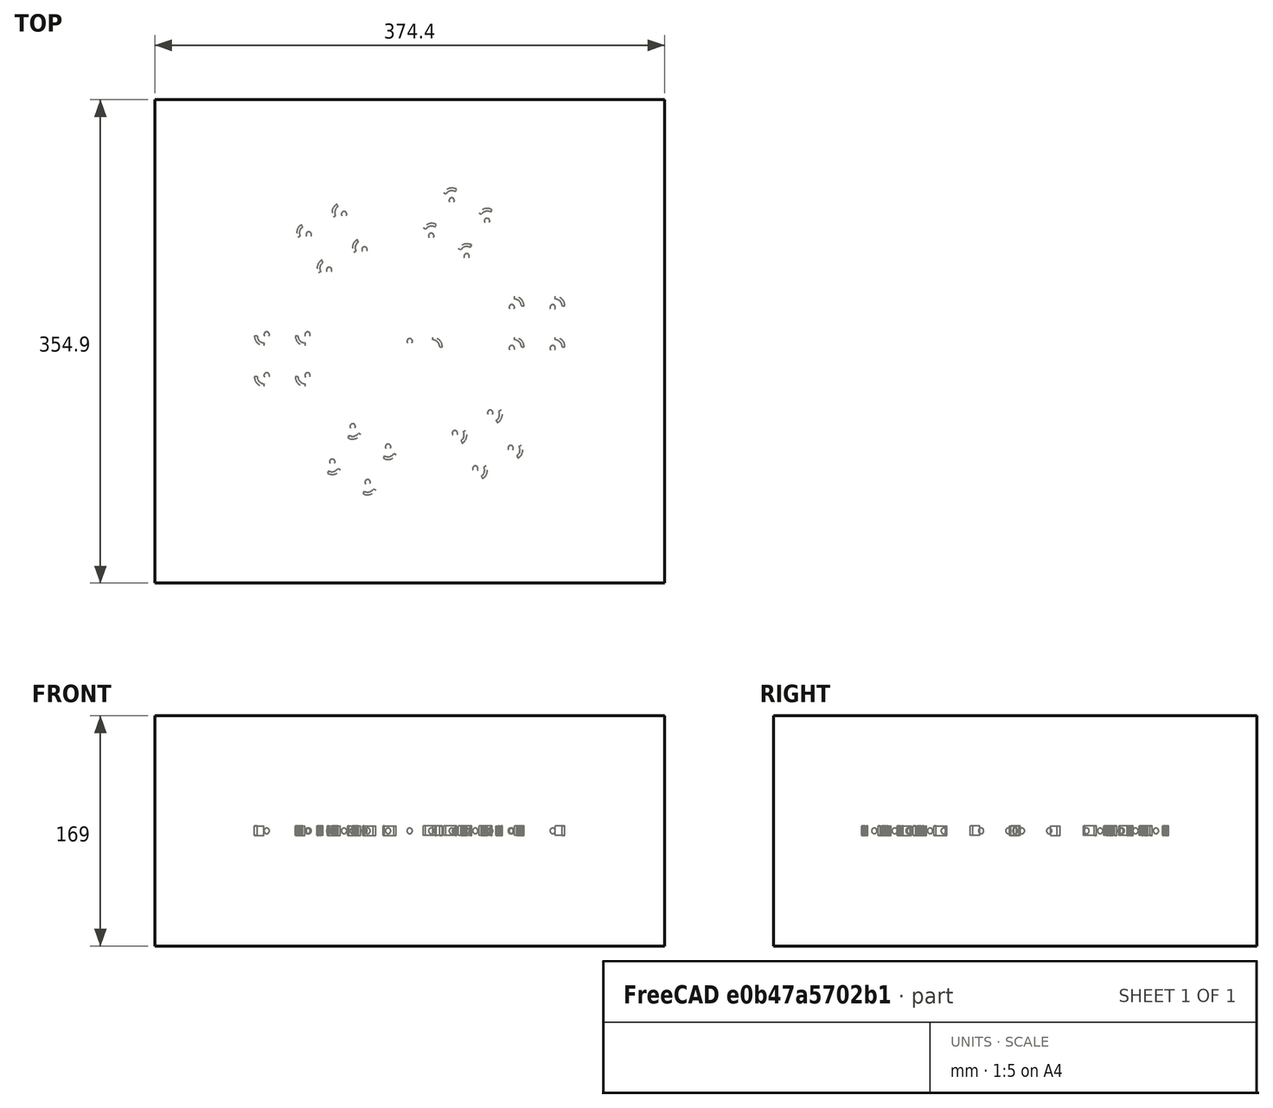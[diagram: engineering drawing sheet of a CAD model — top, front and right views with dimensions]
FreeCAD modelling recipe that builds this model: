
FCSTD DOCUMENT  (FreeCAD 0.21R33694 (Git))
Label: polarArrray-of-orthoArray-of-Assembly
License: All rights reserved
LicenseURL: http://en.wikipedia.org/wiki/All_rights_reserved
objects: App::DocumentObjectGroupPython×1251, App::Part×6, Part::FeaturePython×5
note: 5 computed .brp shape members not serialized (recipe doc carries the construction recipe); baked Part::Feature solids carry a one-line shape summary decoded from their .brp

FEATURE [App::DocumentObjectGroupPython] HALFPI  # scripted group (container) (typed FeaturePython)
  name = HALFPI
  value = pi/2.
FEATURE [App::DocumentObjectGroupPython] PI  # scripted group (container) (typed FeaturePython)
  name = PI
  value = 1.*pi
FEATURE [App::DocumentObjectGroupPython] TWOPI  # scripted group (container) (typed FeaturePython)
  name = TWOPI
  value = 2.*pi
FEATURE [App::DocumentObjectGroupPython] Constants  # scripted group (container) (typed FeaturePython)
  Group = -> [HALFPI,PI,TWOPI]
FEATURE [App::DocumentObjectGroupPython] Variables  # scripted group (container) (typed FeaturePython)
FEATURE [App::DocumentObjectGroupPython] Quantities  # scripted group (container) (typed FeaturePython)
FEATURE [App::DocumentObjectGroupPython] Isotopes  # scripted group (container) (typed FeaturePython)
FEATURE [App::DocumentObjectGroupPython] Elements  # scripted group (container) (typed FeaturePython)
FEATURE [App::DocumentObjectGroupPython] Matrix  # scripted group (container) (typed FeaturePython)
FEATURE [App::DocumentObjectGroupPython] Surfaces  # scripted group (container) (typed FeaturePython)
FEATURE [App::DocumentObjectGroupPython] Opticals  # scripted group (container) (typed FeaturePython)
  Group = -> [Matrix,Surfaces]
FEATURE [App::DocumentObjectGroupPython] G4Isotopes  # scripted group (container) (typed FeaturePython)
FEATURE [App::DocumentObjectGroupPython] H_element  # scripted group (container) (typed FeaturePython)
  Z = 1
  atom_value = 1.008
  formula = H
  name = H_element
FEATURE [App::DocumentObjectGroupPython] He_element  # scripted group (container) (typed FeaturePython)
  Z = 2
  atom_value = 4.0026
  formula = He
  name = He_element
FEATURE [App::DocumentObjectGroupPython] Li_element  # scripted group (container) (typed FeaturePython)
  Z = 3
  atom_value = 6.94
  formula = Li
  name = Li_element
FEATURE [App::DocumentObjectGroupPython] Be_element  # scripted group (container) (typed FeaturePython)
  Z = 4
  atom_value = 9.01218
  formula = Be
  name = Be_element
FEATURE [App::DocumentObjectGroupPython] B_element  # scripted group (container) (typed FeaturePython)
  Z = 5
  atom_value = 10.81
  formula = B
  name = B_element
FEATURE [App::DocumentObjectGroupPython] C_element  # scripted group (container) (typed FeaturePython)
  Z = 6
  atom_value = 12.011
  formula = C
  name = C_element
FEATURE [App::DocumentObjectGroupPython] N_element  # scripted group (container) (typed FeaturePython)
  Z = 7
  atom_value = 14.007
  formula = N
  name = N_element
FEATURE [App::DocumentObjectGroupPython] O_element  # scripted group (container) (typed FeaturePython)
  Z = 8
  atom_value = 15.999
  formula = O
  name = O_element
FEATURE [App::DocumentObjectGroupPython] F_element  # scripted group (container) (typed FeaturePython)
  Z = 9
  atom_value = 18.9984
  formula = F
  name = F_element
FEATURE [App::DocumentObjectGroupPython] Ne_element  # scripted group (container) (typed FeaturePython)
  Z = 10
  atom_value = 20.1797
  formula = Ne
  name = Ne_element
FEATURE [App::DocumentObjectGroupPython] Na_element  # scripted group (container) (typed FeaturePython)
  Z = 11
  atom_value = 22.9898
  formula = Na
  name = Na_element
FEATURE [App::DocumentObjectGroupPython] Mg_element  # scripted group (container) (typed FeaturePython)
  Z = 12
  atom_value = 24.305
  formula = Mg
  name = Mg_element
FEATURE [App::DocumentObjectGroupPython] Al_element  # scripted group (container) (typed FeaturePython)
  Z = 13
  atom_value = 26.9815
  formula = Al
  name = Al_element
FEATURE [App::DocumentObjectGroupPython] Si_element  # scripted group (container) (typed FeaturePython)
  Z = 14
  atom_value = 28.085
  formula = Si
  name = Si_element
FEATURE [App::DocumentObjectGroupPython] P_element  # scripted group (container) (typed FeaturePython)
  Z = 15
  atom_value = 30.9738
  formula = P
  name = P_element
FEATURE [App::DocumentObjectGroupPython] S_element  # scripted group (container) (typed FeaturePython)
  Z = 16
  atom_value = 32.06
  formula = S
  name = S_element
FEATURE [App::DocumentObjectGroupPython] Cl_element  # scripted group (container) (typed FeaturePython)
  Z = 17
  atom_value = 35.45
  formula = Cl
  name = Cl_element
FEATURE [App::DocumentObjectGroupPython] Ar_element  # scripted group (container) (typed FeaturePython)
  Z = 18
  atom_value = 39.95
  formula = Ar
  name = Ar_element
FEATURE [App::DocumentObjectGroupPython] K_element  # scripted group (container) (typed FeaturePython)
  Z = 19
  atom_value = 39.0983
  formula = K
  name = K_element
FEATURE [App::DocumentObjectGroupPython] Ca_element  # scripted group (container) (typed FeaturePython)
  Z = 20
  atom_value = 40.078
  formula = Ca
  name = Ca_element
FEATURE [App::DocumentObjectGroupPython] Sc_element  # scripted group (container) (typed FeaturePython)
  Z = 21
  atom_value = 44.9559
  formula = Sc
  name = Sc_element
FEATURE [App::DocumentObjectGroupPython] Ti_element  # scripted group (container) (typed FeaturePython)
  Z = 22
  atom_value = 47.867
  formula = Ti
  name = Ti_element
FEATURE [App::DocumentObjectGroupPython] V_element  # scripted group (container) (typed FeaturePython)
  Z = 23
  atom_value = 50.9415
  formula = V
  name = V_element
FEATURE [App::DocumentObjectGroupPython] Cr_element  # scripted group (container) (typed FeaturePython)
  Z = 24
  atom_value = 51.9961
  formula = Cr
  name = Cr_element
FEATURE [App::DocumentObjectGroupPython] Mn_element  # scripted group (container) (typed FeaturePython)
  Z = 25
  atom_value = 54.938
  formula = Mn
  name = Mn_element
FEATURE [App::DocumentObjectGroupPython] Fe_element  # scripted group (container) (typed FeaturePython)
  Z = 26
  atom_value = 55.845
  formula = Fe
  name = Fe_element
FEATURE [App::DocumentObjectGroupPython] Co_element  # scripted group (container) (typed FeaturePython)
  Z = 27
  atom_value = 58.9332
  formula = Co
  name = Co_element
FEATURE [App::DocumentObjectGroupPython] Ni_element  # scripted group (container) (typed FeaturePython)
  Z = 28
  atom_value = 58.6934
  formula = Ni
  name = Ni_element
FEATURE [App::DocumentObjectGroupPython] Cu_element  # scripted group (container) (typed FeaturePython)
  Z = 29
  atom_value = 63.546
  formula = Cu
  name = Cu_element
FEATURE [App::DocumentObjectGroupPython] Zn_element  # scripted group (container) (typed FeaturePython)
  Z = 30
  atom_value = 65.38
  formula = Zn
  name = Zn_element
FEATURE [App::DocumentObjectGroupPython] Ga_element  # scripted group (container) (typed FeaturePython)
  Z = 31
  atom_value = 69.723
  formula = Ga
  name = Ga_element
FEATURE [App::DocumentObjectGroupPython] Ge_element  # scripted group (container) (typed FeaturePython)
  Z = 32
  atom_value = 72.63
  formula = Ge
  name = Ge_element
FEATURE [App::DocumentObjectGroupPython] As_element  # scripted group (container) (typed FeaturePython)
  Z = 33
  atom_value = 74.9216
  formula = As
  name = As_element
FEATURE [App::DocumentObjectGroupPython] Se_element  # scripted group (container) (typed FeaturePython)
  Z = 34
  atom_value = 78.971
  formula = Se
  name = Se_element
FEATURE [App::DocumentObjectGroupPython] Br_element  # scripted group (container) (typed FeaturePython)
  Z = 35
  atom_value = 79.904
  formula = Br
  name = Br_element
FEATURE [App::DocumentObjectGroupPython] Kr_element  # scripted group (container) (typed FeaturePython)
  Z = 36
  atom_value = 83.798
  formula = Kr
  name = Kr_element
FEATURE [App::DocumentObjectGroupPython] Rb_element  # scripted group (container) (typed FeaturePython)
  Z = 37
  atom_value = 85.4678
  formula = Rb
  name = Rb_element
FEATURE [App::DocumentObjectGroupPython] Sr_element  # scripted group (container) (typed FeaturePython)
  Z = 38
  atom_value = 87.62
  formula = Sr
  name = Sr_element
FEATURE [App::DocumentObjectGroupPython] Y_element  # scripted group (container) (typed FeaturePython)
  Z = 39
  atom_value = 88.9058
  formula = Y
  name = Y_element
FEATURE [App::DocumentObjectGroupPython] Zr_element  # scripted group (container) (typed FeaturePython)
  Z = 40
  atom_value = 91.224
  formula = Zr
  name = Zr_element
FEATURE [App::DocumentObjectGroupPython] Nb_element  # scripted group (container) (typed FeaturePython)
  Z = 41
  atom_value = 92.9064
  formula = Nb
  name = Nb_element
FEATURE [App::DocumentObjectGroupPython] Mo_element  # scripted group (container) (typed FeaturePython)
  Z = 42
  atom_value = 95.95
  formula = Mo
  name = Mo_element
FEATURE [App::DocumentObjectGroupPython] Tc_element  # scripted group (container) (typed FeaturePython)
  Z = 43
  atom_value = 97
  formula = Tc
  name = Tc_element
FEATURE [App::DocumentObjectGroupPython] Ru_element  # scripted group (container) (typed FeaturePython)
  Z = 44
  atom_value = 101.07
  formula = Ru
  name = Ru_element
FEATURE [App::DocumentObjectGroupPython] Rh_element  # scripted group (container) (typed FeaturePython)
  Z = 45
  atom_value = 102.905
  formula = Rh
  name = Rh_element
FEATURE [App::DocumentObjectGroupPython] Pd_element  # scripted group (container) (typed FeaturePython)
  Z = 46
  atom_value = 106.42
  formula = Pd
  name = Pd_element
FEATURE [App::DocumentObjectGroupPython] Ag_element  # scripted group (container) (typed FeaturePython)
  Z = 47
  atom_value = 107.868
  formula = Ag
  name = Ag_element
FEATURE [App::DocumentObjectGroupPython] Cd_element  # scripted group (container) (typed FeaturePython)
  Z = 48
  atom_value = 112.414
  formula = Cd
  name = Cd_element
FEATURE [App::DocumentObjectGroupPython] In_element  # scripted group (container) (typed FeaturePython)
  Z = 49
  atom_value = 114.818
  formula = In
  name = In_element
FEATURE [App::DocumentObjectGroupPython] Sn_element  # scripted group (container) (typed FeaturePython)
  Z = 50
  atom_value = 118.71
  formula = Sn
  name = Sn_element
FEATURE [App::DocumentObjectGroupPython] Sb_element  # scripted group (container) (typed FeaturePython)
  Z = 51
  atom_value = 121.76
  formula = Sb
  name = Sb_element
FEATURE [App::DocumentObjectGroupPython] Te_element  # scripted group (container) (typed FeaturePython)
  Z = 52
  atom_value = 127.6
  formula = Te
  name = Te_element
FEATURE [App::DocumentObjectGroupPython] I_element  # scripted group (container) (typed FeaturePython)
  Z = 53
  atom_value = 126.904
  formula = I
  name = I_element
FEATURE [App::DocumentObjectGroupPython] Xe_element  # scripted group (container) (typed FeaturePython)
  Z = 54
  atom_value = 131.293
  formula = Xe
  name = Xe_element
FEATURE [App::DocumentObjectGroupPython] Cs_element  # scripted group (container) (typed FeaturePython)
  Z = 55
  atom_value = 132.905
  formula = Cs
  name = Cs_element
FEATURE [App::DocumentObjectGroupPython] Ba_element  # scripted group (container) (typed FeaturePython)
  Z = 56
  atom_value = 137.327
  formula = Ba
  name = Ba_element
FEATURE [App::DocumentObjectGroupPython] La_element  # scripted group (container) (typed FeaturePython)
  Z = 57
  atom_value = 138.905
  formula = La
  name = La_element
FEATURE [App::DocumentObjectGroupPython] Ce_element  # scripted group (container) (typed FeaturePython)
  Z = 58
  atom_value = 140.116
  formula = Ce
  name = Ce_element
FEATURE [App::DocumentObjectGroupPython] Pr_element  # scripted group (container) (typed FeaturePython)
  Z = 59
  atom_value = 140.908
  formula = Pr
  name = Pr_element
FEATURE [App::DocumentObjectGroupPython] Nd_element  # scripted group (container) (typed FeaturePython)
  Z = 60
  atom_value = 144.242
  formula = Nd
  name = Nd_element
FEATURE [App::DocumentObjectGroupPython] Pm_element  # scripted group (container) (typed FeaturePython)
  Z = 61
  atom_value = 145
  formula = Pm
  name = Pm_element
FEATURE [App::DocumentObjectGroupPython] Sm_element  # scripted group (container) (typed FeaturePython)
  Z = 62
  atom_value = 150.36
  formula = Sm
  name = Sm_element
FEATURE [App::DocumentObjectGroupPython] Eu_element  # scripted group (container) (typed FeaturePython)
  Z = 63
  atom_value = 151.964
  formula = Eu
  name = Eu_element
FEATURE [App::DocumentObjectGroupPython] Gd_element  # scripted group (container) (typed FeaturePython)
  Z = 64
  atom_value = 157.25
  formula = Gd
  name = Gd_element
FEATURE [App::DocumentObjectGroupPython] Tb_element  # scripted group (container) (typed FeaturePython)
  Z = 65
  atom_value = 158.925
  formula = Tb
  name = Tb_element
FEATURE [App::DocumentObjectGroupPython] Dy_element  # scripted group (container) (typed FeaturePython)
  Z = 66
  atom_value = 162.5
  formula = Dy
  name = Dy_element
FEATURE [App::DocumentObjectGroupPython] Ho_element  # scripted group (container) (typed FeaturePython)
  Z = 67
  atom_value = 164.93
  formula = Ho
  name = Ho_element
FEATURE [App::DocumentObjectGroupPython] Er_element  # scripted group (container) (typed FeaturePython)
  Z = 68
  atom_value = 167.259
  formula = Er
  name = Er_element
FEATURE [App::DocumentObjectGroupPython] Tm_element  # scripted group (container) (typed FeaturePython)
  Z = 69
  atom_value = 168.934
  formula = Tm
  name = Tm_element
FEATURE [App::DocumentObjectGroupPython] Yb_element  # scripted group (container) (typed FeaturePython)
  Z = 70
  atom_value = 173.045
  formula = Yb
  name = Yb_element
FEATURE [App::DocumentObjectGroupPython] Lu_element  # scripted group (container) (typed FeaturePython)
  Z = 71
  atom_value = 174.967
  formula = Lu
  name = Lu_element
FEATURE [App::DocumentObjectGroupPython] Hf_element  # scripted group (container) (typed FeaturePython)
  Z = 72
  atom_value = 178.49
  formula = Hf
  name = Hf_element
FEATURE [App::DocumentObjectGroupPython] Ta_element  # scripted group (container) (typed FeaturePython)
  Z = 73
  atom_value = 180.948
  formula = Ta
  name = Ta_element
FEATURE [App::DocumentObjectGroupPython] W_element  # scripted group (container) (typed FeaturePython)
  Z = 74
  atom_value = 183.84
  formula = W
  name = W_element
FEATURE [App::DocumentObjectGroupPython] Re_element  # scripted group (container) (typed FeaturePython)
  Z = 75
  atom_value = 186.207
  formula = Re
  name = Re_element
FEATURE [App::DocumentObjectGroupPython] Os_element  # scripted group (container) (typed FeaturePython)
  Z = 76
  atom_value = 190.23
  formula = Os
  name = Os_element
FEATURE [App::DocumentObjectGroupPython] Ir_element  # scripted group (container) (typed FeaturePython)
  Z = 77
  atom_value = 192.217
  formula = Ir
  name = Ir_element
FEATURE [App::DocumentObjectGroupPython] Pt_element  # scripted group (container) (typed FeaturePython)
  Z = 78
  atom_value = 195.084
  formula = Pt
  name = Pt_element
FEATURE [App::DocumentObjectGroupPython] Au_element  # scripted group (container) (typed FeaturePython)
  Z = 79
  atom_value = 196.967
  formula = Au
  name = Au_element
FEATURE [App::DocumentObjectGroupPython] Hg_element  # scripted group (container) (typed FeaturePython)
  Z = 80
  atom_value = 200.592
  formula = Hg
  name = Hg_element
FEATURE [App::DocumentObjectGroupPython] Tl_element  # scripted group (container) (typed FeaturePython)
  Z = 81
  atom_value = 204.38
  formula = Tl
  name = Tl_element
FEATURE [App::DocumentObjectGroupPython] Pb_element  # scripted group (container) (typed FeaturePython)
  Z = 82
  atom_value = 207.2
  formula = Pb
  name = Pb_element
FEATURE [App::DocumentObjectGroupPython] Bi_element  # scripted group (container) (typed FeaturePython)
  Z = 83
  atom_value = 208.98
  formula = Bi
  name = Bi_element
FEATURE [App::DocumentObjectGroupPython] Po_element  # scripted group (container) (typed FeaturePython)
  Z = 84
  atom_value = 209
  formula = Po
  name = Po_element
FEATURE [App::DocumentObjectGroupPython] At_element  # scripted group (container) (typed FeaturePython)
  Z = 85
  atom_value = 210
  formula = At
  name = At_element
FEATURE [App::DocumentObjectGroupPython] Rn_element  # scripted group (container) (typed FeaturePython)
  Z = 86
  atom_value = 222
  formula = Rn
  name = Rn_element
FEATURE [App::DocumentObjectGroupPython] Fr_element  # scripted group (container) (typed FeaturePython)
  Z = 87
  atom_value = 223
  formula = Fr
  name = Fr_element
FEATURE [App::DocumentObjectGroupPython] Ra_element  # scripted group (container) (typed FeaturePython)
  Z = 88
  atom_value = 226
  formula = Ra
  name = Ra_element
FEATURE [App::DocumentObjectGroupPython] Ac_element  # scripted group (container) (typed FeaturePython)
  Z = 89
  atom_value = 227
  formula = Ac
  name = Ac_element
FEATURE [App::DocumentObjectGroupPython] Th_element  # scripted group (container) (typed FeaturePython)
  Z = 90
  atom_value = 232.038
  formula = Th
  name = Th_element
FEATURE [App::DocumentObjectGroupPython] Pa_element  # scripted group (container) (typed FeaturePython)
  Z = 91
  atom_value = 231.036
  formula = Pa
  name = Pa_element
FEATURE [App::DocumentObjectGroupPython] U_element  # scripted group (container) (typed FeaturePython)
  Z = 92
  atom_value = 238.029
  formula = U
  name = U_element
FEATURE [App::DocumentObjectGroupPython] Np_element  # scripted group (container) (typed FeaturePython)
  Z = 93
  atom_value = 237
  formula = Np
  name = Np_element
FEATURE [App::DocumentObjectGroupPython] Pu_element  # scripted group (container) (typed FeaturePython)
  Z = 94
  atom_value = 244
  formula = Pu
  name = Pu_element
FEATURE [App::DocumentObjectGroupPython] Am_element  # scripted group (container) (typed FeaturePython)
  Z = 95
  atom_value = 243
  formula = Am
  name = Am_element
FEATURE [App::DocumentObjectGroupPython] Cm_element  # scripted group (container) (typed FeaturePython)
  Z = 96
  atom_value = 247
  formula = Cm
  name = Cm_element
FEATURE [App::DocumentObjectGroupPython] Bk_element  # scripted group (container) (typed FeaturePython)
  Z = 97
  atom_value = 247
  formula = Bk
  name = Bk_element
FEATURE [App::DocumentObjectGroupPython] Cf_element  # scripted group (container) (typed FeaturePython)
  Z = 98
  atom_value = 251
  formula = Cf
  name = Cf_element
FEATURE [App::DocumentObjectGroupPython] G4Elements  # scripted group (container) (typed FeaturePython)
  Group = -> [H_element,He_element,Li_element,Be_element,B_element,C_element,N_element,O_element,F_element,Ne_element,Na_element,Mg_element,Al_element,Si_element,P_element,S_element,Cl_element,Ar_element,K_element,Ca_element,Sc_element,Ti_element,V_element,Cr_element,Mn_element,Fe_element,Co_element,Ni_element,Cu_element,Zn_element,Ga_element,Ge_element,As_element,Se_element,Br_element,Kr_element,Rb_element,+61 more]
FEATURE [App::DocumentObjectGroupPython] H_element001  label="H_element : 0.101"  # scripted group (container) (typed FeaturePython)
  n = 0.101327
FEATURE [App::DocumentObjectGroupPython] C_element001  label="C_element : 0.775"  # scripted group (container) (typed FeaturePython)
  n = 0.7755
FEATURE [App::DocumentObjectGroupPython] N_element001  label="N_element : 0.035"  # scripted group (container) (typed FeaturePython)
  n = 0.035057
FEATURE [App::DocumentObjectGroupPython] O_element001  label="O_element : 0.052"  # scripted group (container) (typed FeaturePython)
  n = 0.0523159
FEATURE [App::DocumentObjectGroupPython] F_element001  label="F_element : 0.017"  # scripted group (container) (typed FeaturePython)
  n = 0.017422
FEATURE [App::DocumentObjectGroupPython] Ca_element001  label="Ca_element : 0.018"  # scripted group (container) (typed FeaturePython)
  n = 0.018378
FEATURE [App::DocumentObjectGroupPython] G4_A_150_TISSUE  label="G4_A-150_TISSUE"  # scripted group (container) (typed FeaturePython)
  Dunit = g/cm3
  Dvalue = 1.127
  Group = -> [H_element001,C_element001,N_element001,O_element001,F_element001,Ca_element001]
  conduct = 2
  density = 1
  expand = 3
  formula = G4_A-150_TISSUE
  name = G4_A-150_TISSUE
  specific = 4
FEATURE [App::DocumentObjectGroupPython] C_element002  label="C_element : 3"  # scripted group (container) (typed FeaturePython)
  n = 3
  ref = C_element
FEATURE [App::DocumentObjectGroupPython] H_element002  label="H_element : 6"  # scripted group (container) (typed FeaturePython)
  n = 6
  ref = H_element
FEATURE [App::DocumentObjectGroupPython] O_element002  label="O_element : 1"  # scripted group (container) (typed FeaturePython)
  n = 1
  ref = O_element
FEATURE [App::DocumentObjectGroupPython] G4_ACETONE  # scripted group (container) (typed FeaturePython)
  Dunit = g/cm3
  Dvalue = 0.7899
  Group = -> [C_element002,H_element002,O_element002]
  conduct = 2
  density = 1
  expand = 3
  formula = G4_ACETONE
  name = G4_ACETONE
  specific = 4
FEATURE [App::DocumentObjectGroupPython] C_element003  label="C_element : 2"  # scripted group (container) (typed FeaturePython)
  n = 2
  ref = C_element
FEATURE [App::DocumentObjectGroupPython] H_element003  label="H_element : 2"  # scripted group (container) (typed FeaturePython)
  n = 2
  ref = H_element
FEATURE [App::DocumentObjectGroupPython] G4_ACETYLENE  # scripted group (container) (typed FeaturePython)
  Dunit = g/cm3
  Dvalue = 0.0010967
  Group = -> [C_element003,H_element003]
  conduct = 2
  density = 1
  expand = 3
  formula = G4_ACETYLENE
  name = G4_ACETYLENE
  specific = 4
FEATURE [App::DocumentObjectGroupPython] C_element004  label="C_element : 5"  # scripted group (container) (typed FeaturePython)
  n = 5
  ref = C_element
FEATURE [App::DocumentObjectGroupPython] H_element004  label="H_element : 5"  # scripted group (container) (typed FeaturePython)
  n = 5
  ref = H_element
FEATURE [App::DocumentObjectGroupPython] N_element002  label="N_element : 5"  # scripted group (container) (typed FeaturePython)
  n = 5
  ref = N_element
FEATURE [App::DocumentObjectGroupPython] G4_ADENINE  # scripted group (container) (typed FeaturePython)
  Dunit = g/cm3
  Dvalue = 1.6
  Group = -> [C_element004,H_element004,N_element002]
  conduct = 2
  density = 1
  expand = 3
  formula = G4_ADENINE
  name = G4_ADENINE
  specific = 4
FEATURE [App::DocumentObjectGroupPython] H_element005  label="H_element : 0.114"  # scripted group (container) (typed FeaturePython)
  n = 0.114
FEATURE [App::DocumentObjectGroupPython] C_element005  label="C_element : 0.598"  # scripted group (container) (typed FeaturePython)
  n = 0.598
FEATURE [App::DocumentObjectGroupPython] N_element003  label="N_element : 0.007"  # scripted group (container) (typed FeaturePython)
  n = 0.007
FEATURE [App::DocumentObjectGroupPython] O_element003  label="O_element : 0.278"  # scripted group (container) (typed FeaturePython)
  n = 0.278
FEATURE [App::DocumentObjectGroupPython] Na_element001  label="Na_element : 0.001"  # scripted group (container) (typed FeaturePython)
  n = 0.001
FEATURE [App::DocumentObjectGroupPython] S_element001  label="S_element : 0.001"  # scripted group (container) (typed FeaturePython)
  n = 0.001
FEATURE [App::DocumentObjectGroupPython] Cl_element001  label="Cl_element : 0.001"  # scripted group (container) (typed FeaturePython)
  n = 0.001
FEATURE [App::DocumentObjectGroupPython] G4_ADIPOSE_TISSUE_ICRP  # scripted group (container) (typed FeaturePython)
  Dunit = g/cm3
  Dvalue = 0.95
  Group = -> [H_element005,C_element005,N_element003,O_element003,Na_element001,S_element001,Cl_element001]
  conduct = 2
  density = 1
  expand = 3
  formula = G4_ADIPOSE_TISSUE_ICRP
  name = G4_ADIPOSE_TISSUE_ICRP
  specific = 4
FEATURE [App::DocumentObjectGroupPython] C_element006  label="C_element : 0.000"  # scripted group (container) (typed FeaturePython)
  n = 0.000124
FEATURE [App::DocumentObjectGroupPython] N_element004  label="N_element : 0.755"  # scripted group (container) (typed FeaturePython)
  n = 0.755268
FEATURE [App::DocumentObjectGroupPython] O_element004  label="O_element : 0.232"  # scripted group (container) (typed FeaturePython)
  n = 0.231781
FEATURE [App::DocumentObjectGroupPython] Ar_element001  label="Ar_element : 0.013"  # scripted group (container) (typed FeaturePython)
  n = 0.012827
FEATURE [App::DocumentObjectGroupPython] G4_AIR  # scripted group (container) (typed FeaturePython)
  Dunit = g/cm3
  Dvalue = 0.00120479
  Group = -> [C_element006,N_element004,O_element004,Ar_element001]
  conduct = 2
  density = 1
  expand = 3
  formula = G4_AIR
  name = G4_AIR
  specific = 4
FEATURE [App::DocumentObjectGroupPython] C_element007  label="C_element : 006"  # scripted group (container) (typed FeaturePython)
  n = 3
  ref = C_element
FEATURE [App::DocumentObjectGroupPython] H_element006  label="H_element : 7"  # scripted group (container) (typed FeaturePython)
  n = 7
  ref = H_element
FEATURE [App::DocumentObjectGroupPython] N_element005  label="N_element : 1"  # scripted group (container) (typed FeaturePython)
  n = 1
  ref = N_element
FEATURE [App::DocumentObjectGroupPython] O_element005  label="O_element : 2"  # scripted group (container) (typed FeaturePython)
  n = 2
  ref = O_element
FEATURE [App::DocumentObjectGroupPython] G4_ALANINE  # scripted group (container) (typed FeaturePython)
  Dunit = g/cm3
  Dvalue = 1.42
  Group = -> [C_element007,H_element006,N_element005,O_element005]
  conduct = 2
  density = 1
  expand = 3
  formula = G4_ALANINE
  name = G4_ALANINE
  specific = 4
FEATURE [App::DocumentObjectGroupPython] Al_element001  label="Al_element : 2"  # scripted group (container) (typed FeaturePython)
  n = 2
  ref = Al_element
FEATURE [App::DocumentObjectGroupPython] O_element006  label="O_element : 3"  # scripted group (container) (typed FeaturePython)
  n = 3
  ref = O_element
FEATURE [App::DocumentObjectGroupPython] G4_ALUMINUM_OXIDE  # scripted group (container) (typed FeaturePython)
  Dunit = g/cm3
  Dvalue = 3.97
  Group = -> [Al_element001,O_element006]
  conduct = 2
  density = 1
  expand = 3
  formula = G4_ALUMINUM_OXIDE
  name = G4_ALUMINUM_OXIDE
  specific = 4
FEATURE [App::DocumentObjectGroupPython] H_element007  label="H_element : 0.106"  # scripted group (container) (typed FeaturePython)
  n = 0.10593
FEATURE [App::DocumentObjectGroupPython] C_element008  label="C_element : 0.789"  # scripted group (container) (typed FeaturePython)
  n = 0.788974
FEATURE [App::DocumentObjectGroupPython] O_element007  label="O_element : 0.105"  # scripted group (container) (typed FeaturePython)
  n = 0.105096
FEATURE [App::DocumentObjectGroupPython] G4_AMBER  # scripted group (container) (typed FeaturePython)
  Dunit = g/cm3
  Dvalue = 1.1
  Group = -> [H_element007,C_element008,O_element007]
  conduct = 2
  density = 1
  expand = 3
  formula = G4_AMBER
  name = G4_AMBER
  specific = 4
FEATURE [App::DocumentObjectGroupPython] N_element006  label="N_element : 006"  # scripted group (container) (typed FeaturePython)
  n = 1
  ref = N_element
FEATURE [App::DocumentObjectGroupPython] H_element008  label="H_element : 3"  # scripted group (container) (typed FeaturePython)
  n = 3
  ref = H_element
FEATURE [App::DocumentObjectGroupPython] G4_AMMONIA  # scripted group (container) (typed FeaturePython)
  Dunit = g/cm3
  Dvalue = 0.000826019
  Group = -> [N_element006,H_element008]
  conduct = 2
  density = 1
  expand = 3
  formula = G4_AMMONIA
  name = G4_AMMONIA
  specific = 4
FEATURE [App::DocumentObjectGroupPython] C_element009  label="C_element : 6"  # scripted group (container) (typed FeaturePython)
  n = 6
  ref = C_element
FEATURE [App::DocumentObjectGroupPython] H_element009  label="H_element : 008"  # scripted group (container) (typed FeaturePython)
  n = 7
  ref = H_element
FEATURE [App::DocumentObjectGroupPython] N_element007  label="N_element : 007"  # scripted group (container) (typed FeaturePython)
  n = 1
  ref = N_element
FEATURE [App::DocumentObjectGroupPython] G4_ANILINE  # scripted group (container) (typed FeaturePython)
  Dunit = g/cm3
  Dvalue = 1.0235
  Group = -> [C_element009,H_element009,N_element007]
  conduct = 2
  density = 1
  expand = 3
  formula = G4_ANILINE
  name = G4_ANILINE
  specific = 4
FEATURE [App::DocumentObjectGroupPython] C_element010  label="C_element : 14"  # scripted group (container) (typed FeaturePython)
  n = 14
  ref = C_element
FEATURE [App::DocumentObjectGroupPython] H_element010  label="H_element : 10"  # scripted group (container) (typed FeaturePython)
  n = 10
  ref = H_element
FEATURE [App::DocumentObjectGroupPython] G4_ANTHRACENE  # scripted group (container) (typed FeaturePython)
  Dunit = g/cm3
  Dvalue = 1.283
  Group = -> [C_element010,H_element010]
  conduct = 2
  density = 1
  expand = 3
  formula = G4_ANTHRACENE
  name = G4_ANTHRACENE
  specific = 4
FEATURE [App::DocumentObjectGroupPython] H_element011  label="H_element : 0.065"  # scripted group (container) (typed FeaturePython)
  n = 0.0654709
FEATURE [App::DocumentObjectGroupPython] C_element011  label="C_element : 0.537"  # scripted group (container) (typed FeaturePython)
  n = 0.536944
FEATURE [App::DocumentObjectGroupPython] N_element008  label="N_element : 0.021"  # scripted group (container) (typed FeaturePython)
  n = 0.0215
FEATURE [App::DocumentObjectGroupPython] O_element008  label="O_element : 0.032"  # scripted group (container) (typed FeaturePython)
  n = 0.032085
FEATURE [App::DocumentObjectGroupPython] F_element002  label="F_element : 0.167"  # scripted group (container) (typed FeaturePython)
  n = 0.167411
FEATURE [App::DocumentObjectGroupPython] Ca_element002  label="Ca_element : 0.177"  # scripted group (container) (typed FeaturePython)
  n = 0.176589
FEATURE [App::DocumentObjectGroupPython] G4_B_100_BONE  label="G4_B-100_BONE"  # scripted group (container) (typed FeaturePython)
  Dunit = g/cm3
  Dvalue = 1.45
  Group = -> [H_element011,C_element011,N_element008,O_element008,F_element002,Ca_element002]
  conduct = 2
  density = 1
  expand = 3
  formula = G4_B-100_BONE
  name = G4_B-100_BONE
  specific = 4
FEATURE [App::DocumentObjectGroupPython] H_element012  label="H_element : 0.057"  # scripted group (container) (typed FeaturePython)
  n = 0.057441
FEATURE [App::DocumentObjectGroupPython] C_element012  label="C_element : 0.790"  # scripted group (container) (typed FeaturePython)
  n = 0.774591
FEATURE [App::DocumentObjectGroupPython] O_element009  label="O_element : 0.168"  # scripted group (container) (typed FeaturePython)
  n = 0.167968
FEATURE [App::DocumentObjectGroupPython] G4_BAKELITE  # scripted group (container) (typed FeaturePython)
  Dunit = g/cm3
  Dvalue = 1.25
  Group = -> [H_element012,C_element012,O_element009]
  conduct = 2
  density = 1
  expand = 3
  formula = G4_BAKELITE
  name = G4_BAKELITE
  specific = 4
FEATURE [App::DocumentObjectGroupPython] Ba_element001  label="Ba_element : 1"  # scripted group (container) (typed FeaturePython)
  n = 1
  ref = Ba_element
FEATURE [App::DocumentObjectGroupPython] F_element003  label="F_element : 2"  # scripted group (container) (typed FeaturePython)
  n = 2
  ref = F_element
FEATURE [App::DocumentObjectGroupPython] G4_BARIUM_FLUORIDE  # scripted group (container) (typed FeaturePython)
  Dunit = g/cm3
  Dvalue = 4.89
  Group = -> [Ba_element001,F_element003]
  conduct = 2
  density = 1
  expand = 3
  formula = G4_BARIUM_FLUORIDE
  name = G4_BARIUM_FLUORIDE
  specific = 4
FEATURE [App::DocumentObjectGroupPython] Ba_element002  label="Ba_element : 002"  # scripted group (container) (typed FeaturePython)
  n = 1
  ref = Ba_element
FEATURE [App::DocumentObjectGroupPython] S_element002  label="S_element : 1"  # scripted group (container) (typed FeaturePython)
  n = 1
  ref = S_element
FEATURE [App::DocumentObjectGroupPython] O_element010  label="O_element : 4"  # scripted group (container) (typed FeaturePython)
  n = 4
  ref = O_element
FEATURE [App::DocumentObjectGroupPython] G4_BARIUM_SULFATE  # scripted group (container) (typed FeaturePython)
  Dunit = g/cm3
  Dvalue = 4.5
  Group = -> [Ba_element002,S_element002,O_element010]
  conduct = 2
  density = 1
  expand = 3
  formula = G4_BARIUM_SULFATE
  name = G4_BARIUM_SULFATE
  specific = 4
FEATURE [App::DocumentObjectGroupPython] C_element013  label="C_element : 007"  # scripted group (container) (typed FeaturePython)
  n = 6
  ref = C_element
FEATURE [App::DocumentObjectGroupPython] H_element013  label="H_element : 009"  # scripted group (container) (typed FeaturePython)
  n = 6
  ref = H_element
FEATURE [App::DocumentObjectGroupPython] G4_BENZENE  # scripted group (container) (typed FeaturePython)
  Dunit = g/cm3
  Dvalue = 0.87865
  Group = -> [C_element013,H_element013]
  conduct = 2
  density = 1
  expand = 3
  formula = G4_BENZENE
  name = G4_BENZENE
  specific = 4
FEATURE [App::DocumentObjectGroupPython] Be_element001  label="Be_element : 1"  # scripted group (container) (typed FeaturePython)
  n = 1
  ref = Be_element
FEATURE [App::DocumentObjectGroupPython] O_element011  label="O_element : 005"  # scripted group (container) (typed FeaturePython)
  n = 1
  ref = O_element
FEATURE [App::DocumentObjectGroupPython] G4_BERYLLIUM_OXIDE  # scripted group (container) (typed FeaturePython)
  Dunit = g/cm3
  Dvalue = 3.01
  Group = -> [Be_element001,O_element011]
  conduct = 2
  density = 1
  expand = 3
  formula = G4_BERYLLIUM_OXIDE
  name = G4_BERYLLIUM_OXIDE
  specific = 4
FEATURE [App::DocumentObjectGroupPython] Bi_element001  label="Bi_element : 4"  # scripted group (container) (typed FeaturePython)
  n = 4
  ref = Bi_element
FEATURE [App::DocumentObjectGroupPython] Ge_element001  label="Ge_element : 3"  # scripted group (container) (typed FeaturePython)
  n = 3
  ref = Ge_element
FEATURE [App::DocumentObjectGroupPython] O_element012  label="O_element : 12"  # scripted group (container) (typed FeaturePython)
  n = 12
  ref = O_element
FEATURE [App::DocumentObjectGroupPython] G4_BGO  # scripted group (container) (typed FeaturePython)
  Dunit = g/cm3
  Dvalue = 7.13
  Group = -> [Bi_element001,Ge_element001,O_element012]
  conduct = 2
  density = 1
  expand = 3
  formula = G4_BGO
  name = G4_BGO
  specific = 4
FEATURE [App::DocumentObjectGroupPython] H_element014  label="H_element : 0.102"  # scripted group (container) (typed FeaturePython)
  n = 0.102
FEATURE [App::DocumentObjectGroupPython] C_element014  label="C_element : 0.110"  # scripted group (container) (typed FeaturePython)
  n = 0.11
FEATURE [App::DocumentObjectGroupPython] N_element009  label="N_element : 0.033"  # scripted group (container) (typed FeaturePython)
  n = 0.033
FEATURE [App::DocumentObjectGroupPython] O_element013  label="O_element : 0.745"  # scripted group (container) (typed FeaturePython)
  n = 0.745
FEATURE [App::DocumentObjectGroupPython] Na_element002  label="Na_element : 0.002"  # scripted group (container) (typed FeaturePython)
  n = 0.001
FEATURE [App::DocumentObjectGroupPython] P_element001  label="P_element : 0.001"  # scripted group (container) (typed FeaturePython)
  n = 0.001
FEATURE [App::DocumentObjectGroupPython] S_element003  label="S_element : 0.002"  # scripted group (container) (typed FeaturePython)
  n = 0.002
FEATURE [App::DocumentObjectGroupPython] Cl_element002  label="Cl_element : 0.003"  # scripted group (container) (typed FeaturePython)
  n = 0.003
FEATURE [App::DocumentObjectGroupPython] K_element001  label="K_element : 0.002"  # scripted group (container) (typed FeaturePython)
  n = 0.002
FEATURE [App::DocumentObjectGroupPython] Fe_element001  label="Fe_element : 0.001"  # scripted group (container) (typed FeaturePython)
  n = 0.001
FEATURE [App::DocumentObjectGroupPython] G4_BLOOD_ICRP  # scripted group (container) (typed FeaturePython)
  Dunit = g/cm3
  Dvalue = 1.06
  Group = -> [H_element014,C_element014,N_element009,O_element013,Na_element002,P_element001,S_element003,Cl_element002,K_element001,Fe_element001]
  conduct = 2
  density = 1
  expand = 3
  formula = G4_BLOOD_ICRP
  name = G4_BLOOD_ICRP
  specific = 4
FEATURE [App::DocumentObjectGroupPython] H_element015  label="H_element : 0.064"  # scripted group (container) (typed FeaturePython)
  n = 0.064
FEATURE [App::DocumentObjectGroupPython] C_element015  label="C_element : 0.278"  # scripted group (container) (typed FeaturePython)
  n = 0.278
FEATURE [App::DocumentObjectGroupPython] N_element010  label="N_element : 0.027"  # scripted group (container) (typed FeaturePython)
  n = 0.027
FEATURE [App::DocumentObjectGroupPython] O_element014  label="O_element : 0.410"  # scripted group (container) (typed FeaturePython)
  n = 0.41
FEATURE [App::DocumentObjectGroupPython] Mg_element001  label="Mg_element : 0.002"  # scripted group (container) (typed FeaturePython)
  n = 0.002
FEATURE [App::DocumentObjectGroupPython] P_element002  label="P_element : 0.070"  # scripted group (container) (typed FeaturePython)
  n = 0.07
FEATURE [App::DocumentObjectGroupPython] S_element004  label="S_element : 0.003"  # scripted group (container) (typed FeaturePython)
  n = 0.002
FEATURE [App::DocumentObjectGroupPython] Ca_element003  label="Ca_element : 0.147"  # scripted group (container) (typed FeaturePython)
  n = 0.147
FEATURE [App::DocumentObjectGroupPython] G4_BONE_COMPACT_ICRU  # scripted group (container) (typed FeaturePython)
  Dunit = g/cm3
  Dvalue = 1.85
  Group = -> [H_element015,C_element015,N_element010,O_element014,Mg_element001,P_element002,S_element004,Ca_element003]
  conduct = 2
  density = 1
  expand = 3
  formula = G4_BONE_COMPACT_ICRU
  name = G4_BONE_COMPACT_ICRU
  specific = 4
FEATURE [App::DocumentObjectGroupPython] H_element016  label="H_element : 0.034"  # scripted group (container) (typed FeaturePython)
  n = 0.034
FEATURE [App::DocumentObjectGroupPython] C_element016  label="C_element : 0.155"  # scripted group (container) (typed FeaturePython)
  n = 0.155
FEATURE [App::DocumentObjectGroupPython] N_element011  label="N_element : 0.042"  # scripted group (container) (typed FeaturePython)
  n = 0.042
FEATURE [App::DocumentObjectGroupPython] O_element015  label="O_element : 0.435"  # scripted group (container) (typed FeaturePython)
  n = 0.435
FEATURE [App::DocumentObjectGroupPython] Na_element003  label="Na_element : 0.003"  # scripted group (container) (typed FeaturePython)
  n = 0.001
FEATURE [App::DocumentObjectGroupPython] Mg_element002  label="Mg_element : 0.003"  # scripted group (container) (typed FeaturePython)
  n = 0.002
FEATURE [App::DocumentObjectGroupPython] P_element003  label="P_element : 0.103"  # scripted group (container) (typed FeaturePython)
  n = 0.103
FEATURE [App::DocumentObjectGroupPython] S_element005  label="S_element : 0.004"  # scripted group (container) (typed FeaturePython)
  n = 0.003
FEATURE [App::DocumentObjectGroupPython] Ca_element004  label="Ca_element : 0.225"  # scripted group (container) (typed FeaturePython)
  n = 0.225
FEATURE [App::DocumentObjectGroupPython] G4_BONE_CORTICAL_ICRP  # scripted group (container) (typed FeaturePython)
  Dunit = g/cm3
  Dvalue = 1.92
  Group = -> [H_element016,C_element016,N_element011,O_element015,Na_element003,Mg_element002,P_element003,S_element005,Ca_element004]
  conduct = 2
  density = 1
  expand = 3
  formula = G4_BONE_CORTICAL_ICRP
  name = G4_BONE_CORTICAL_ICRP
  specific = 4
FEATURE [App::DocumentObjectGroupPython] B_element001  label="B_element : 4"  # scripted group (container) (typed FeaturePython)
  n = 4
  ref = B_element
FEATURE [App::DocumentObjectGroupPython] C_element017  label="C_element : 1"  # scripted group (container) (typed FeaturePython)
  n = 1
  ref = C_element
FEATURE [App::DocumentObjectGroupPython] G4_BORON_CARBIDE  # scripted group (container) (typed FeaturePython)
  Dunit = g/cm3
  Dvalue = 2.52
  Group = -> [B_element001,C_element017]
  conduct = 2
  density = 1
  expand = 3
  formula = G4_BORON_CARBIDE
  name = G4_BORON_CARBIDE
  specific = 4
FEATURE [App::DocumentObjectGroupPython] B_element002  label="B_element : 2"  # scripted group (container) (typed FeaturePython)
  n = 2
  ref = B_element
FEATURE [App::DocumentObjectGroupPython] O_element016  label="O_element : 006"  # scripted group (container) (typed FeaturePython)
  n = 3
  ref = O_element
FEATURE [App::DocumentObjectGroupPython] G4_BORON_OXIDE  # scripted group (container) (typed FeaturePython)
  Dunit = g/cm3
  Dvalue = 1.812
  Group = -> [B_element002,O_element016]
  conduct = 2
  density = 1
  expand = 3
  formula = G4_BORON_OXIDE
  name = G4_BORON_OXIDE
  specific = 4
FEATURE [App::DocumentObjectGroupPython] H_element017  label="H_element : 0.107"  # scripted group (container) (typed FeaturePython)
  n = 0.107
FEATURE [App::DocumentObjectGroupPython] C_element018  label="C_element : 0.145"  # scripted group (container) (typed FeaturePython)
  n = 0.145
FEATURE [App::DocumentObjectGroupPython] N_element012  label="N_element : 0.022"  # scripted group (container) (typed FeaturePython)
  n = 0.022
FEATURE [App::DocumentObjectGroupPython] O_element017  label="O_element : 0.712"  # scripted group (container) (typed FeaturePython)
  n = 0.712
FEATURE [App::DocumentObjectGroupPython] Na_element004  label="Na_element : 0.004"  # scripted group (container) (typed FeaturePython)
  n = 0.002
FEATURE [App::DocumentObjectGroupPython] P_element004  label="P_element : 0.004"  # scripted group (container) (typed FeaturePython)
  n = 0.004
FEATURE [App::DocumentObjectGroupPython] S_element006  label="S_element : 0.005"  # scripted group (container) (typed FeaturePython)
  n = 0.002
FEATURE [App::DocumentObjectGroupPython] Cl_element003  label="Cl_element : 0.004"  # scripted group (container) (typed FeaturePython)
  n = 0.003
FEATURE [App::DocumentObjectGroupPython] K_element002  label="K_element : 0.003"  # scripted group (container) (typed FeaturePython)
  n = 0.003
FEATURE [App::DocumentObjectGroupPython] G4_BRAIN_ICRP  # scripted group (container) (typed FeaturePython)
  Dunit = g/cm3
  Dvalue = 1.04
  Group = -> [H_element017,C_element018,N_element012,O_element017,Na_element004,P_element004,S_element006,Cl_element003,K_element002]
  conduct = 2
  density = 1
  expand = 3
  formula = G4_BRAIN_ICRP
  name = G4_BRAIN_ICRP
  specific = 4
FEATURE [App::DocumentObjectGroupPython] C_element019  label="C_element : 4"  # scripted group (container) (typed FeaturePython)
  n = 4
  ref = C_element
FEATURE [App::DocumentObjectGroupPython] H_element018  label="H_element : 010"  # scripted group (container) (typed FeaturePython)
  n = 10
  ref = H_element
FEATURE [App::DocumentObjectGroupPython] G4_BUTANE  # scripted group (container) (typed FeaturePython)
  Dunit = g/cm3
  Dvalue = 0.00249343
  Group = -> [C_element019,H_element018]
  conduct = 2
  density = 1
  expand = 3
  formula = G4_BUTANE
  name = G4_BUTANE
  specific = 4
FEATURE [App::DocumentObjectGroupPython] C_element020  label="C_element : 008"  # scripted group (container) (typed FeaturePython)
  n = 4
  ref = C_element
FEATURE [App::DocumentObjectGroupPython] H_element019  label="H_element : 011"  # scripted group (container) (typed FeaturePython)
  n = 10
  ref = H_element
FEATURE [App::DocumentObjectGroupPython] O_element018  label="O_element : 007"  # scripted group (container) (typed FeaturePython)
  n = 1
  ref = O_element
FEATURE [App::DocumentObjectGroupPython] G4_N_BUTYL_ALCOHOL  label="G4_N-BUTYL_ALCOHOL"  # scripted group (container) (typed FeaturePython)
  Dunit = g/cm3
  Dvalue = 0.8098
  Group = -> [C_element020,H_element019,O_element018]
  conduct = 2
  density = 1
  expand = 3
  formula = G4_N-BUTYL_ALCOHOL
  name = G4_N-BUTYL_ALCOHOL
  specific = 4
FEATURE [App::DocumentObjectGroupPython] H_element020  label="H_element : 0.025"  # scripted group (container) (typed FeaturePython)
  n = 0.02468
FEATURE [App::DocumentObjectGroupPython] C_element021  label="C_element : 0.502"  # scripted group (container) (typed FeaturePython)
  n = 0.501611
FEATURE [App::DocumentObjectGroupPython] O_element019  label="O_element : 0.005"  # scripted group (container) (typed FeaturePython)
  n = 0.004527
FEATURE [App::DocumentObjectGroupPython] F_element004  label="F_element : 0.465"  # scripted group (container) (typed FeaturePython)
  n = 0.465209
FEATURE [App::DocumentObjectGroupPython] Si_element001  label="Si_element : 0.004"  # scripted group (container) (typed FeaturePython)
  n = 0.003973
FEATURE [App::DocumentObjectGroupPython] G4_C_552  label="G4_C-552"  # scripted group (container) (typed FeaturePython)
  Dunit = g/cm3
  Dvalue = 1.76
  Group = -> [H_element020,C_element021,O_element019,F_element004,Si_element001]
  conduct = 2
  density = 1
  expand = 3
  formula = G4_C-552
  name = G4_C-552
  specific = 4
FEATURE [App::DocumentObjectGroupPython] Cd_element001  label="Cd_element : 1"  # scripted group (container) (typed FeaturePython)
  n = 1
  ref = Cd_element
FEATURE [App::DocumentObjectGroupPython] Te_element001  label="Te_element : 1"  # scripted group (container) (typed FeaturePython)
  n = 1
  ref = Te_element
FEATURE [App::DocumentObjectGroupPython] G4_CADMIUM_TELLURIDE  # scripted group (container) (typed FeaturePython)
  Dunit = g/cm3
  Dvalue = 6.2
  Group = -> [Cd_element001,Te_element001]
  conduct = 2
  density = 1
  expand = 3
  formula = G4_CADMIUM_TELLURIDE
  name = G4_CADMIUM_TELLURIDE
  specific = 4
FEATURE [App::DocumentObjectGroupPython] Cd_element002  label="Cd_element : 002"  # scripted group (container) (typed FeaturePython)
  n = 1
  ref = Cd_element
FEATURE [App::DocumentObjectGroupPython] W_element001  label="W_element : 1"  # scripted group (container) (typed FeaturePython)
  n = 1
  ref = W_element
FEATURE [App::DocumentObjectGroupPython] O_element020  label="O_element : 008"  # scripted group (container) (typed FeaturePython)
  n = 4
  ref = O_element
FEATURE [App::DocumentObjectGroupPython] G4_CADMIUM_TUNGSTATE  # scripted group (container) (typed FeaturePython)
  Dunit = g/cm3
  Dvalue = 7.9
  Group = -> [Cd_element002,W_element001,O_element020]
  conduct = 2
  density = 1
  expand = 3
  formula = G4_CADMIUM_TUNGSTATE
  name = G4_CADMIUM_TUNGSTATE
  specific = 4
FEATURE [App::DocumentObjectGroupPython] Ca_element005  label="Ca_element : 1"  # scripted group (container) (typed FeaturePython)
  n = 1
  ref = Ca_element
FEATURE [App::DocumentObjectGroupPython] C_element022  label="C_element : 009"  # scripted group (container) (typed FeaturePython)
  n = 1
  ref = C_element
FEATURE [App::DocumentObjectGroupPython] O_element021  label="O_element : 009"  # scripted group (container) (typed FeaturePython)
  n = 3
  ref = O_element
FEATURE [App::DocumentObjectGroupPython] G4_CALCIUM_CARBONATE  # scripted group (container) (typed FeaturePython)
  Dunit = g/cm3
  Dvalue = 2.8
  Group = -> [Ca_element005,C_element022,O_element021]
  conduct = 2
  density = 1
  expand = 3
  formula = G4_CALCIUM_CARBONATE
  name = G4_CALCIUM_CARBONATE
  specific = 4
FEATURE [App::DocumentObjectGroupPython] Ca_element006  label="Ca_element : 002"  # scripted group (container) (typed FeaturePython)
  n = 1
  ref = Ca_element
FEATURE [App::DocumentObjectGroupPython] F_element005  label="F_element : 003"  # scripted group (container) (typed FeaturePython)
  n = 2
  ref = F_element
FEATURE [App::DocumentObjectGroupPython] G4_CALCIUM_FLUORIDE  # scripted group (container) (typed FeaturePython)
  Dunit = g/cm3
  Dvalue = 3.18
  Group = -> [Ca_element006,F_element005]
  conduct = 2
  density = 1
  expand = 3
  formula = G4_CALCIUM_FLUORIDE
  name = G4_CALCIUM_FLUORIDE
  specific = 4
FEATURE [App::DocumentObjectGroupPython] Ca_element007  label="Ca_element : 003"  # scripted group (container) (typed FeaturePython)
  n = 1
  ref = Ca_element
FEATURE [App::DocumentObjectGroupPython] O_element022  label="O_element : 010"  # scripted group (container) (typed FeaturePython)
  n = 1
  ref = O_element
FEATURE [App::DocumentObjectGroupPython] G4_CALCIUM_OXIDE  # scripted group (container) (typed FeaturePython)
  Dunit = g/cm3
  Dvalue = 3.3
  Group = -> [Ca_element007,O_element022]
  conduct = 2
  density = 1
  expand = 3
  formula = G4_CALCIUM_OXIDE
  name = G4_CALCIUM_OXIDE
  specific = 4
FEATURE [App::DocumentObjectGroupPython] Ca_element008  label="Ca_element : 004"  # scripted group (container) (typed FeaturePython)
  n = 1
  ref = Ca_element
FEATURE [App::DocumentObjectGroupPython] S_element007  label="S_element : 002"  # scripted group (container) (typed FeaturePython)
  n = 1
  ref = S_element
FEATURE [App::DocumentObjectGroupPython] O_element023  label="O_element : 011"  # scripted group (container) (typed FeaturePython)
  n = 4
  ref = O_element
FEATURE [App::DocumentObjectGroupPython] G4_CALCIUM_SULFATE  # scripted group (container) (typed FeaturePython)
  Dunit = g/cm3
  Dvalue = 2.96
  Group = -> [Ca_element008,S_element007,O_element023]
  conduct = 2
  density = 1
  expand = 3
  formula = G4_CALCIUM_SULFATE
  name = G4_CALCIUM_SULFATE
  specific = 4
FEATURE [App::DocumentObjectGroupPython] Ca_element009  label="Ca_element : 005"  # scripted group (container) (typed FeaturePython)
  n = 1
  ref = Ca_element
FEATURE [App::DocumentObjectGroupPython] W_element002  label="W_element : 002"  # scripted group (container) (typed FeaturePython)
  n = 1
  ref = W_element
FEATURE [App::DocumentObjectGroupPython] O_element024  label="O_element : 012"  # scripted group (container) (typed FeaturePython)
  n = 4
  ref = O_element
FEATURE [App::DocumentObjectGroupPython] G4_CALCIUM_TUNGSTATE  # scripted group (container) (typed FeaturePython)
  Dunit = g/cm3
  Dvalue = 6.062
  Group = -> [Ca_element009,W_element002,O_element024]
  conduct = 2
  density = 1
  expand = 3
  formula = G4_CALCIUM_TUNGSTATE
  name = G4_CALCIUM_TUNGSTATE
  specific = 4
FEATURE [App::DocumentObjectGroupPython] C_element023  label="C_element : 010"  # scripted group (container) (typed FeaturePython)
  n = 1
  ref = C_element
FEATURE [App::DocumentObjectGroupPython] O_element025  label="O_element : 013"  # scripted group (container) (typed FeaturePython)
  n = 2
  ref = O_element
FEATURE [App::DocumentObjectGroupPython] G4_CARBON_DIOXIDE  # scripted group (container) (typed FeaturePython)
  Dunit = g/cm3
  Dvalue = 0.00184212
  Group = -> [C_element023,O_element025]
  conduct = 2
  density = 1
  expand = 3
  formula = G4_CARBON_DIOXIDE
  name = G4_CARBON_DIOXIDE
  specific = 4
FEATURE [App::DocumentObjectGroupPython] C_element024  label="C_element : 011"  # scripted group (container) (typed FeaturePython)
  n = 1
  ref = C_element
FEATURE [App::DocumentObjectGroupPython] Cl_element004  label="Cl_element : 4"  # scripted group (container) (typed FeaturePython)
  n = 4
  ref = Cl_element
FEATURE [App::DocumentObjectGroupPython] G4_CARBON_TETRACHLORIDE  # scripted group (container) (typed FeaturePython)
  Dunit = g/cm3
  Dvalue = 1.594
  Group = -> [C_element024,Cl_element004]
  conduct = 2
  density = 1
  expand = 3
  formula = G4_CARBON_TETRACHLORIDE
  name = G4_CARBON_TETRACHLORIDE
  specific = 4
FEATURE [App::DocumentObjectGroupPython] C_element025  label="C_element : 012"  # scripted group (container) (typed FeaturePython)
  n = 6
  ref = C_element
FEATURE [App::DocumentObjectGroupPython] H_element021  label="H_element : 012"  # scripted group (container) (typed FeaturePython)
  n = 10
  ref = H_element
FEATURE [App::DocumentObjectGroupPython] O_element026  label="O_element : 5"  # scripted group (container) (typed FeaturePython)
  n = 5
  ref = O_element
FEATURE [App::DocumentObjectGroupPython] G4_CELLULOSE_CELLOPHANE  # scripted group (container) (typed FeaturePython)
  Dunit = g/cm3
  Dvalue = 1.42
  Group = -> [C_element025,H_element021,O_element026]
  conduct = 2
  density = 1
  expand = 3
  formula = G4_CELLULOSE_CELLOPHANE
  name = G4_CELLULOSE_CELLOPHANE
  specific = 4
FEATURE [App::DocumentObjectGroupPython] H_element022  label="H_element : 0.067"  # scripted group (container) (typed FeaturePython)
  n = 0.067125
FEATURE [App::DocumentObjectGroupPython] C_element026  label="C_element : 0.545"  # scripted group (container) (typed FeaturePython)
  n = 0.545403
FEATURE [App::DocumentObjectGroupPython] O_element027  label="O_element : 0.387"  # scripted group (container) (typed FeaturePython)
  n = 0.387472
FEATURE [App::DocumentObjectGroupPython] G4_CELLULOSE_BUTYRATE  # scripted group (container) (typed FeaturePython)
  Dunit = g/cm3
  Dvalue = 1.2
  Group = -> [H_element022,C_element026,O_element027]
  conduct = 2
  density = 1
  expand = 3
  formula = G4_CELLULOSE_BUTYRATE
  name = G4_CELLULOSE_BUTYRATE
  specific = 4
FEATURE [App::DocumentObjectGroupPython] H_element023  label="H_element : 0.029"  # scripted group (container) (typed FeaturePython)
  n = 0.029216
FEATURE [App::DocumentObjectGroupPython] C_element027  label="C_element : 0.271"  # scripted group (container) (typed FeaturePython)
  n = 0.271296
FEATURE [App::DocumentObjectGroupPython] N_element013  label="N_element : 0.121"  # scripted group (container) (typed FeaturePython)
  n = 0.121276
FEATURE [App::DocumentObjectGroupPython] O_element028  label="O_element : 0.578"  # scripted group (container) (typed FeaturePython)
  n = 0.578212
FEATURE [App::DocumentObjectGroupPython] G4_CELLULOSE_NITRATE  # scripted group (container) (typed FeaturePython)
  Dunit = g/cm3
  Dvalue = 1.49
  Group = -> [H_element023,C_element027,N_element013,O_element028]
  conduct = 2
  density = 1
  expand = 3
  formula = G4_CELLULOSE_NITRATE
  name = G4_CELLULOSE_NITRATE
  specific = 4
FEATURE [App::DocumentObjectGroupPython] H_element024  label="H_element : 0.108"  # scripted group (container) (typed FeaturePython)
  n = 0.107596
FEATURE [App::DocumentObjectGroupPython] N_element014  label="N_element : 0.001"  # scripted group (container) (typed FeaturePython)
  n = 0.0008
FEATURE [App::DocumentObjectGroupPython] O_element029  label="O_element : 0.875"  # scripted group (container) (typed FeaturePython)
  n = 0.874976
FEATURE [App::DocumentObjectGroupPython] S_element008  label="S_element : 0.015"  # scripted group (container) (typed FeaturePython)
  n = 0.014627
FEATURE [App::DocumentObjectGroupPython] Ce_element001  label="Ce_element : 0.002"  # scripted group (container) (typed FeaturePython)
  n = 0.002001
FEATURE [App::DocumentObjectGroupPython] G4_CERIC_SULFATE  # scripted group (container) (typed FeaturePython)
  Dunit = g/cm3
  Dvalue = 1.03
  Group = -> [H_element024,N_element014,O_element029,S_element008,Ce_element001]
  conduct = 2
  density = 1
  expand = 3
  formula = G4_CERIC_SULFATE
  name = G4_CERIC_SULFATE
  specific = 4
FEATURE [App::DocumentObjectGroupPython] Cs_element001  label="Cs_element : 1"  # scripted group (container) (typed FeaturePython)
  n = 1
  ref = Cs_element
FEATURE [App::DocumentObjectGroupPython] F_element006  label="F_element : 1"  # scripted group (container) (typed FeaturePython)
  n = 1
  ref = F_element
FEATURE [App::DocumentObjectGroupPython] G4_CESIUM_FLUORIDE  # scripted group (container) (typed FeaturePython)
  Dunit = g/cm3
  Dvalue = 4.115
  Group = -> [Cs_element001,F_element006]
  conduct = 2
  density = 1
  expand = 3
  formula = G4_CESIUM_FLUORIDE
  name = G4_CESIUM_FLUORIDE
  specific = 4
FEATURE [App::DocumentObjectGroupPython] Cs_element002  label="Cs_element : 002"  # scripted group (container) (typed FeaturePython)
  n = 1
  ref = Cs_element
FEATURE [App::DocumentObjectGroupPython] I_element001  label="I_element : 1"  # scripted group (container) (typed FeaturePython)
  n = 1
  ref = I_element
FEATURE [App::DocumentObjectGroupPython] G4_CESIUM_IODIDE  # scripted group (container) (typed FeaturePython)
  Dunit = g/cm3
  Dvalue = 4.51
  Group = -> [Cs_element002,I_element001]
  conduct = 2
  density = 1
  expand = 3
  formula = G4_CESIUM_IODIDE
  name = G4_CESIUM_IODIDE
  specific = 4
FEATURE [App::DocumentObjectGroupPython] C_element028  label="C_element : 013"  # scripted group (container) (typed FeaturePython)
  n = 6
  ref = C_element
FEATURE [App::DocumentObjectGroupPython] H_element025  label="H_element : 013"  # scripted group (container) (typed FeaturePython)
  n = 5
  ref = H_element
FEATURE [App::DocumentObjectGroupPython] Cl_element005  label="Cl_element : 1"  # scripted group (container) (typed FeaturePython)
  n = 1
  ref = Cl_element
FEATURE [App::DocumentObjectGroupPython] G4_CHLOROBENZENE  # scripted group (container) (typed FeaturePython)
  Dunit = g/cm3
  Dvalue = 1.1058
  Group = -> [C_element028,H_element025,Cl_element005]
  conduct = 2
  density = 1
  expand = 3
  formula = G4_CHLOROBENZENE
  name = G4_CHLOROBENZENE
  specific = 4
FEATURE [App::DocumentObjectGroupPython] C_element029  label="C_element : 014"  # scripted group (container) (typed FeaturePython)
  n = 1
  ref = C_element
FEATURE [App::DocumentObjectGroupPython] H_element026  label="H_element : 1"  # scripted group (container) (typed FeaturePython)
  n = 1
  ref = H_element
FEATURE [App::DocumentObjectGroupPython] Cl_element006  label="Cl_element : 3"  # scripted group (container) (typed FeaturePython)
  n = 3
  ref = Cl_element
FEATURE [App::DocumentObjectGroupPython] G4_CHLOROFORM  # scripted group (container) (typed FeaturePython)
  Dunit = g/cm3
  Dvalue = 1.4832
  Group = -> [C_element029,H_element026,Cl_element006]
  conduct = 2
  density = 1
  expand = 3
  formula = G4_CHLOROFORM
  name = G4_CHLOROFORM
  specific = 4
FEATURE [App::DocumentObjectGroupPython] H_element027  label="H_element : 0.010"  # scripted group (container) (typed FeaturePython)
  n = 0.01
FEATURE [App::DocumentObjectGroupPython] C_element030  label="C_element : 0.001"  # scripted group (container) (typed FeaturePython)
  n = 0.001
FEATURE [App::DocumentObjectGroupPython] O_element030  label="O_element : 0.529"  # scripted group (container) (typed FeaturePython)
  n = 0.529107
FEATURE [App::DocumentObjectGroupPython] Na_element005  label="Na_element : 0.016"  # scripted group (container) (typed FeaturePython)
  n = 0.016
FEATURE [App::DocumentObjectGroupPython] Mg_element003  label="Mg_element : 0.004"  # scripted group (container) (typed FeaturePython)
  n = 0.002
FEATURE [App::DocumentObjectGroupPython] Al_element002  label="Al_element : 0.034"  # scripted group (container) (typed FeaturePython)
  n = 0.033872
FEATURE [App::DocumentObjectGroupPython] Si_element002  label="Si_element : 0.337"  # scripted group (container) (typed FeaturePython)
  n = 0.337021
FEATURE [App::DocumentObjectGroupPython] K_element003  label="K_element : 0.013"  # scripted group (container) (typed FeaturePython)
  n = 0.013
FEATURE [App::DocumentObjectGroupPython] Ca_element010  label="Ca_element : 0.044"  # scripted group (container) (typed FeaturePython)
  n = 0.044
FEATURE [App::DocumentObjectGroupPython] Fe_element002  label="Fe_element : 0.014"  # scripted group (container) (typed FeaturePython)
  n = 0.014
FEATURE [App::DocumentObjectGroupPython] G4_CONCRETE  # scripted group (container) (typed FeaturePython)
  Dunit = g/cm3
  Dvalue = 2.3
  Group = -> [H_element027,C_element030,O_element030,Na_element005,Mg_element003,Al_element002,Si_element002,K_element003,Ca_element010,Fe_element002]
  conduct = 2
  density = 1
  expand = 3
  formula = G4_CONCRETE
  name = G4_CONCRETE
  specific = 4
FEATURE [App::DocumentObjectGroupPython] C_element031  label="C_element : 015"  # scripted group (container) (typed FeaturePython)
  n = 6
  ref = C_element
FEATURE [App::DocumentObjectGroupPython] H_element028  label="H_element : 12"  # scripted group (container) (typed FeaturePython)
  n = 12
  ref = H_element
FEATURE [App::DocumentObjectGroupPython] G4_CYCLOHEXANE  # scripted group (container) (typed FeaturePython)
  Dunit = g/cm3
  Dvalue = 0.779
  Group = -> [C_element031,H_element028]
  conduct = 2
  density = 1
  expand = 3
  formula = G4_CYCLOHEXANE
  name = G4_CYCLOHEXANE
  specific = 4
FEATURE [App::DocumentObjectGroupPython] C_element032  label="C_element : 016"  # scripted group (container) (typed FeaturePython)
  n = 6
  ref = C_element
FEATURE [App::DocumentObjectGroupPython] H_element029  label="H_element : 4"  # scripted group (container) (typed FeaturePython)
  n = 4
  ref = H_element
FEATURE [App::DocumentObjectGroupPython] Cl_element007  label="Cl_element : 2"  # scripted group (container) (typed FeaturePython)
  n = 2
  ref = Cl_element
FEATURE [App::DocumentObjectGroupPython] G4_1_2_DICHLOROBENZENE  label="G4_1.2-DICHLOROBENZENE"  # scripted group (container) (typed FeaturePython)
  Dunit = g/cm3
  Dvalue = 1.3048
  Group = -> [C_element032,H_element029,Cl_element007]
  conduct = 2
  density = 1
  expand = 3
  formula = G4_1.2-DICHLOROBENZENE
  name = G4_1.2-DICHLOROBENZENE
  specific = 4
FEATURE [App::DocumentObjectGroupPython] C_element033  label="C_element : 017"  # scripted group (container) (typed FeaturePython)
  n = 4
  ref = C_element
FEATURE [App::DocumentObjectGroupPython] H_element030  label="H_element : 8"  # scripted group (container) (typed FeaturePython)
  n = 8
  ref = H_element
FEATURE [App::DocumentObjectGroupPython] O_element031  label="O_element : 014"  # scripted group (container) (typed FeaturePython)
  n = 1
  ref = O_element
FEATURE [App::DocumentObjectGroupPython] Cl_element008  label="Cl_element : 005"  # scripted group (container) (typed FeaturePython)
  n = 2
  ref = Cl_element
FEATURE [App::DocumentObjectGroupPython] G4_DICHLORODIETHYL_ETHER  # scripted group (container) (typed FeaturePython)
  Dunit = g/cm3
  Dvalue = 1.2199
  Group = -> [C_element033,H_element030,O_element031,Cl_element008]
  conduct = 2
  density = 1
  expand = 3
  formula = G4_DICHLORODIETHYL_ETHER
  name = G4_DICHLORODIETHYL_ETHER
  specific = 4
FEATURE [App::DocumentObjectGroupPython] C_element034  label="C_element : 018"  # scripted group (container) (typed FeaturePython)
  n = 2
  ref = C_element
FEATURE [App::DocumentObjectGroupPython] H_element031  label="H_element : 014"  # scripted group (container) (typed FeaturePython)
  n = 4
  ref = H_element
FEATURE [App::DocumentObjectGroupPython] Cl_element009  label="Cl_element : 006"  # scripted group (container) (typed FeaturePython)
  n = 2
  ref = Cl_element
FEATURE [App::DocumentObjectGroupPython] G4_1_2_DICHLOROETHANE  label="G4_1.2-DICHLOROETHANE"  # scripted group (container) (typed FeaturePython)
  Dunit = g/cm3
  Dvalue = 1.2351
  Group = -> [C_element034,H_element031,Cl_element009]
  conduct = 2
  density = 1
  expand = 3
  formula = G4_1.2-DICHLOROETHANE
  name = G4_1.2-DICHLOROETHANE
  specific = 4
FEATURE [App::DocumentObjectGroupPython] C_element035  label="C_element : 019"  # scripted group (container) (typed FeaturePython)
  n = 4
  ref = C_element
FEATURE [App::DocumentObjectGroupPython] H_element032  label="H_element : 015"  # scripted group (container) (typed FeaturePython)
  n = 10
  ref = H_element
FEATURE [App::DocumentObjectGroupPython] O_element032  label="O_element : 015"  # scripted group (container) (typed FeaturePython)
  n = 1
  ref = O_element
FEATURE [App::DocumentObjectGroupPython] G4_DIETHYL_ETHER  # scripted group (container) (typed FeaturePython)
  Dunit = g/cm3
  Dvalue = 0.71378
  Group = -> [C_element035,H_element032,O_element032]
  conduct = 2
  density = 1
  expand = 3
  formula = G4_DIETHYL_ETHER
  name = G4_DIETHYL_ETHER
  specific = 4
FEATURE [App::DocumentObjectGroupPython] C_element036  label="C_element : 020"  # scripted group (container) (typed FeaturePython)
  n = 3
  ref = C_element
FEATURE [App::DocumentObjectGroupPython] H_element033  label="H_element : 016"  # scripted group (container) (typed FeaturePython)
  n = 7
  ref = H_element
FEATURE [App::DocumentObjectGroupPython] N_element015  label="N_element : 008"  # scripted group (container) (typed FeaturePython)
  n = 1
  ref = N_element
FEATURE [App::DocumentObjectGroupPython] O_element033  label="O_element : 016"  # scripted group (container) (typed FeaturePython)
  n = 1
  ref = O_element
FEATURE [App::DocumentObjectGroupPython] G4_N_N_DIMETHYL_FORMAMIDE  label="G4_N.N-DIMETHYL_FORMAMIDE"  # scripted group (container) (typed FeaturePython)
  Dunit = g/cm3
  Dvalue = 0.9487
  Group = -> [C_element036,H_element033,N_element015,O_element033]
  conduct = 2
  density = 1
  expand = 3
  formula = G4_N.N-DIMETHYL_FORMAMIDE
  name = G4_N.N-DIMETHYL_FORMAMIDE
  specific = 4
FEATURE [App::DocumentObjectGroupPython] C_element037  label="C_element : 021"  # scripted group (container) (typed FeaturePython)
  n = 2
  ref = C_element
FEATURE [App::DocumentObjectGroupPython] H_element034  label="H_element : 017"  # scripted group (container) (typed FeaturePython)
  n = 6
  ref = H_element
FEATURE [App::DocumentObjectGroupPython] O_element034  label="O_element : 017"  # scripted group (container) (typed FeaturePython)
  n = 1
  ref = O_element
FEATURE [App::DocumentObjectGroupPython] S_element009  label="S_element : 003"  # scripted group (container) (typed FeaturePython)
  n = 1
  ref = S_element
FEATURE [App::DocumentObjectGroupPython] G4_DIMETHYL_SULFOXIDE  # scripted group (container) (typed FeaturePython)
  Dunit = g/cm3
  Dvalue = 1.1014
  Group = -> [C_element037,H_element034,O_element034,S_element009]
  conduct = 2
  density = 1
  expand = 3
  formula = G4_DIMETHYL_SULFOXIDE
  name = G4_DIMETHYL_SULFOXIDE
  specific = 4
FEATURE [App::DocumentObjectGroupPython] C_element038  label="C_element : 022"  # scripted group (container) (typed FeaturePython)
  n = 2
  ref = C_element
FEATURE [App::DocumentObjectGroupPython] H_element035  label="H_element : 018"  # scripted group (container) (typed FeaturePython)
  n = 6
  ref = H_element
FEATURE [App::DocumentObjectGroupPython] G4_ETHANE  # scripted group (container) (typed FeaturePython)
  Dunit = g/cm3
  Dvalue = 0.00125324
  Group = -> [C_element038,H_element035]
  conduct = 2
  density = 1
  expand = 3
  formula = G4_ETHANE
  name = G4_ETHANE
  specific = 4
FEATURE [App::DocumentObjectGroupPython] C_element039  label="C_element : 023"  # scripted group (container) (typed FeaturePython)
  n = 2
  ref = C_element
FEATURE [App::DocumentObjectGroupPython] H_element036  label="H_element : 019"  # scripted group (container) (typed FeaturePython)
  n = 6
  ref = H_element
FEATURE [App::DocumentObjectGroupPython] O_element035  label="O_element : 018"  # scripted group (container) (typed FeaturePython)
  n = 1
  ref = O_element
FEATURE [App::DocumentObjectGroupPython] G4_ETHYL_ALCOHOL  # scripted group (container) (typed FeaturePython)
  Dunit = g/cm3
  Dvalue = 0.7893
  Group = -> [C_element039,H_element036,O_element035]
  conduct = 2
  density = 1
  expand = 3
  formula = G4_ETHYL_ALCOHOL
  name = G4_ETHYL_ALCOHOL
  specific = 4
FEATURE [App::DocumentObjectGroupPython] H_element037  label="H_element : 0.090"  # scripted group (container) (typed FeaturePython)
  n = 0.090027
FEATURE [App::DocumentObjectGroupPython] C_element040  label="C_element : 0.585"  # scripted group (container) (typed FeaturePython)
  n = 0.585182
FEATURE [App::DocumentObjectGroupPython] O_element036  label="O_element : 0.325"  # scripted group (container) (typed FeaturePython)
  n = 0.324791
FEATURE [App::DocumentObjectGroupPython] G4_ETHYL_CELLULOSE  # scripted group (container) (typed FeaturePython)
  Dunit = g/cm3
  Dvalue = 1.13
  Group = -> [H_element037,C_element040,O_element036]
  conduct = 2
  density = 1
  expand = 3
  formula = G4_ETHYL_CELLULOSE
  name = G4_ETHYL_CELLULOSE
  specific = 4
FEATURE [App::DocumentObjectGroupPython] C_element041  label="C_element : 024"  # scripted group (container) (typed FeaturePython)
  n = 2
  ref = C_element
FEATURE [App::DocumentObjectGroupPython] H_element038  label="H_element : 020"  # scripted group (container) (typed FeaturePython)
  n = 4
  ref = H_element
FEATURE [App::DocumentObjectGroupPython] G4_ETHYLENE  # scripted group (container) (typed FeaturePython)
  Dunit = g/cm3
  Dvalue = 0.00117497
  Group = -> [C_element041,H_element038]
  conduct = 2
  density = 1
  expand = 3
  formula = G4_ETHYLENE
  name = G4_ETHYLENE
  specific = 4
FEATURE [App::DocumentObjectGroupPython] H_element039  label="H_element : 0.096"  # scripted group (container) (typed FeaturePython)
  n = 0.096
FEATURE [App::DocumentObjectGroupPython] C_element042  label="C_element : 0.195"  # scripted group (container) (typed FeaturePython)
  n = 0.195
FEATURE [App::DocumentObjectGroupPython] N_element016  label="N_element : 0.057"  # scripted group (container) (typed FeaturePython)
  n = 0.057
FEATURE [App::DocumentObjectGroupPython] O_element037  label="O_element : 0.646"  # scripted group (container) (typed FeaturePython)
  n = 0.646
FEATURE [App::DocumentObjectGroupPython] Na_element006  label="Na_element : 0.017"  # scripted group (container) (typed FeaturePython)
  n = 0.001
FEATURE [App::DocumentObjectGroupPython] P_element005  label="P_element : 0.104"  # scripted group (container) (typed FeaturePython)
  n = 0.001
FEATURE [App::DocumentObjectGroupPython] S_element010  label="S_element : 0.016"  # scripted group (container) (typed FeaturePython)
  n = 0.003
FEATURE [App::DocumentObjectGroupPython] Cl_element010  label="Cl_element : 0.005"  # scripted group (container) (typed FeaturePython)
  n = 0.001
FEATURE [App::DocumentObjectGroupPython] G4_EYE_LENS_ICRP  # scripted group (container) (typed FeaturePython)
  Dunit = g/cm3
  Dvalue = 1.07
  Group = -> [H_element039,C_element042,N_element016,O_element037,Na_element006,P_element005,S_element010,Cl_element010]
  conduct = 2
  density = 1
  expand = 3
  formula = G4_EYE_LENS_ICRP
  name = G4_EYE_LENS_ICRP
  specific = 4
FEATURE [App::DocumentObjectGroupPython] Fe_element003  label="Fe_element : 2"  # scripted group (container) (typed FeaturePython)
  n = 2
  ref = Fe_element
FEATURE [App::DocumentObjectGroupPython] O_element038  label="O_element : 019"  # scripted group (container) (typed FeaturePython)
  n = 3
  ref = O_element
FEATURE [App::DocumentObjectGroupPython] G4_FERRIC_OXIDE  # scripted group (container) (typed FeaturePython)
  Dunit = g/cm3
  Dvalue = 5.2
  Group = -> [Fe_element003,O_element038]
  conduct = 2
  density = 1
  expand = 3
  formula = G4_FERRIC_OXIDE
  name = G4_FERRIC_OXIDE
  specific = 4
FEATURE [App::DocumentObjectGroupPython] Fe_element004  label="Fe_element : 1"  # scripted group (container) (typed FeaturePython)
  n = 1
  ref = Fe_element
FEATURE [App::DocumentObjectGroupPython] B_element003  label="B_element : 1"  # scripted group (container) (typed FeaturePython)
  n = 1
  ref = B_element
FEATURE [App::DocumentObjectGroupPython] G4_FERROBORIDE  # scripted group (container) (typed FeaturePython)
  Dunit = g/cm3
  Dvalue = 7.15
  Group = -> [Fe_element004,B_element003]
  conduct = 2
  density = 1
  expand = 3
  formula = G4_FERROBORIDE
  name = G4_FERROBORIDE
  specific = 4
FEATURE [App::DocumentObjectGroupPython] Fe_element005  label="Fe_element : 003"  # scripted group (container) (typed FeaturePython)
  n = 1
  ref = Fe_element
FEATURE [App::DocumentObjectGroupPython] O_element039  label="O_element : 020"  # scripted group (container) (typed FeaturePython)
  n = 1
  ref = O_element
FEATURE [App::DocumentObjectGroupPython] G4_FERROUS_OXIDE  # scripted group (container) (typed FeaturePython)
  Dunit = g/cm3
  Dvalue = 5.7
  Group = -> [Fe_element005,O_element039]
  conduct = 2
  density = 1
  expand = 3
  formula = G4_FERROUS_OXIDE
  name = G4_FERROUS_OXIDE
  specific = 4
FEATURE [App::DocumentObjectGroupPython] H_element040  label="H_element : 0.115"  # scripted group (container) (typed FeaturePython)
  n = 0.108259
FEATURE [App::DocumentObjectGroupPython] N_element017  label="N_element : 0.000"  # scripted group (container) (typed FeaturePython)
  n = 2.7e-05
FEATURE [App::DocumentObjectGroupPython] O_element040  label="O_element : 0.879"  # scripted group (container) (typed FeaturePython)
  n = 0.878636
FEATURE [App::DocumentObjectGroupPython] Na_element007  label="Na_element : 0.000"  # scripted group (container) (typed FeaturePython)
  n = 2.2e-05
FEATURE [App::DocumentObjectGroupPython] S_element011  label="S_element : 0.013"  # scripted group (container) (typed FeaturePython)
  n = 0.012968
FEATURE [App::DocumentObjectGroupPython] Cl_element011  label="Cl_element : 0.000"  # scripted group (container) (typed FeaturePython)
  n = 3.4e-05
FEATURE [App::DocumentObjectGroupPython] Fe_element006  label="Fe_element : 0.000"  # scripted group (container) (typed FeaturePython)
  n = 5.4e-05
FEATURE [App::DocumentObjectGroupPython] G4_FERROUS_SULFATE  # scripted group (container) (typed FeaturePython)
  Dunit = g/cm3
  Dvalue = 1.024
  Group = -> [H_element040,N_element017,O_element040,Na_element007,S_element011,Cl_element011,Fe_element006]
  conduct = 2
  density = 1
  expand = 3
  formula = G4_FERROUS_SULFATE
  name = G4_FERROUS_SULFATE
  specific = 4
FEATURE [App::DocumentObjectGroupPython] C_element043  label="C_element : 0.099"  # scripted group (container) (typed FeaturePython)
  n = 0.099335
FEATURE [App::DocumentObjectGroupPython] F_element007  label="F_element : 0.314"  # scripted group (container) (typed FeaturePython)
  n = 0.314247
FEATURE [App::DocumentObjectGroupPython] Cl_element012  label="Cl_element : 0.586"  # scripted group (container) (typed FeaturePython)
  n = 0.586418
FEATURE [App::DocumentObjectGroupPython] G4_FREON_12  label="G4_FREON-12"  # scripted group (container) (typed FeaturePython)
  Dunit = g/cm3
  Dvalue = 1.12
  Group = -> [C_element043,F_element007,Cl_element012]
  conduct = 2
  density = 1
  expand = 3
  formula = G4_FREON-12
  name = G4_FREON-12
  specific = 4
FEATURE [App::DocumentObjectGroupPython] C_element044  label="C_element : 0.057"  # scripted group (container) (typed FeaturePython)
  n = 0.057245
FEATURE [App::DocumentObjectGroupPython] F_element008  label="F_element : 0.181"  # scripted group (container) (typed FeaturePython)
  n = 0.181096
FEATURE [App::DocumentObjectGroupPython] Br_element001  label="Br_element : 0.762"  # scripted group (container) (typed FeaturePython)
  n = 0.761659
FEATURE [App::DocumentObjectGroupPython] G4_FREON_12B2  label="G4_FREON-12B2"  # scripted group (container) (typed FeaturePython)
  Dunit = g/cm3
  Dvalue = 1.8
  Group = -> [C_element044,F_element008,Br_element001]
  conduct = 2
  density = 1
  expand = 3
  formula = G4_FREON-12B2
  name = G4_FREON-12B2
  specific = 4
FEATURE [App::DocumentObjectGroupPython] C_element045  label="C_element : 0.115"  # scripted group (container) (typed FeaturePython)
  n = 0.114983
FEATURE [App::DocumentObjectGroupPython] F_element009  label="F_element : 0.546"  # scripted group (container) (typed FeaturePython)
  n = 0.545621
FEATURE [App::DocumentObjectGroupPython] Cl_element013  label="Cl_element : 0.339"  # scripted group (container) (typed FeaturePython)
  n = 0.339396
FEATURE [App::DocumentObjectGroupPython] G4_FREON_13  label="G4_FREON-13"  # scripted group (container) (typed FeaturePython)
  Dunit = g/cm3
  Dvalue = 0.95
  Group = -> [C_element045,F_element009,Cl_element013]
  conduct = 2
  density = 1
  expand = 3
  formula = G4_FREON-13
  name = G4_FREON-13
  specific = 4
FEATURE [App::DocumentObjectGroupPython] C_element046  label="C_element : 025"  # scripted group (container) (typed FeaturePython)
  n = 1
  ref = C_element
FEATURE [App::DocumentObjectGroupPython] F_element010  label="F_element : 3"  # scripted group (container) (typed FeaturePython)
  n = 3
  ref = F_element
FEATURE [App::DocumentObjectGroupPython] Br_element002  label="Br_element : 1"  # scripted group (container) (typed FeaturePython)
  n = 1
  ref = Br_element
FEATURE [App::DocumentObjectGroupPython] G4_FREON_13B1  label="G4_FREON-13B1"  # scripted group (container) (typed FeaturePython)
  Dunit = g/cm3
  Dvalue = 1.5
  Group = -> [C_element046,F_element010,Br_element002]
  conduct = 2
  density = 1
  expand = 3
  formula = G4_FREON-13B1
  name = G4_FREON-13B1
  specific = 4
FEATURE [App::DocumentObjectGroupPython] C_element047  label="C_element : 0.061"  # scripted group (container) (typed FeaturePython)
  n = 0.061309
FEATURE [App::DocumentObjectGroupPython] F_element011  label="F_element : 0.291"  # scripted group (container) (typed FeaturePython)
  n = 0.290924
FEATURE [App::DocumentObjectGroupPython] I_element002  label="I_element : 0.648"  # scripted group (container) (typed FeaturePython)
  n = 0.647767
FEATURE [App::DocumentObjectGroupPython] G4_FREON_13I1  label="G4_FREON-13I1"  # scripted group (container) (typed FeaturePython)
  Dunit = g/cm3
  Dvalue = 1.8
  Group = -> [C_element047,F_element011,I_element002]
  conduct = 2
  density = 1
  expand = 3
  formula = G4_FREON-13I1
  name = G4_FREON-13I1
  specific = 4
FEATURE [App::DocumentObjectGroupPython] Gd_element001  label="Gd_element : 2"  # scripted group (container) (typed FeaturePython)
  n = 2
  ref = Gd_element
FEATURE [App::DocumentObjectGroupPython] O_element041  label="O_element : 021"  # scripted group (container) (typed FeaturePython)
  n = 2
  ref = O_element
FEATURE [App::DocumentObjectGroupPython] S_element012  label="S_element : 004"  # scripted group (container) (typed FeaturePython)
  n = 1
  ref = S_element
FEATURE [App::DocumentObjectGroupPython] G4_GADOLINIUM_OXYSULFIDE  # scripted group (container) (typed FeaturePython)
  Dunit = g/cm3
  Dvalue = 7.44
  Group = -> [Gd_element001,O_element041,S_element012]
  conduct = 2
  density = 1
  expand = 3
  formula = G4_GADOLINIUM_OXYSULFIDE
  name = G4_GADOLINIUM_OXYSULFIDE
  specific = 4
FEATURE [App::DocumentObjectGroupPython] Ga_element001  label="Ga_element : 1"  # scripted group (container) (typed FeaturePython)
  n = 1
  ref = Ga_element
FEATURE [App::DocumentObjectGroupPython] As_element001  label="As_element : 1"  # scripted group (container) (typed FeaturePython)
  n = 1
  ref = As_element
FEATURE [App::DocumentObjectGroupPython] G4_GALLIUM_ARSENIDE  # scripted group (container) (typed FeaturePython)
  Dunit = g/cm3
  Dvalue = 5.31
  Group = -> [Ga_element001,As_element001]
  conduct = 2
  density = 1
  expand = 3
  formula = G4_GALLIUM_ARSENIDE
  name = G4_GALLIUM_ARSENIDE
  specific = 4
FEATURE [App::DocumentObjectGroupPython] H_element041  label="H_element : 0.081"  # scripted group (container) (typed FeaturePython)
  n = 0.08118
FEATURE [App::DocumentObjectGroupPython] C_element048  label="C_element : 0.416"  # scripted group (container) (typed FeaturePython)
  n = 0.41606
FEATURE [App::DocumentObjectGroupPython] N_element018  label="N_element : 0.111"  # scripted group (container) (typed FeaturePython)
  n = 0.11124
FEATURE [App::DocumentObjectGroupPython] O_element042  label="O_element : 0.381"  # scripted group (container) (typed FeaturePython)
  n = 0.38064
FEATURE [App::DocumentObjectGroupPython] S_element013  label="S_element : 0.011"  # scripted group (container) (typed FeaturePython)
  n = 0.01088
FEATURE [App::DocumentObjectGroupPython] G4_GEL_PHOTO_EMULSION  # scripted group (container) (typed FeaturePython)
  Dunit = g/cm3
  Dvalue = 1.2914
  Group = -> [H_element041,C_element048,N_element018,O_element042,S_element013]
  conduct = 2
  density = 1
  expand = 3
  formula = G4_GEL_PHOTO_EMULSION
  name = G4_GEL_PHOTO_EMULSION
  specific = 4
FEATURE [App::DocumentObjectGroupPython] B_element004  label="B_element : 0.040"  # scripted group (container) (typed FeaturePython)
  n = 0.0400639
FEATURE [App::DocumentObjectGroupPython] O_element043  label="O_element : 0.540"  # scripted group (container) (typed FeaturePython)
  n = 0.539561
FEATURE [App::DocumentObjectGroupPython] Na_element008  label="Na_element : 0.028"  # scripted group (container) (typed FeaturePython)
  n = 0.0281909
FEATURE [App::DocumentObjectGroupPython] Al_element003  label="Al_element : 0.012"  # scripted group (container) (typed FeaturePython)
  n = 0.011644
FEATURE [App::DocumentObjectGroupPython] Si_element003  label="Si_element : 0.377"  # scripted group (container) (typed FeaturePython)
  n = 0.377219
FEATURE [App::DocumentObjectGroupPython] K_element004  label="K_element : 0.014"  # scripted group (container) (typed FeaturePython)
  n = 0.00332099
FEATURE [App::DocumentObjectGroupPython] G4_Pyrex_Glass  # scripted group (container) (typed FeaturePython)
  Dunit = g/cm3
  Dvalue = 2.23
  Group = -> [B_element004,O_element043,Na_element008,Al_element003,Si_element003,K_element004]
  conduct = 2
  density = 1
  expand = 3
  formula = G4_Pyrex_Glass
  name = G4_Pyrex_Glass
  specific = 4
FEATURE [App::DocumentObjectGroupPython] O_element044  label="O_element : 0.156"  # scripted group (container) (typed FeaturePython)
  n = 0.156453
FEATURE [App::DocumentObjectGroupPython] Si_element004  label="Si_element : 0.081"  # scripted group (container) (typed FeaturePython)
  n = 0.080866
FEATURE [App::DocumentObjectGroupPython] Ti_element001  label="Ti_element : 0.008"  # scripted group (container) (typed FeaturePython)
  n = 0.008092
FEATURE [App::DocumentObjectGroupPython] As_element002  label="As_element : 0.003"  # scripted group (container) (typed FeaturePython)
  n = 0.002651
FEATURE [App::DocumentObjectGroupPython] Pb_element001  label="Pb_element : 0.752"  # scripted group (container) (typed FeaturePython)
  n = 0.751938
FEATURE [App::DocumentObjectGroupPython] G4_GLASS_LEAD  # scripted group (container) (typed FeaturePython)
  Dunit = g/cm3
  Dvalue = 6.22
  Group = -> [O_element044,Si_element004,Ti_element001,As_element002,Pb_element001]
  conduct = 2
  density = 1
  expand = 3
  formula = G4_GLASS_LEAD
  name = G4_GLASS_LEAD
  specific = 4
FEATURE [App::DocumentObjectGroupPython] O_element045  label="O_element : 0.460"  # scripted group (container) (typed FeaturePython)
  n = 0.4598
FEATURE [App::DocumentObjectGroupPython] Na_element009  label="Na_element : 0.096"  # scripted group (container) (typed FeaturePython)
  n = 0.0964411
FEATURE [App::DocumentObjectGroupPython] Si_element005  label="Si_element : 0.378"  # scripted group (container) (typed FeaturePython)
  n = 0.336553
FEATURE [App::DocumentObjectGroupPython] Ca_element011  label="Ca_element : 0.107"  # scripted group (container) (typed FeaturePython)
  n = 0.107205
FEATURE [App::DocumentObjectGroupPython] G4_GLASS_PLATE  # scripted group (container) (typed FeaturePython)
  Dunit = g/cm3
  Dvalue = 2.4
  Group = -> [O_element045,Na_element009,Si_element005,Ca_element011]
  conduct = 2
  density = 1
  expand = 3
  formula = G4_GLASS_PLATE
  name = G4_GLASS_PLATE
  specific = 4
FEATURE [App::DocumentObjectGroupPython] C_element049  label="C_element : 026"  # scripted group (container) (typed FeaturePython)
  n = 5
  ref = C_element
FEATURE [App::DocumentObjectGroupPython] H_element042  label="H_element : 021"  # scripted group (container) (typed FeaturePython)
  n = 10
  ref = H_element
FEATURE [App::DocumentObjectGroupPython] N_element019  label="N_element : 2"  # scripted group (container) (typed FeaturePython)
  n = 2
  ref = N_element
FEATURE [App::DocumentObjectGroupPython] O_element046  label="O_element : 022"  # scripted group (container) (typed FeaturePython)
  n = 3
  ref = O_element
FEATURE [App::DocumentObjectGroupPython] G4_GLUTAMINE  # scripted group (container) (typed FeaturePython)
  Dunit = g/cm3
  Dvalue = 1.46
  Group = -> [C_element049,H_element042,N_element019,O_element046]
  conduct = 2
  density = 1
  expand = 3
  formula = G4_GLUTAMINE
  name = G4_GLUTAMINE
  specific = 4
FEATURE [App::DocumentObjectGroupPython] C_element050  label="C_element : 027"  # scripted group (container) (typed FeaturePython)
  n = 3
  ref = C_element
FEATURE [App::DocumentObjectGroupPython] H_element043  label="H_element : 022"  # scripted group (container) (typed FeaturePython)
  n = 8
  ref = H_element
FEATURE [App::DocumentObjectGroupPython] O_element047  label="O_element : 023"  # scripted group (container) (typed FeaturePython)
  n = 3
  ref = O_element
FEATURE [App::DocumentObjectGroupPython] G4_GLYCEROL  # scripted group (container) (typed FeaturePython)
  Dunit = g/cm3
  Dvalue = 1.2613
  Group = -> [C_element050,H_element043,O_element047]
  conduct = 2
  density = 1
  expand = 3
  formula = G4_GLYCEROL
  name = G4_GLYCEROL
  specific = 4
FEATURE [App::DocumentObjectGroupPython] C_element051  label="C_element : 028"  # scripted group (container) (typed FeaturePython)
  n = 5
  ref = C_element
FEATURE [App::DocumentObjectGroupPython] H_element044  label="H_element : 023"  # scripted group (container) (typed FeaturePython)
  n = 5
  ref = H_element
FEATURE [App::DocumentObjectGroupPython] N_element020  label="N_element : 009"  # scripted group (container) (typed FeaturePython)
  n = 5
  ref = N_element
FEATURE [App::DocumentObjectGroupPython] O_element048  label="O_element : 024"  # scripted group (container) (typed FeaturePython)
  n = 1
  ref = O_element
FEATURE [App::DocumentObjectGroupPython] G4_GUANINE  # scripted group (container) (typed FeaturePython)
  Dunit = g/cm3
  Dvalue = 2.2
  Group = -> [C_element051,H_element044,N_element020,O_element048]
  conduct = 2
  density = 1
  expand = 3
  formula = G4_GUANINE
  name = G4_GUANINE
  specific = 4
FEATURE [App::DocumentObjectGroupPython] Ca_element012  label="Ca_element : 006"  # scripted group (container) (typed FeaturePython)
  n = 1
  ref = Ca_element
FEATURE [App::DocumentObjectGroupPython] S_element014  label="S_element : 005"  # scripted group (container) (typed FeaturePython)
  n = 1
  ref = S_element
FEATURE [App::DocumentObjectGroupPython] O_element049  label="O_element : 6"  # scripted group (container) (typed FeaturePython)
  n = 6
  ref = O_element
FEATURE [App::DocumentObjectGroupPython] H_element045  label="H_element : 024"  # scripted group (container) (typed FeaturePython)
  n = 4
  ref = H_element
FEATURE [App::DocumentObjectGroupPython] G4_GYPSUM  # scripted group (container) (typed FeaturePython)
  Dunit = g/cm3
  Dvalue = 2.32
  Group = -> [Ca_element012,S_element014,O_element049,H_element045]
  conduct = 2
  density = 1
  expand = 3
  formula = G4_GYPSUM
  name = G4_GYPSUM
  specific = 4
FEATURE [App::DocumentObjectGroupPython] C_element052  label="C_element : 7"  # scripted group (container) (typed FeaturePython)
  n = 7
  ref = C_element
FEATURE [App::DocumentObjectGroupPython] H_element046  label="H_element : 16"  # scripted group (container) (typed FeaturePython)
  n = 16
  ref = H_element
FEATURE [App::DocumentObjectGroupPython] G4_N_HEPTANE  label="G4_N-HEPTANE"  # scripted group (container) (typed FeaturePython)
  Dunit = g/cm3
  Dvalue = 0.68376
  Group = -> [C_element052,H_element046]
  conduct = 2
  density = 1
  expand = 3
  formula = G4_N-HEPTANE
  name = G4_N-HEPTANE
  specific = 4
FEATURE [App::DocumentObjectGroupPython] C_element053  label="C_element : 029"  # scripted group (container) (typed FeaturePython)
  n = 6
  ref = C_element
FEATURE [App::DocumentObjectGroupPython] H_element047  label="H_element : 14"  # scripted group (container) (typed FeaturePython)
  n = 14
  ref = H_element
FEATURE [App::DocumentObjectGroupPython] G4_N_HEXANE  label="G4_N-HEXANE"  # scripted group (container) (typed FeaturePython)
  Dunit = g/cm3
  Dvalue = 0.6603
  Group = -> [C_element053,H_element047]
  conduct = 2
  density = 1
  expand = 3
  formula = G4_N-HEXANE
  name = G4_N-HEXANE
  specific = 4
FEATURE [App::DocumentObjectGroupPython] C_element054  label="C_element : 22"  # scripted group (container) (typed FeaturePython)
  n = 22
  ref = C_element
FEATURE [App::DocumentObjectGroupPython] H_element048  label="H_element : 025"  # scripted group (container) (typed FeaturePython)
  n = 10
  ref = H_element
FEATURE [App::DocumentObjectGroupPython] N_element021  label="N_element : 010"  # scripted group (container) (typed FeaturePython)
  n = 2
  ref = N_element
FEATURE [App::DocumentObjectGroupPython] O_element050  label="O_element : 025"  # scripted group (container) (typed FeaturePython)
  n = 5
  ref = O_element
FEATURE [App::DocumentObjectGroupPython] G4_KAPTON  # scripted group (container) (typed FeaturePython)
  Dunit = g/cm3
  Dvalue = 1.42
  Group = -> [C_element054,H_element048,N_element021,O_element050]
  conduct = 2
  density = 1
  expand = 3
  formula = G4_KAPTON
  name = G4_KAPTON
  specific = 4
FEATURE [App::DocumentObjectGroupPython] La_element001  label="La_element : 1"  # scripted group (container) (typed FeaturePython)
  n = 1
  ref = La_element
FEATURE [App::DocumentObjectGroupPython] Br_element003  label="Br_element : 002"  # scripted group (container) (typed FeaturePython)
  n = 1
  ref = Br_element
FEATURE [App::DocumentObjectGroupPython] O_element051  label="O_element : 026"  # scripted group (container) (typed FeaturePython)
  n = 1
  ref = O_element
FEATURE [App::DocumentObjectGroupPython] G4_LANTHANUM_OXYBROMIDE  # scripted group (container) (typed FeaturePython)
  Dunit = g/cm3
  Dvalue = 6.28
  Group = -> [La_element001,Br_element003,O_element051]
  conduct = 2
  density = 1
  expand = 3
  formula = G4_LANTHANUM_OXYBROMIDE
  name = G4_LANTHANUM_OXYBROMIDE
  specific = 4
FEATURE [App::DocumentObjectGroupPython] La_element002  label="La_element : 2"  # scripted group (container) (typed FeaturePython)
  n = 2
  ref = La_element
FEATURE [App::DocumentObjectGroupPython] O_element052  label="O_element : 027"  # scripted group (container) (typed FeaturePython)
  n = 2
  ref = O_element
FEATURE [App::DocumentObjectGroupPython] S_element015  label="S_element : 006"  # scripted group (container) (typed FeaturePython)
  n = 1
  ref = S_element
FEATURE [App::DocumentObjectGroupPython] G4_LANTHANUM_OXYSULFIDE  # scripted group (container) (typed FeaturePython)
  Dunit = g/cm3
  Dvalue = 5.86
  Group = -> [La_element002,O_element052,S_element015]
  conduct = 2
  density = 1
  expand = 3
  formula = G4_LANTHANUM_OXYSULFIDE
  name = G4_LANTHANUM_OXYSULFIDE
  specific = 4
FEATURE [App::DocumentObjectGroupPython] O_element053  label="O_element : 0.072"  # scripted group (container) (typed FeaturePython)
  n = 0.071682
FEATURE [App::DocumentObjectGroupPython] Pb_element002  label="Pb_element : 0.928"  # scripted group (container) (typed FeaturePython)
  n = 0.928318
FEATURE [App::DocumentObjectGroupPython] G4_LEAD_OXIDE  # scripted group (container) (typed FeaturePython)
  Dunit = g/cm3
  Dvalue = 9.53
  Group = -> [O_element053,Pb_element002]
  conduct = 2
  density = 1
  expand = 3
  formula = G4_LEAD_OXIDE
  name = G4_LEAD_OXIDE
  specific = 4
FEATURE [App::DocumentObjectGroupPython] Li_element001  label="Li_element : 1"  # scripted group (container) (typed FeaturePython)
  n = 1
  ref = Li_element
FEATURE [App::DocumentObjectGroupPython] N_element022  label="N_element : 011"  # scripted group (container) (typed FeaturePython)
  n = 1
  ref = N_element
FEATURE [App::DocumentObjectGroupPython] H_element049  label="H_element : 026"  # scripted group (container) (typed FeaturePython)
  n = 2
  ref = H_element
FEATURE [App::DocumentObjectGroupPython] G4_LITHIUM_AMIDE  # scripted group (container) (typed FeaturePython)
  Dunit = g/cm3
  Dvalue = 1.178
  Group = -> [Li_element001,N_element022,H_element049]
  conduct = 2
  density = 1
  expand = 3
  formula = G4_LITHIUM_AMIDE
  name = G4_LITHIUM_AMIDE
  specific = 4
FEATURE [App::DocumentObjectGroupPython] Li_element002  label="Li_element : 2"  # scripted group (container) (typed FeaturePython)
  n = 2
  ref = Li_element
FEATURE [App::DocumentObjectGroupPython] C_element055  label="C_element : 030"  # scripted group (container) (typed FeaturePython)
  n = 1
  ref = C_element
FEATURE [App::DocumentObjectGroupPython] O_element054  label="O_element : 028"  # scripted group (container) (typed FeaturePython)
  n = 3
  ref = O_element
FEATURE [App::DocumentObjectGroupPython] G4_LITHIUM_CARBONATE  # scripted group (container) (typed FeaturePython)
  Dunit = g/cm3
  Dvalue = 2.11
  Group = -> [Li_element002,C_element055,O_element054]
  conduct = 2
  density = 1
  expand = 3
  formula = G4_LITHIUM_CARBONATE
  name = G4_LITHIUM_CARBONATE
  specific = 4
FEATURE [App::DocumentObjectGroupPython] Li_element003  label="Li_element : 003"  # scripted group (container) (typed FeaturePython)
  n = 1
  ref = Li_element
FEATURE [App::DocumentObjectGroupPython] F_element012  label="F_element : 004"  # scripted group (container) (typed FeaturePython)
  n = 1
  ref = F_element
FEATURE [App::DocumentObjectGroupPython] G4_LITHIUM_FLUORIDE  # scripted group (container) (typed FeaturePython)
  Dunit = g/cm3
  Dvalue = 2.635
  Group = -> [Li_element003,F_element012]
  conduct = 2
  density = 1
  expand = 3
  formula = G4_LITHIUM_FLUORIDE
  name = G4_LITHIUM_FLUORIDE
  specific = 4
FEATURE [App::DocumentObjectGroupPython] Li_element004  label="Li_element : 004"  # scripted group (container) (typed FeaturePython)
  n = 1
  ref = Li_element
FEATURE [App::DocumentObjectGroupPython] H_element050  label="H_element : 027"  # scripted group (container) (typed FeaturePython)
  n = 1
  ref = H_element
FEATURE [App::DocumentObjectGroupPython] G4_LITHIUM_HYDRIDE  # scripted group (container) (typed FeaturePython)
  Dunit = g/cm3
  Dvalue = 0.82
  Group = -> [Li_element004,H_element050]
  conduct = 2
  density = 1
  expand = 3
  formula = G4_LITHIUM_HYDRIDE
  name = G4_LITHIUM_HYDRIDE
  specific = 4
FEATURE [App::DocumentObjectGroupPython] Li_element005  label="Li_element : 005"  # scripted group (container) (typed FeaturePython)
  n = 1
  ref = Li_element
FEATURE [App::DocumentObjectGroupPython] I_element003  label="I_element : 002"  # scripted group (container) (typed FeaturePython)
  n = 1
  ref = I_element
FEATURE [App::DocumentObjectGroupPython] G4_LITHIUM_IODIDE  # scripted group (container) (typed FeaturePython)
  Dunit = g/cm3
  Dvalue = 3.494
  Group = -> [Li_element005,I_element003]
  conduct = 2
  density = 1
  expand = 3
  formula = G4_LITHIUM_IODIDE
  name = G4_LITHIUM_IODIDE
  specific = 4
FEATURE [App::DocumentObjectGroupPython] Li_element006  label="Li_element : 006"  # scripted group (container) (typed FeaturePython)
  n = 2
  ref = Li_element
FEATURE [App::DocumentObjectGroupPython] O_element055  label="O_element : 029"  # scripted group (container) (typed FeaturePython)
  n = 1
  ref = O_element
FEATURE [App::DocumentObjectGroupPython] G4_LITHIUM_OXIDE  # scripted group (container) (typed FeaturePython)
  Dunit = g/cm3
  Dvalue = 2.013
  Group = -> [Li_element006,O_element055]
  conduct = 2
  density = 1
  expand = 3
  formula = G4_LITHIUM_OXIDE
  name = G4_LITHIUM_OXIDE
  specific = 4
FEATURE [App::DocumentObjectGroupPython] Li_element007  label="Li_element : 007"  # scripted group (container) (typed FeaturePython)
  n = 2
  ref = Li_element
FEATURE [App::DocumentObjectGroupPython] B_element005  label="B_element : 005"  # scripted group (container) (typed FeaturePython)
  n = 4
  ref = B_element
FEATURE [App::DocumentObjectGroupPython] O_element056  label="O_element : 7"  # scripted group (container) (typed FeaturePython)
  n = 7
  ref = O_element
FEATURE [App::DocumentObjectGroupPython] G4_LITHIUM_TETRABORATE  # scripted group (container) (typed FeaturePython)
  Dunit = g/cm3
  Dvalue = 2.44
  Group = -> [Li_element007,B_element005,O_element056]
  conduct = 2
  density = 1
  expand = 3
  formula = G4_LITHIUM_TETRABORATE
  name = G4_LITHIUM_TETRABORATE
  specific = 4
FEATURE [App::DocumentObjectGroupPython] H_element051  label="H_element : 0.105"  # scripted group (container) (typed FeaturePython)
  n = 0.105
FEATURE [App::DocumentObjectGroupPython] C_element056  label="C_element : 0.083"  # scripted group (container) (typed FeaturePython)
  n = 0.083
FEATURE [App::DocumentObjectGroupPython] N_element023  label="N_element : 0.023"  # scripted group (container) (typed FeaturePython)
  n = 0.023
FEATURE [App::DocumentObjectGroupPython] O_element057  label="O_element : 0.779"  # scripted group (container) (typed FeaturePython)
  n = 0.779
FEATURE [App::DocumentObjectGroupPython] Na_element010  label="Na_element : 0.097"  # scripted group (container) (typed FeaturePython)
  n = 0.002
FEATURE [App::DocumentObjectGroupPython] P_element006  label="P_element : 0.105"  # scripted group (container) (typed FeaturePython)
  n = 0.001
FEATURE [App::DocumentObjectGroupPython] S_element016  label="S_element : 0.017"  # scripted group (container) (typed FeaturePython)
  n = 0.002
FEATURE [App::DocumentObjectGroupPython] Cl_element014  label="Cl_element : 0.587"  # scripted group (container) (typed FeaturePython)
  n = 0.003
FEATURE [App::DocumentObjectGroupPython] K_element005  label="K_element : 0.015"  # scripted group (container) (typed FeaturePython)
  n = 0.002
FEATURE [App::DocumentObjectGroupPython] G4_LUNG_ICRP  # scripted group (container) (typed FeaturePython)
  Dunit = g/cm3
  Dvalue = 1.04
  Group = -> [H_element051,C_element056,N_element023,O_element057,Na_element010,P_element006,S_element016,Cl_element014,K_element005]
  conduct = 2
  density = 1
  expand = 3
  formula = G4_LUNG_ICRP
  name = G4_LUNG_ICRP
  specific = 4
FEATURE [App::DocumentObjectGroupPython] H_element052  label="H_element : 0.116"  # scripted group (container) (typed FeaturePython)
  n = 0.114318
FEATURE [App::DocumentObjectGroupPython] C_element057  label="C_element : 0.656"  # scripted group (container) (typed FeaturePython)
  n = 0.655824
FEATURE [App::DocumentObjectGroupPython] O_element058  label="O_element : 0.092"  # scripted group (container) (typed FeaturePython)
  n = 0.0921831
FEATURE [App::DocumentObjectGroupPython] Mg_element004  label="Mg_element : 0.135"  # scripted group (container) (typed FeaturePython)
  n = 0.134792
FEATURE [App::DocumentObjectGroupPython] Ca_element013  label="Ca_element : 0.003"  # scripted group (container) (typed FeaturePython)
  n = 0.002883
FEATURE [App::DocumentObjectGroupPython] G4_M3_WAX  # scripted group (container) (typed FeaturePython)
  Dunit = g/cm3
  Dvalue = 1.05
  Group = -> [H_element052,C_element057,O_element058,Mg_element004,Ca_element013]
  conduct = 2
  density = 1
  expand = 3
  formula = G4_M3_WAX
  name = G4_M3_WAX
  specific = 4
FEATURE [App::DocumentObjectGroupPython] Mg_element005  label="Mg_element : 1"  # scripted group (container) (typed FeaturePython)
  n = 1
  ref = Mg_element
FEATURE [App::DocumentObjectGroupPython] C_element058  label="C_element : 031"  # scripted group (container) (typed FeaturePython)
  n = 1
  ref = C_element
FEATURE [App::DocumentObjectGroupPython] O_element059  label="O_element : 030"  # scripted group (container) (typed FeaturePython)
  n = 3
  ref = O_element
FEATURE [App::DocumentObjectGroupPython] G4_MAGNESIUM_CARBONATE  # scripted group (container) (typed FeaturePython)
  Dunit = g/cm3
  Dvalue = 2.958
  Group = -> [Mg_element005,C_element058,O_element059]
  conduct = 2
  density = 1
  expand = 3
  formula = G4_MAGNESIUM_CARBONATE
  name = G4_MAGNESIUM_CARBONATE
  specific = 4
FEATURE [App::DocumentObjectGroupPython] Mg_element006  label="Mg_element : 002"  # scripted group (container) (typed FeaturePython)
  n = 1
  ref = Mg_element
FEATURE [App::DocumentObjectGroupPython] F_element013  label="F_element : 005"  # scripted group (container) (typed FeaturePython)
  n = 2
  ref = F_element
FEATURE [App::DocumentObjectGroupPython] G4_MAGNESIUM_FLUORIDE  # scripted group (container) (typed FeaturePython)
  Dunit = g/cm3
  Dvalue = 3
  Group = -> [Mg_element006,F_element013]
  conduct = 2
  density = 1
  expand = 3
  formula = G4_MAGNESIUM_FLUORIDE
  name = G4_MAGNESIUM_FLUORIDE
  specific = 4
FEATURE [App::DocumentObjectGroupPython] Mg_element007  label="Mg_element : 003"  # scripted group (container) (typed FeaturePython)
  n = 1
  ref = Mg_element
FEATURE [App::DocumentObjectGroupPython] O_element060  label="O_element : 031"  # scripted group (container) (typed FeaturePython)
  n = 1
  ref = O_element
FEATURE [App::DocumentObjectGroupPython] G4_MAGNESIUM_OXIDE  # scripted group (container) (typed FeaturePython)
  Dunit = g/cm3
  Dvalue = 3.58
  Group = -> [Mg_element007,O_element060]
  conduct = 2
  density = 1
  expand = 3
  formula = G4_MAGNESIUM_OXIDE
  name = G4_MAGNESIUM_OXIDE
  specific = 4
FEATURE [App::DocumentObjectGroupPython] Mg_element008  label="Mg_element : 004"  # scripted group (container) (typed FeaturePython)
  n = 1
  ref = Mg_element
FEATURE [App::DocumentObjectGroupPython] B_element006  label="B_element : 006"  # scripted group (container) (typed FeaturePython)
  n = 4
  ref = B_element
FEATURE [App::DocumentObjectGroupPython] O_element061  label="O_element : 032"  # scripted group (container) (typed FeaturePython)
  n = 7
  ref = O_element
FEATURE [App::DocumentObjectGroupPython] G4_MAGNESIUM_TETRABORATE  # scripted group (container) (typed FeaturePython)
  Dunit = g/cm3
  Dvalue = 2.53
  Group = -> [Mg_element008,B_element006,O_element061]
  conduct = 2
  density = 1
  expand = 3
  formula = G4_MAGNESIUM_TETRABORATE
  name = G4_MAGNESIUM_TETRABORATE
  specific = 4
FEATURE [App::DocumentObjectGroupPython] Hg_element001  label="Hg_element : 1"  # scripted group (container) (typed FeaturePython)
  n = 1
  ref = Hg_element
FEATURE [App::DocumentObjectGroupPython] I_element004  label="I_element : 2"  # scripted group (container) (typed FeaturePython)
  n = 2
  ref = I_element
FEATURE [App::DocumentObjectGroupPython] G4_MERCURIC_IODIDE  # scripted group (container) (typed FeaturePython)
  Dunit = g/cm3
  Dvalue = 6.36
  Group = -> [Hg_element001,I_element004]
  conduct = 2
  density = 1
  expand = 3
  formula = G4_MERCURIC_IODIDE
  name = G4_MERCURIC_IODIDE
  specific = 4
FEATURE [App::DocumentObjectGroupPython] C_element059  label="C_element : 032"  # scripted group (container) (typed FeaturePython)
  n = 1
  ref = C_element
FEATURE [App::DocumentObjectGroupPython] H_element053  label="H_element : 028"  # scripted group (container) (typed FeaturePython)
  n = 4
  ref = H_element
FEATURE [App::DocumentObjectGroupPython] G4_METHANE  # scripted group (container) (typed FeaturePython)
  Dunit = g/cm3
  Dvalue = 0.000667151
  Group = -> [C_element059,H_element053]
  conduct = 2
  density = 1
  expand = 3
  formula = G4_METHANE
  name = G4_METHANE
  specific = 4
FEATURE [App::DocumentObjectGroupPython] C_element060  label="C_element : 033"  # scripted group (container) (typed FeaturePython)
  n = 1
  ref = C_element
FEATURE [App::DocumentObjectGroupPython] H_element054  label="H_element : 029"  # scripted group (container) (typed FeaturePython)
  n = 4
  ref = H_element
FEATURE [App::DocumentObjectGroupPython] O_element062  label="O_element : 033"  # scripted group (container) (typed FeaturePython)
  n = 1
  ref = O_element
FEATURE [App::DocumentObjectGroupPython] G4_METHANOL  # scripted group (container) (typed FeaturePython)
  Dunit = g/cm3
  Dvalue = 0.7914
  Group = -> [C_element060,H_element054,O_element062]
  conduct = 2
  density = 1
  expand = 3
  formula = G4_METHANOL
  name = G4_METHANOL
  specific = 4
FEATURE [App::DocumentObjectGroupPython] H_element055  label="H_element : 0.134"  # scripted group (container) (typed FeaturePython)
  n = 0.13404
FEATURE [App::DocumentObjectGroupPython] C_element061  label="C_element : 0.778"  # scripted group (container) (typed FeaturePython)
  n = 0.77796
FEATURE [App::DocumentObjectGroupPython] O_element063  label="O_element : 0.035"  # scripted group (container) (typed FeaturePython)
  n = 0.03502
FEATURE [App::DocumentObjectGroupPython] Mg_element009  label="Mg_element : 0.039"  # scripted group (container) (typed FeaturePython)
  n = 0.038594
FEATURE [App::DocumentObjectGroupPython] Ti_element002  label="Ti_element : 0.014"  # scripted group (container) (typed FeaturePython)
  n = 0.014386
FEATURE [App::DocumentObjectGroupPython] G4_MIX_D_WAX  # scripted group (container) (typed FeaturePython)
  Dunit = g/cm3
  Dvalue = 0.99
  Group = -> [H_element055,C_element061,O_element063,Mg_element009,Ti_element002]
  conduct = 2
  density = 1
  expand = 3
  formula = G4_MIX_D_WAX
  name = G4_MIX_D_WAX
  specific = 4
FEATURE [App::DocumentObjectGroupPython] H_element056  label="H_element : 0.135"  # scripted group (container) (typed FeaturePython)
  n = 0.081192
FEATURE [App::DocumentObjectGroupPython] C_element062  label="C_element : 0.583"  # scripted group (container) (typed FeaturePython)
  n = 0.583442
FEATURE [App::DocumentObjectGroupPython] N_element024  label="N_element : 0.018"  # scripted group (container) (typed FeaturePython)
  n = 0.017798
FEATURE [App::DocumentObjectGroupPython] O_element064  label="O_element : 0.186"  # scripted group (container) (typed FeaturePython)
  n = 0.186381
FEATURE [App::DocumentObjectGroupPython] Mg_element010  label="Mg_element : 0.130"  # scripted group (container) (typed FeaturePython)
  n = 0.130287
FEATURE [App::DocumentObjectGroupPython] Cl_element015  label="Cl_element : 0.588"  # scripted group (container) (typed FeaturePython)
  n = 0.0009
FEATURE [App::DocumentObjectGroupPython] G4_MS20_TISSUE  # scripted group (container) (typed FeaturePython)
  Dunit = g/cm3
  Dvalue = 1
  Group = -> [H_element056,C_element062,N_element024,O_element064,Mg_element010,Cl_element015]
  conduct = 2
  density = 1
  expand = 3
  formula = G4_MS20_TISSUE
  name = G4_MS20_TISSUE
  specific = 4
FEATURE [App::DocumentObjectGroupPython] H_element057  label="H_element : 0.136"  # scripted group (container) (typed FeaturePython)
  n = 0.102
FEATURE [App::DocumentObjectGroupPython] C_element063  label="C_element : 0.143"  # scripted group (container) (typed FeaturePython)
  n = 0.143
FEATURE [App::DocumentObjectGroupPython] N_element025  label="N_element : 0.034"  # scripted group (container) (typed FeaturePython)
  n = 0.034
FEATURE [App::DocumentObjectGroupPython] O_element065  label="O_element : 0.710"  # scripted group (container) (typed FeaturePython)
  n = 0.71
FEATURE [App::DocumentObjectGroupPython] Na_element011  label="Na_element : 0.098"  # scripted group (container) (typed FeaturePython)
  n = 0.001
FEATURE [App::DocumentObjectGroupPython] P_element007  label="P_element : 0.002"  # scripted group (container) (typed FeaturePython)
  n = 0.002
FEATURE [App::DocumentObjectGroupPython] S_element017  label="S_element : 0.018"  # scripted group (container) (typed FeaturePython)
  n = 0.003
FEATURE [App::DocumentObjectGroupPython] Cl_element016  label="Cl_element : 0.589"  # scripted group (container) (typed FeaturePython)
  n = 0.001
FEATURE [App::DocumentObjectGroupPython] K_element006  label="K_element : 0.004"  # scripted group (container) (typed FeaturePython)
  n = 0.004
FEATURE [App::DocumentObjectGroupPython] G4_MUSCLE_SKELETAL_ICRP  # scripted group (container) (typed FeaturePython)
  Dunit = g/cm3
  Dvalue = 1.05
  Group = -> [H_element057,C_element063,N_element025,O_element065,Na_element011,P_element007,S_element017,Cl_element016,K_element006]
  conduct = 2
  density = 1
  expand = 3
  formula = G4_MUSCLE_SKELETAL_ICRP
  name = G4_MUSCLE_SKELETAL_ICRP
  specific = 4
FEATURE [App::DocumentObjectGroupPython] H_element058  label="H_element : 0.137"  # scripted group (container) (typed FeaturePython)
  n = 0.102102
FEATURE [App::DocumentObjectGroupPython] C_element064  label="C_element : 0.123"  # scripted group (container) (typed FeaturePython)
  n = 0.123123
FEATURE [App::DocumentObjectGroupPython] N_element026  label="N_element : 0.756"  # scripted group (container) (typed FeaturePython)
  n = 0.035035
FEATURE [App::DocumentObjectGroupPython] O_element066  label="O_element : 0.730"  # scripted group (container) (typed FeaturePython)
  n = 0.72973
FEATURE [App::DocumentObjectGroupPython] Na_element012  label="Na_element : 0.099"  # scripted group (container) (typed FeaturePython)
  n = 0.001001
FEATURE [App::DocumentObjectGroupPython] P_element008  label="P_element : 0.106"  # scripted group (container) (typed FeaturePython)
  n = 0.002002
FEATURE [App::DocumentObjectGroupPython] S_element018  label="S_element : 0.019"  # scripted group (container) (typed FeaturePython)
  n = 0.004004
FEATURE [App::DocumentObjectGroupPython] K_element007  label="K_element : 0.016"  # scripted group (container) (typed FeaturePython)
  n = 0.003003
FEATURE [App::DocumentObjectGroupPython] G4_MUSCLE_STRIATED_ICRU  # scripted group (container) (typed FeaturePython)
  Dunit = g/cm3
  Dvalue = 1.04
  Group = -> [H_element058,C_element064,N_element026,O_element066,Na_element012,P_element008,S_element018,K_element007]
  conduct = 2
  density = 1
  expand = 3
  formula = G4_MUSCLE_STRIATED_ICRU
  name = G4_MUSCLE_STRIATED_ICRU
  specific = 4
FEATURE [App::DocumentObjectGroupPython] H_element059  label="H_element : 0.098"  # scripted group (container) (typed FeaturePython)
  n = 0.0982341
FEATURE [App::DocumentObjectGroupPython] C_element065  label="C_element : 0.156"  # scripted group (container) (typed FeaturePython)
  n = 0.156214
FEATURE [App::DocumentObjectGroupPython] N_element027  label="N_element : 0.757"  # scripted group (container) (typed FeaturePython)
  n = 0.035451
FEATURE [App::DocumentObjectGroupPython] O_element067  label="O_element : 0.880"  # scripted group (container) (typed FeaturePython)
  n = 0.710101
FEATURE [App::DocumentObjectGroupPython] G4_MUSCLE_WITH_SUCROSE  # scripted group (container) (typed FeaturePython)
  Dunit = g/cm3
  Dvalue = 1.11
  Group = -> [H_element059,C_element065,N_element027,O_element067]
  conduct = 2
  density = 1
  expand = 3
  formula = G4_MUSCLE_WITH_SUCROSE
  name = G4_MUSCLE_WITH_SUCROSE
  specific = 4
FEATURE [App::DocumentObjectGroupPython] H_element060  label="H_element : 0.138"  # scripted group (container) (typed FeaturePython)
  n = 0.101969
FEATURE [App::DocumentObjectGroupPython] C_element066  label="C_element : 0.120"  # scripted group (container) (typed FeaturePython)
  n = 0.120058
FEATURE [App::DocumentObjectGroupPython] N_element028  label="N_element : 0.758"  # scripted group (container) (typed FeaturePython)
  n = 0.035451
FEATURE [App::DocumentObjectGroupPython] O_element068  label="O_element : 0.743"  # scripted group (container) (typed FeaturePython)
  n = 0.742522
FEATURE [App::DocumentObjectGroupPython] G4_MUSCLE_WITHOUT_SUCROSE  # scripted group (container) (typed FeaturePython)
  Dunit = g/cm3
  Dvalue = 1.07
  Group = -> [H_element060,C_element066,N_element028,O_element068]
  conduct = 2
  density = 1
  expand = 3
  formula = G4_MUSCLE_WITHOUT_SUCROSE
  name = G4_MUSCLE_WITHOUT_SUCROSE
  specific = 4
FEATURE [App::DocumentObjectGroupPython] C_element067  label="C_element : 10"  # scripted group (container) (typed FeaturePython)
  n = 10
  ref = C_element
FEATURE [App::DocumentObjectGroupPython] H_element061  label="H_element : 030"  # scripted group (container) (typed FeaturePython)
  n = 8
  ref = H_element
FEATURE [App::DocumentObjectGroupPython] G4_NAPHTHALENE  # scripted group (container) (typed FeaturePython)
  Dunit = g/cm3
  Dvalue = 1.145
  Group = -> [C_element067,H_element061]
  conduct = 2
  density = 1
  expand = 3
  formula = G4_NAPHTHALENE
  name = G4_NAPHTHALENE
  specific = 4
FEATURE [App::DocumentObjectGroupPython] C_element068  label="C_element : 034"  # scripted group (container) (typed FeaturePython)
  n = 6
  ref = C_element
FEATURE [App::DocumentObjectGroupPython] H_element062  label="H_element : 031"  # scripted group (container) (typed FeaturePython)
  n = 5
  ref = H_element
FEATURE [App::DocumentObjectGroupPython] N_element029  label="N_element : 012"  # scripted group (container) (typed FeaturePython)
  n = 1
  ref = N_element
FEATURE [App::DocumentObjectGroupPython] O_element069  label="O_element : 034"  # scripted group (container) (typed FeaturePython)
  n = 2
  ref = O_element
FEATURE [App::DocumentObjectGroupPython] G4_NITROBENZENE  # scripted group (container) (typed FeaturePython)
  Dunit = g/cm3
  Dvalue = 1.19867
  Group = -> [C_element068,H_element062,N_element029,O_element069]
  conduct = 2
  density = 1
  expand = 3
  formula = G4_NITROBENZENE
  name = G4_NITROBENZENE
  specific = 4
FEATURE [App::DocumentObjectGroupPython] N_element030  label="N_element : 013"  # scripted group (container) (typed FeaturePython)
  n = 2
  ref = N_element
FEATURE [App::DocumentObjectGroupPython] O_element070  label="O_element : 035"  # scripted group (container) (typed FeaturePython)
  n = 1
  ref = O_element
FEATURE [App::DocumentObjectGroupPython] G4_NITROUS_OXIDE  # scripted group (container) (typed FeaturePython)
  Dunit = g/cm3
  Dvalue = 0.00183094
  Group = -> [N_element030,O_element070]
  conduct = 2
  density = 1
  expand = 3
  formula = G4_NITROUS_OXIDE
  name = G4_NITROUS_OXIDE
  specific = 4
FEATURE [App::DocumentObjectGroupPython] H_element063  label="H_element : 0.104"  # scripted group (container) (typed FeaturePython)
  n = 0.103509
FEATURE [App::DocumentObjectGroupPython] C_element069  label="C_element : 0.648"  # scripted group (container) (typed FeaturePython)
  n = 0.648416
FEATURE [App::DocumentObjectGroupPython] N_element031  label="N_element : 0.100"  # scripted group (container) (typed FeaturePython)
  n = 0.0995361
FEATURE [App::DocumentObjectGroupPython] O_element071  label="O_element : 0.149"  # scripted group (container) (typed FeaturePython)
  n = 0.148539
FEATURE [App::DocumentObjectGroupPython] G4_NYLON_8062  label="G4_NYLON-8062"  # scripted group (container) (typed FeaturePython)
  Dunit = g/cm3
  Dvalue = 1.08
  Group = -> [H_element063,C_element069,N_element031,O_element071]
  conduct = 2
  density = 1
  expand = 3
  formula = G4_NYLON-8062
  name = G4_NYLON-8062
  specific = 4
FEATURE [App::DocumentObjectGroupPython] C_element070  label="C_element : 035"  # scripted group (container) (typed FeaturePython)
  n = 6
  ref = C_element
FEATURE [App::DocumentObjectGroupPython] H_element064  label="H_element : 11"  # scripted group (container) (typed FeaturePython)
  n = 11
  ref = H_element
FEATURE [App::DocumentObjectGroupPython] N_element032  label="N_element : 014"  # scripted group (container) (typed FeaturePython)
  n = 1
  ref = N_element
FEATURE [App::DocumentObjectGroupPython] O_element072  label="O_element : 036"  # scripted group (container) (typed FeaturePython)
  n = 1
  ref = O_element
FEATURE [App::DocumentObjectGroupPython] G4_NYLON_6_6  label="G4_NYLON-6-6"  # scripted group (container) (typed FeaturePython)
  Dunit = g/cm3
  Dvalue = 1.14
  Group = -> [C_element070,H_element064,N_element032,O_element072]
  conduct = 2
  density = 1
  expand = 3
  formula = G4_NYLON-6-6
  name = G4_NYLON-6-6
  specific = 4
FEATURE [App::DocumentObjectGroupPython] H_element065  label="H_element : 0.139"  # scripted group (container) (typed FeaturePython)
  n = 0.107062
FEATURE [App::DocumentObjectGroupPython] C_element071  label="C_element : 0.680"  # scripted group (container) (typed FeaturePython)
  n = 0.680449
FEATURE [App::DocumentObjectGroupPython] N_element033  label="N_element : 0.099"  # scripted group (container) (typed FeaturePython)
  n = 0.099189
FEATURE [App::DocumentObjectGroupPython] O_element073  label="O_element : 0.113"  # scripted group (container) (typed FeaturePython)
  n = 0.1133
FEATURE [App::DocumentObjectGroupPython] G4_NYLON_6_10  label="G4_NYLON-6-10"  # scripted group (container) (typed FeaturePython)
  Dunit = g/cm3
  Dvalue = 1.14
  Group = -> [H_element065,C_element071,N_element033,O_element073]
  conduct = 2
  density = 1
  expand = 3
  formula = G4_NYLON-6-10
  name = G4_NYLON-6-10
  specific = 4
FEATURE [App::DocumentObjectGroupPython] H_element066  label="H_element : 0.140"  # scripted group (container) (typed FeaturePython)
  n = 0.115476
FEATURE [App::DocumentObjectGroupPython] C_element072  label="C_element : 0.721"  # scripted group (container) (typed FeaturePython)
  n = 0.720818
FEATURE [App::DocumentObjectGroupPython] N_element034  label="N_element : 0.076"  # scripted group (container) (typed FeaturePython)
  n = 0.0764169
FEATURE [App::DocumentObjectGroupPython] O_element074  label="O_element : 0.087"  # scripted group (container) (typed FeaturePython)
  n = 0.0872889
FEATURE [App::DocumentObjectGroupPython] G4_NYLON_11_RILSAN  label="G4_NYLON-11_RILSAN"  # scripted group (container) (typed FeaturePython)
  Dunit = g/cm3
  Dvalue = 1.425
  Group = -> [H_element066,C_element072,N_element034,O_element074]
  conduct = 2
  density = 1
  expand = 3
  formula = G4_NYLON-11_RILSAN
  name = G4_NYLON-11_RILSAN
  specific = 4
FEATURE [App::DocumentObjectGroupPython] C_element073  label="C_element : 8"  # scripted group (container) (typed FeaturePython)
  n = 8
  ref = C_element
FEATURE [App::DocumentObjectGroupPython] H_element067  label="H_element : 18"  # scripted group (container) (typed FeaturePython)
  n = 18
  ref = H_element
FEATURE [App::DocumentObjectGroupPython] G4_OCTANE  # scripted group (container) (typed FeaturePython)
  Dunit = g/cm3
  Dvalue = 0.7026
  Group = -> [C_element073,H_element067]
  conduct = 2
  density = 1
  expand = 3
  formula = G4_OCTANE
  name = G4_OCTANE
  specific = 4
FEATURE [App::DocumentObjectGroupPython] C_element074  label="C_element : 25"  # scripted group (container) (typed FeaturePython)
  n = 25
  ref = C_element
FEATURE [App::DocumentObjectGroupPython] H_element068  label="H_element : 52"  # scripted group (container) (typed FeaturePython)
  n = 52
  ref = H_element
FEATURE [App::DocumentObjectGroupPython] G4_PARAFFIN  # scripted group (container) (typed FeaturePython)
  Dunit = g/cm3
  Dvalue = 0.93
  Group = -> [C_element074,H_element068]
  conduct = 2
  density = 1
  expand = 3
  formula = G4_PARAFFIN
  name = G4_PARAFFIN
  specific = 4
FEATURE [App::DocumentObjectGroupPython] C_element075  label="C_element : 036"  # scripted group (container) (typed FeaturePython)
  n = 5
  ref = C_element
FEATURE [App::DocumentObjectGroupPython] H_element069  label="H_element : 032"  # scripted group (container) (typed FeaturePython)
  n = 12
  ref = H_element
FEATURE [App::DocumentObjectGroupPython] G4_N_PENTANE  label="G4_N-PENTANE"  # scripted group (container) (typed FeaturePython)
  Dunit = g/cm3
  Dvalue = 0.6262
  Group = -> [C_element075,H_element069]
  conduct = 2
  density = 1
  expand = 3
  formula = G4_N-PENTANE
  name = G4_N-PENTANE
  specific = 4
FEATURE [App::DocumentObjectGroupPython] H_element070  label="H_element : 0.014"  # scripted group (container) (typed FeaturePython)
  n = 0.0141
FEATURE [App::DocumentObjectGroupPython] C_element076  label="C_element : 0.072"  # scripted group (container) (typed FeaturePython)
  n = 0.072261
FEATURE [App::DocumentObjectGroupPython] N_element035  label="N_element : 0.019"  # scripted group (container) (typed FeaturePython)
  n = 0.01932
FEATURE [App::DocumentObjectGroupPython] O_element075  label="O_element : 0.066"  # scripted group (container) (typed FeaturePython)
  n = 0.066101
FEATURE [App::DocumentObjectGroupPython] S_element019  label="S_element : 0.020"  # scripted group (container) (typed FeaturePython)
  n = 0.00189
FEATURE [App::DocumentObjectGroupPython] Br_element004  label="Br_element : 0.349"  # scripted group (container) (typed FeaturePython)
  n = 0.349103
FEATURE [App::DocumentObjectGroupPython] Ag_element001  label="Ag_element : 0.474"  # scripted group (container) (typed FeaturePython)
  n = 0.474105
FEATURE [App::DocumentObjectGroupPython] I_element005  label="I_element : 0.003"  # scripted group (container) (typed FeaturePython)
  n = 0.00312
FEATURE [App::DocumentObjectGroupPython] G4_PHOTO_EMULSION  # scripted group (container) (typed FeaturePython)
  Dunit = g/cm3
  Dvalue = 3.815
  Group = -> [H_element070,C_element076,N_element035,O_element075,S_element019,Br_element004,Ag_element001,I_element005]
  conduct = 2
  density = 1
  expand = 3
  formula = G4_PHOTO_EMULSION
  name = G4_PHOTO_EMULSION
  specific = 4
FEATURE [App::DocumentObjectGroupPython] C_element077  label="C_element : 9"  # scripted group (container) (typed FeaturePython)
  n = 9
  ref = C_element
FEATURE [App::DocumentObjectGroupPython] H_element071  label="H_element : 033"  # scripted group (container) (typed FeaturePython)
  n = 10
  ref = H_element
FEATURE [App::DocumentObjectGroupPython] G4_PLASTIC_SC_VINYLTOLUENE  # scripted group (container) (typed FeaturePython)
  Dunit = g/cm3
  Dvalue = 1.032
  Group = -> [C_element077,H_element071]
  conduct = 2
  density = 1
  expand = 3
  formula = G4_PLASTIC_SC_VINYLTOLUENE
  name = G4_PLASTIC_SC_VINYLTOLUENE
  specific = 4
FEATURE [App::DocumentObjectGroupPython] Pu_element001  label="Pu_element : 1"  # scripted group (container) (typed FeaturePython)
  n = 1
  ref = Pu_element
FEATURE [App::DocumentObjectGroupPython] O_element076  label="O_element : 037"  # scripted group (container) (typed FeaturePython)
  n = 2
  ref = O_element
FEATURE [App::DocumentObjectGroupPython] G4_PLUTONIUM_DIOXIDE  # scripted group (container) (typed FeaturePython)
  Dunit = g/cm3
  Dvalue = 11.46
  Group = -> [Pu_element001,O_element076]
  conduct = 2
  density = 1
  expand = 3
  formula = G4_PLUTONIUM_DIOXIDE
  name = G4_PLUTONIUM_DIOXIDE
  specific = 4
FEATURE [App::DocumentObjectGroupPython] C_element078  label="C_element : 037"  # scripted group (container) (typed FeaturePython)
  n = 3
  ref = C_element
FEATURE [App::DocumentObjectGroupPython] H_element072  label="H_element : 034"  # scripted group (container) (typed FeaturePython)
  n = 3
  ref = H_element
FEATURE [App::DocumentObjectGroupPython] N_element036  label="N_element : 015"  # scripted group (container) (typed FeaturePython)
  n = 1
  ref = N_element
FEATURE [App::DocumentObjectGroupPython] G4_POLYACRYLONITRILE  # scripted group (container) (typed FeaturePython)
  Dunit = g/cm3
  Dvalue = 1.17
  Group = -> [C_element078,H_element072,N_element036]
  conduct = 2
  density = 1
  expand = 3
  formula = G4_POLYACRYLONITRILE
  name = G4_POLYACRYLONITRILE
  specific = 4
FEATURE [App::DocumentObjectGroupPython] C_element079  label="C_element : 16"  # scripted group (container) (typed FeaturePython)
  n = 16
  ref = C_element
FEATURE [App::DocumentObjectGroupPython] H_element073  label="H_element : 035"  # scripted group (container) (typed FeaturePython)
  n = 14
  ref = H_element
FEATURE [App::DocumentObjectGroupPython] O_element077  label="O_element : 038"  # scripted group (container) (typed FeaturePython)
  n = 3
  ref = O_element
FEATURE [App::DocumentObjectGroupPython] G4_POLYCARBONATE  # scripted group (container) (typed FeaturePython)
  Dunit = g/cm3
  Dvalue = 1.2
  Group = -> [C_element079,H_element073,O_element077]
  conduct = 2
  density = 1
  expand = 3
  formula = G4_POLYCARBONATE
  name = G4_POLYCARBONATE
  specific = 4
FEATURE [App::DocumentObjectGroupPython] C_element080  label="C_element : 038"  # scripted group (container) (typed FeaturePython)
  n = 8
  ref = C_element
FEATURE [App::DocumentObjectGroupPython] H_element074  label="H_element : 036"  # scripted group (container) (typed FeaturePython)
  n = 7
  ref = H_element
FEATURE [App::DocumentObjectGroupPython] Cl_element017  label="Cl_element : 007"  # scripted group (container) (typed FeaturePython)
  n = 1
  ref = Cl_element
FEATURE [App::DocumentObjectGroupPython] G4_POLYCHLOROSTYRENE  # scripted group (container) (typed FeaturePython)
  Dunit = g/cm3
  Dvalue = 1.3
  Group = -> [C_element080,H_element074,Cl_element017]
  conduct = 2
  density = 1
  expand = 3
  formula = G4_POLYCHLOROSTYRENE
  name = G4_POLYCHLOROSTYRENE
  specific = 4
FEATURE [App::DocumentObjectGroupPython] C_element081  label="C_element : 039"  # scripted group (container) (typed FeaturePython)
  n = 1
  ref = C_element
FEATURE [App::DocumentObjectGroupPython] H_element075  label="H_element : 037"  # scripted group (container) (typed FeaturePython)
  n = 2
  ref = H_element
FEATURE [App::DocumentObjectGroupPython] G4_POLYETHYLENE  # scripted group (container) (typed FeaturePython)
  Dunit = g/cm3
  Dvalue = 0.94
  Group = -> [C_element081,H_element075]
  conduct = 2
  density = 1
  expand = 3
  formula = G4_POLYETHYLENE
  name = G4_POLYETHYLENE
  specific = 4
FEATURE [App::DocumentObjectGroupPython] C_element082  label="C_element : 040"  # scripted group (container) (typed FeaturePython)
  n = 10
  ref = C_element
FEATURE [App::DocumentObjectGroupPython] H_element076  label="H_element : 038"  # scripted group (container) (typed FeaturePython)
  n = 8
  ref = H_element
FEATURE [App::DocumentObjectGroupPython] O_element078  label="O_element : 039"  # scripted group (container) (typed FeaturePython)
  n = 4
  ref = O_element
FEATURE [App::DocumentObjectGroupPython] G4_MYLAR  # scripted group (container) (typed FeaturePython)
  Dunit = g/cm3
  Dvalue = 1.4
  Group = -> [C_element082,H_element076,O_element078]
  conduct = 2
  density = 1
  expand = 3
  formula = G4_MYLAR
  name = G4_MYLAR
  specific = 4
FEATURE [App::DocumentObjectGroupPython] C_element083  label="C_element : 041"  # scripted group (container) (typed FeaturePython)
  n = 5
  ref = C_element
FEATURE [App::DocumentObjectGroupPython] H_element077  label="H_element : 039"  # scripted group (container) (typed FeaturePython)
  n = 8
  ref = H_element
FEATURE [App::DocumentObjectGroupPython] O_element079  label="O_element : 040"  # scripted group (container) (typed FeaturePython)
  n = 2
  ref = O_element
FEATURE [App::DocumentObjectGroupPython] G4_PLEXIGLASS  # scripted group (container) (typed FeaturePython)
  Dunit = g/cm3
  Dvalue = 1.19
  Group = -> [C_element083,H_element077,O_element079]
  conduct = 2
  density = 1
  expand = 3
  formula = G4_PLEXIGLASS
  name = G4_PLEXIGLASS
  specific = 4
FEATURE [App::DocumentObjectGroupPython] C_element084  label="C_element : 042"  # scripted group (container) (typed FeaturePython)
  n = 1
  ref = C_element
FEATURE [App::DocumentObjectGroupPython] H_element078  label="H_element : 040"  # scripted group (container) (typed FeaturePython)
  n = 2
  ref = H_element
FEATURE [App::DocumentObjectGroupPython] O_element080  label="O_element : 041"  # scripted group (container) (typed FeaturePython)
  n = 1
  ref = O_element
FEATURE [App::DocumentObjectGroupPython] G4_POLYOXYMETHYLENE  # scripted group (container) (typed FeaturePython)
  Dunit = g/cm3
  Dvalue = 1.425
  Group = -> [C_element084,H_element078,O_element080]
  conduct = 2
  density = 1
  expand = 3
  formula = G4_POLYOXYMETHYLENE
  name = G4_POLYOXYMETHYLENE
  specific = 4
FEATURE [App::DocumentObjectGroupPython] C_element085  label="C_element : 043"  # scripted group (container) (typed FeaturePython)
  n = 2
  ref = C_element
FEATURE [App::DocumentObjectGroupPython] H_element079  label="H_element : 041"  # scripted group (container) (typed FeaturePython)
  n = 4
  ref = H_element
FEATURE [App::DocumentObjectGroupPython] G4_POLYPROPYLENE  # scripted group (container) (typed FeaturePython)
  Dunit = g/cm3
  Dvalue = 0.9
  Group = -> [C_element085,H_element079]
  conduct = 2
  density = 1
  expand = 3
  formula = G4_POLYPROPYLENE
  name = G4_POLYPROPYLENE
  specific = 4
FEATURE [App::DocumentObjectGroupPython] C_element086  label="C_element : 044"  # scripted group (container) (typed FeaturePython)
  n = 8
  ref = C_element
FEATURE [App::DocumentObjectGroupPython] H_element080  label="H_element : 042"  # scripted group (container) (typed FeaturePython)
  n = 8
  ref = H_element
FEATURE [App::DocumentObjectGroupPython] G4_POLYSTYRENE  # scripted group (container) (typed FeaturePython)
  Dunit = g/cm3
  Dvalue = 1.06
  Group = -> [C_element086,H_element080]
  conduct = 2
  density = 1
  expand = 3
  formula = G4_POLYSTYRENE
  name = G4_POLYSTYRENE
  specific = 4
FEATURE [App::DocumentObjectGroupPython] C_element087  label="C_element : 045"  # scripted group (container) (typed FeaturePython)
  n = 2
  ref = C_element
FEATURE [App::DocumentObjectGroupPython] F_element014  label="F_element : 4"  # scripted group (container) (typed FeaturePython)
  n = 4
  ref = F_element
FEATURE [App::DocumentObjectGroupPython] G4_TEFLON  # scripted group (container) (typed FeaturePython)
  Dunit = g/cm3
  Dvalue = 2.2
  Group = -> [C_element087,F_element014]
  conduct = 2
  density = 1
  expand = 3
  formula = G4_TEFLON
  name = G4_TEFLON
  specific = 4
FEATURE [App::DocumentObjectGroupPython] C_element088  label="C_element : 046"  # scripted group (container) (typed FeaturePython)
  n = 2
  ref = C_element
FEATURE [App::DocumentObjectGroupPython] F_element015  label="F_element : 006"  # scripted group (container) (typed FeaturePython)
  n = 3
  ref = F_element
FEATURE [App::DocumentObjectGroupPython] Cl_element018  label="Cl_element : 008"  # scripted group (container) (typed FeaturePython)
  n = 1
  ref = Cl_element
FEATURE [App::DocumentObjectGroupPython] G4_POLYTRIFLUOROCHLOROETHYLENE  # scripted group (container) (typed FeaturePython)
  Dunit = g/cm3
  Dvalue = 2.1
  Group = -> [C_element088,F_element015,Cl_element018]
  conduct = 2
  density = 1
  expand = 3
  formula = G4_POLYTRIFLUOROCHLOROETHYLENE
  name = G4_POLYTRIFLUOROCHLOROETHYLENE
  specific = 4
FEATURE [App::DocumentObjectGroupPython] C_element089  label="C_element : 047"  # scripted group (container) (typed FeaturePython)
  n = 4
  ref = C_element
FEATURE [App::DocumentObjectGroupPython] H_element081  label="H_element : 043"  # scripted group (container) (typed FeaturePython)
  n = 6
  ref = H_element
FEATURE [App::DocumentObjectGroupPython] O_element081  label="O_element : 042"  # scripted group (container) (typed FeaturePython)
  n = 2
  ref = O_element
FEATURE [App::DocumentObjectGroupPython] G4_POLYVINYL_ACETATE  # scripted group (container) (typed FeaturePython)
  Dunit = g/cm3
  Dvalue = 1.19
  Group = -> [C_element089,H_element081,O_element081]
  conduct = 2
  density = 1
  expand = 3
  formula = G4_POLYVINYL_ACETATE
  name = G4_POLYVINYL_ACETATE
  specific = 4
FEATURE [App::DocumentObjectGroupPython] C_element090  label="C_element : 048"  # scripted group (container) (typed FeaturePython)
  n = 2
  ref = C_element
FEATURE [App::DocumentObjectGroupPython] H_element082  label="H_element : 044"  # scripted group (container) (typed FeaturePython)
  n = 4
  ref = H_element
FEATURE [App::DocumentObjectGroupPython] O_element082  label="O_element : 043"  # scripted group (container) (typed FeaturePython)
  n = 1
  ref = O_element
FEATURE [App::DocumentObjectGroupPython] G4_POLYVINYL_ALCOHOL  # scripted group (container) (typed FeaturePython)
  Dunit = g/cm3
  Dvalue = 1.3
  Group = -> [C_element090,H_element082,O_element082]
  conduct = 2
  density = 1
  expand = 3
  formula = G4_POLYVINYL_ALCOHOL
  name = G4_POLYVINYL_ALCOHOL
  specific = 4
FEATURE [App::DocumentObjectGroupPython] C_element091  label="C_element : 049"  # scripted group (container) (typed FeaturePython)
  n = 8
  ref = C_element
FEATURE [App::DocumentObjectGroupPython] H_element083  label="H_element : 045"  # scripted group (container) (typed FeaturePython)
  n = 14
  ref = H_element
FEATURE [App::DocumentObjectGroupPython] O_element083  label="O_element : 044"  # scripted group (container) (typed FeaturePython)
  n = 2
  ref = O_element
FEATURE [App::DocumentObjectGroupPython] G4_POLYVINYL_BUTYRAL  # scripted group (container) (typed FeaturePython)
  Dunit = g/cm3
  Dvalue = 1.12
  Group = -> [C_element091,H_element083,O_element083]
  conduct = 2
  density = 1
  expand = 3
  formula = G4_POLYVINYL_BUTYRAL
  name = G4_POLYVINYL_BUTYRAL
  specific = 4
FEATURE [App::DocumentObjectGroupPython] C_element092  label="C_element : 050"  # scripted group (container) (typed FeaturePython)
  n = 2
  ref = C_element
FEATURE [App::DocumentObjectGroupPython] H_element084  label="H_element : 046"  # scripted group (container) (typed FeaturePython)
  n = 3
  ref = H_element
FEATURE [App::DocumentObjectGroupPython] Cl_element019  label="Cl_element : 009"  # scripted group (container) (typed FeaturePython)
  n = 1
  ref = Cl_element
FEATURE [App::DocumentObjectGroupPython] G4_POLYVINYL_CHLORIDE  # scripted group (container) (typed FeaturePython)
  Dunit = g/cm3
  Dvalue = 1.3
  Group = -> [C_element092,H_element084,Cl_element019]
  conduct = 2
  density = 1
  expand = 3
  formula = G4_POLYVINYL_CHLORIDE
  name = G4_POLYVINYL_CHLORIDE
  specific = 4
FEATURE [App::DocumentObjectGroupPython] C_element093  label="C_element : 051"  # scripted group (container) (typed FeaturePython)
  n = 2
  ref = C_element
FEATURE [App::DocumentObjectGroupPython] H_element085  label="H_element : 047"  # scripted group (container) (typed FeaturePython)
  n = 2
  ref = H_element
FEATURE [App::DocumentObjectGroupPython] Cl_element020  label="Cl_element : 010"  # scripted group (container) (typed FeaturePython)
  n = 2
  ref = Cl_element
FEATURE [App::DocumentObjectGroupPython] G4_POLYVINYLIDENE_CHLORIDE  # scripted group (container) (typed FeaturePython)
  Dunit = g/cm3
  Dvalue = 1.7
  Group = -> [C_element093,H_element085,Cl_element020]
  conduct = 2
  density = 1
  expand = 3
  formula = G4_POLYVINYLIDENE_CHLORIDE
  name = G4_POLYVINYLIDENE_CHLORIDE
  specific = 4
FEATURE [App::DocumentObjectGroupPython] C_element094  label="C_element : 052"  # scripted group (container) (typed FeaturePython)
  n = 2
  ref = C_element
FEATURE [App::DocumentObjectGroupPython] H_element086  label="H_element : 048"  # scripted group (container) (typed FeaturePython)
  n = 2
  ref = H_element
FEATURE [App::DocumentObjectGroupPython] F_element016  label="F_element : 007"  # scripted group (container) (typed FeaturePython)
  n = 2
  ref = F_element
FEATURE [App::DocumentObjectGroupPython] G4_POLYVINYLIDENE_FLUORIDE  # scripted group (container) (typed FeaturePython)
  Dunit = g/cm3
  Dvalue = 1.76
  Group = -> [C_element094,H_element086,F_element016]
  conduct = 2
  density = 1
  expand = 3
  formula = G4_POLYVINYLIDENE_FLUORIDE
  name = G4_POLYVINYLIDENE_FLUORIDE
  specific = 4
FEATURE [App::DocumentObjectGroupPython] C_element095  label="C_element : 053"  # scripted group (container) (typed FeaturePython)
  n = 6
  ref = C_element
FEATURE [App::DocumentObjectGroupPython] H_element087  label="H_element : 9"  # scripted group (container) (typed FeaturePython)
  n = 9
  ref = H_element
FEATURE [App::DocumentObjectGroupPython] N_element037  label="N_element : 016"  # scripted group (container) (typed FeaturePython)
  n = 1
  ref = N_element
FEATURE [App::DocumentObjectGroupPython] O_element084  label="O_element : 045"  # scripted group (container) (typed FeaturePython)
  n = 1
  ref = O_element
FEATURE [App::DocumentObjectGroupPython] G4_POLYVINYL_PYRROLIDONE  # scripted group (container) (typed FeaturePython)
  Dunit = g/cm3
  Dvalue = 1.25
  Group = -> [C_element095,H_element087,N_element037,O_element084]
  conduct = 2
  density = 1
  expand = 3
  formula = G4_POLYVINYL_PYRROLIDONE
  name = G4_POLYVINYL_PYRROLIDONE
  specific = 4
FEATURE [App::DocumentObjectGroupPython] K_element008  label="K_element : 1"  # scripted group (container) (typed FeaturePython)
  n = 1
  ref = K_element
FEATURE [App::DocumentObjectGroupPython] I_element006  label="I_element : 003"  # scripted group (container) (typed FeaturePython)
  n = 1
  ref = I_element
FEATURE [App::DocumentObjectGroupPython] G4_POTASSIUM_IODIDE  # scripted group (container) (typed FeaturePython)
  Dunit = g/cm3
  Dvalue = 3.13
  Group = -> [K_element008,I_element006]
  conduct = 2
  density = 1
  expand = 3
  formula = G4_POTASSIUM_IODIDE
  name = G4_POTASSIUM_IODIDE
  specific = 4
FEATURE [App::DocumentObjectGroupPython] K_element009  label="K_element : 2"  # scripted group (container) (typed FeaturePython)
  n = 2
  ref = K_element
FEATURE [App::DocumentObjectGroupPython] O_element085  label="O_element : 046"  # scripted group (container) (typed FeaturePython)
  n = 1
  ref = O_element
FEATURE [App::DocumentObjectGroupPython] G4_POTASSIUM_OXIDE  # scripted group (container) (typed FeaturePython)
  Dunit = g/cm3
  Dvalue = 2.32
  Group = -> [K_element009,O_element085]
  conduct = 2
  density = 1
  expand = 3
  formula = G4_POTASSIUM_OXIDE
  name = G4_POTASSIUM_OXIDE
  specific = 4
FEATURE [App::DocumentObjectGroupPython] C_element096  label="C_element : 054"  # scripted group (container) (typed FeaturePython)
  n = 3
  ref = C_element
FEATURE [App::DocumentObjectGroupPython] H_element088  label="H_element : 049"  # scripted group (container) (typed FeaturePython)
  n = 8
  ref = H_element
FEATURE [App::DocumentObjectGroupPython] G4_PROPANE  # scripted group (container) (typed FeaturePython)
  Dunit = g/cm3
  Dvalue = 0.00187939
  Group = -> [C_element096,H_element088]
  conduct = 2
  density = 1
  expand = 3
  formula = G4_PROPANE
  name = G4_PROPANE
  specific = 4
FEATURE [App::DocumentObjectGroupPython] C_element097  label="C_element : 055"  # scripted group (container) (typed FeaturePython)
  n = 3
  ref = C_element
FEATURE [App::DocumentObjectGroupPython] H_element089  label="H_element : 050"  # scripted group (container) (typed FeaturePython)
  n = 8
  ref = H_element
FEATURE [App::DocumentObjectGroupPython] G4_lPROPANE  # scripted group (container) (typed FeaturePython)
  Dunit = g/cm3
  Dvalue = 0.43
  Group = -> [C_element097,H_element089]
  conduct = 2
  density = 1
  expand = 3
  formula = G4_lPROPANE
  name = G4_lPROPANE
  specific = 4
FEATURE [App::DocumentObjectGroupPython] C_element098  label="C_element : 056"  # scripted group (container) (typed FeaturePython)
  n = 3
  ref = C_element
FEATURE [App::DocumentObjectGroupPython] H_element090  label="H_element : 051"  # scripted group (container) (typed FeaturePython)
  n = 8
  ref = H_element
FEATURE [App::DocumentObjectGroupPython] O_element086  label="O_element : 047"  # scripted group (container) (typed FeaturePython)
  n = 1
  ref = O_element
FEATURE [App::DocumentObjectGroupPython] G4_N_PROPYL_ALCOHOL  label="G4_N-PROPYL_ALCOHOL"  # scripted group (container) (typed FeaturePython)
  Dunit = g/cm3
  Dvalue = 0.8035
  Group = -> [C_element098,H_element090,O_element086]
  conduct = 2
  density = 1
  expand = 3
  formula = G4_N-PROPYL_ALCOHOL
  name = G4_N-PROPYL_ALCOHOL
  specific = 4
FEATURE [App::DocumentObjectGroupPython] C_element099  label="C_element : 057"  # scripted group (container) (typed FeaturePython)
  n = 5
  ref = C_element
FEATURE [App::DocumentObjectGroupPython] H_element091  label="H_element : 052"  # scripted group (container) (typed FeaturePython)
  n = 5
  ref = H_element
FEATURE [App::DocumentObjectGroupPython] N_element038  label="N_element : 017"  # scripted group (container) (typed FeaturePython)
  n = 1
  ref = N_element
FEATURE [App::DocumentObjectGroupPython] G4_PYRIDINE  # scripted group (container) (typed FeaturePython)
  Dunit = g/cm3
  Dvalue = 0.9819
  Group = -> [C_element099,H_element091,N_element038]
  conduct = 2
  density = 1
  expand = 3
  formula = G4_PYRIDINE
  name = G4_PYRIDINE
  specific = 4
FEATURE [App::DocumentObjectGroupPython] H_element092  label="H_element : 0.144"  # scripted group (container) (typed FeaturePython)
  n = 0.143711
FEATURE [App::DocumentObjectGroupPython] C_element100  label="C_element : 0.856"  # scripted group (container) (typed FeaturePython)
  n = 0.856289
FEATURE [App::DocumentObjectGroupPython] G4_RUBBER_BUTYL  # scripted group (container) (typed FeaturePython)
  Dunit = g/cm3
  Dvalue = 0.92
  Group = -> [H_element092,C_element100]
  conduct = 2
  density = 1
  expand = 3
  formula = G4_RUBBER_BUTYL
  name = G4_RUBBER_BUTYL
  specific = 4
FEATURE [App::DocumentObjectGroupPython] H_element093  label="H_element : 0.118"  # scripted group (container) (typed FeaturePython)
  n = 0.118371
FEATURE [App::DocumentObjectGroupPython] C_element101  label="C_element : 0.882"  # scripted group (container) (typed FeaturePython)
  n = 0.881629
FEATURE [App::DocumentObjectGroupPython] G4_RUBBER_NATURAL  # scripted group (container) (typed FeaturePython)
  Dunit = g/cm3
  Dvalue = 0.92
  Group = -> [H_element093,C_element101]
  conduct = 2
  density = 1
  expand = 3
  formula = G4_RUBBER_NATURAL
  name = G4_RUBBER_NATURAL
  specific = 4
FEATURE [App::DocumentObjectGroupPython] H_element094  label="H_element : 0.145"  # scripted group (container) (typed FeaturePython)
  n = 0.05692
FEATURE [App::DocumentObjectGroupPython] C_element102  label="C_element : 0.543"  # scripted group (container) (typed FeaturePython)
  n = 0.542646
FEATURE [App::DocumentObjectGroupPython] Cl_element021  label="Cl_element : 0.400"  # scripted group (container) (typed FeaturePython)
  n = 0.400434
FEATURE [App::DocumentObjectGroupPython] G4_RUBBER_NEOPRENE  # scripted group (container) (typed FeaturePython)
  Dunit = g/cm3
  Dvalue = 1.23
  Group = -> [H_element094,C_element102,Cl_element021]
  conduct = 2
  density = 1
  expand = 3
  formula = G4_RUBBER_NEOPRENE
  name = G4_RUBBER_NEOPRENE
  specific = 4
FEATURE [App::DocumentObjectGroupPython] Si_element006  label="Si_element : 1"  # scripted group (container) (typed FeaturePython)
  n = 1
  ref = Si_element
FEATURE [App::DocumentObjectGroupPython] O_element087  label="O_element : 048"  # scripted group (container) (typed FeaturePython)
  n = 2
  ref = O_element
FEATURE [App::DocumentObjectGroupPython] G4_SILICON_DIOXIDE  # scripted group (container) (typed FeaturePython)
  Dunit = g/cm3
  Dvalue = 2.32
  Group = -> [Si_element006,O_element087]
  conduct = 2
  density = 1
  expand = 3
  formula = G4_SILICON_DIOXIDE
  name = G4_SILICON_DIOXIDE
  specific = 4
FEATURE [App::DocumentObjectGroupPython] Ag_element002  label="Ag_element : 1"  # scripted group (container) (typed FeaturePython)
  n = 1
  ref = Ag_element
FEATURE [App::DocumentObjectGroupPython] Br_element005  label="Br_element : 003"  # scripted group (container) (typed FeaturePython)
  n = 1
  ref = Br_element
FEATURE [App::DocumentObjectGroupPython] G4_SILVER_BROMIDE  # scripted group (container) (typed FeaturePython)
  Dunit = g/cm3
  Dvalue = 6.473
  Group = -> [Ag_element002,Br_element005]
  conduct = 2
  density = 1
  expand = 3
  formula = G4_SILVER_BROMIDE
  name = G4_SILVER_BROMIDE
  specific = 4
FEATURE [App::DocumentObjectGroupPython] Ag_element003  label="Ag_element : 002"  # scripted group (container) (typed FeaturePython)
  n = 1
  ref = Ag_element
FEATURE [App::DocumentObjectGroupPython] Cl_element022  label="Cl_element : 011"  # scripted group (container) (typed FeaturePython)
  n = 1
  ref = Cl_element
FEATURE [App::DocumentObjectGroupPython] G4_SILVER_CHLORIDE  # scripted group (container) (typed FeaturePython)
  Dunit = g/cm3
  Dvalue = 5.56
  Group = -> [Ag_element003,Cl_element022]
  conduct = 2
  density = 1
  expand = 3
  formula = G4_SILVER_CHLORIDE
  name = G4_SILVER_CHLORIDE
  specific = 4
FEATURE [App::DocumentObjectGroupPython] Br_element006  label="Br_element : 0.423"  # scripted group (container) (typed FeaturePython)
  n = 0.422895
FEATURE [App::DocumentObjectGroupPython] Ag_element004  label="Ag_element : 0.574"  # scripted group (container) (typed FeaturePython)
  n = 0.573748
FEATURE [App::DocumentObjectGroupPython] I_element007  label="I_element : 0.649"  # scripted group (container) (typed FeaturePython)
  n = 0.003357
FEATURE [App::DocumentObjectGroupPython] G4_SILVER_HALIDES  # scripted group (container) (typed FeaturePython)
  Dunit = g/cm3
  Dvalue = 6.47
  Group = -> [Br_element006,Ag_element004,I_element007]
  conduct = 2
  density = 1
  expand = 3
  formula = G4_SILVER_HALIDES
  name = G4_SILVER_HALIDES
  specific = 4
FEATURE [App::DocumentObjectGroupPython] Ag_element005  label="Ag_element : 003"  # scripted group (container) (typed FeaturePython)
  n = 1
  ref = Ag_element
FEATURE [App::DocumentObjectGroupPython] I_element008  label="I_element : 004"  # scripted group (container) (typed FeaturePython)
  n = 1
  ref = I_element
FEATURE [App::DocumentObjectGroupPython] G4_SILVER_IODIDE  # scripted group (container) (typed FeaturePython)
  Dunit = g/cm3
  Dvalue = 6.01
  Group = -> [Ag_element005,I_element008]
  conduct = 2
  density = 1
  expand = 3
  formula = G4_SILVER_IODIDE
  name = G4_SILVER_IODIDE
  specific = 4
FEATURE [App::DocumentObjectGroupPython] H_element095  label="H_element : 0.100"  # scripted group (container) (typed FeaturePython)
  n = 0.1
FEATURE [App::DocumentObjectGroupPython] C_element103  label="C_element : 0.204"  # scripted group (container) (typed FeaturePython)
  n = 0.204
FEATURE [App::DocumentObjectGroupPython] N_element039  label="N_element : 0.759"  # scripted group (container) (typed FeaturePython)
  n = 0.042
FEATURE [App::DocumentObjectGroupPython] O_element088  label="O_element : 0.645"  # scripted group (container) (typed FeaturePython)
  n = 0.645
FEATURE [App::DocumentObjectGroupPython] Na_element013  label="Na_element : 0.100"  # scripted group (container) (typed FeaturePython)
  n = 0.002
FEATURE [App::DocumentObjectGroupPython] P_element009  label="P_element : 0.107"  # scripted group (container) (typed FeaturePython)
  n = 0.001
FEATURE [App::DocumentObjectGroupPython] S_element020  label="S_element : 0.021"  # scripted group (container) (typed FeaturePython)
  n = 0.002
FEATURE [App::DocumentObjectGroupPython] Cl_element023  label="Cl_element : 0.590"  # scripted group (container) (typed FeaturePython)
  n = 0.003
FEATURE [App::DocumentObjectGroupPython] K_element010  label="K_element : 0.001"  # scripted group (container) (typed FeaturePython)
  n = 0.001
FEATURE [App::DocumentObjectGroupPython] G4_SKIN_ICRP  # scripted group (container) (typed FeaturePython)
  Dunit = g/cm3
  Dvalue = 1.09
  Group = -> [H_element095,C_element103,N_element039,O_element088,Na_element013,P_element009,S_element020,Cl_element023,K_element010]
  conduct = 2
  density = 1
  expand = 3
  formula = G4_SKIN_ICRP
  name = G4_SKIN_ICRP
  specific = 4
FEATURE [App::DocumentObjectGroupPython] Na_element014  label="Na_element : 2"  # scripted group (container) (typed FeaturePython)
  n = 2
  ref = Na_element
FEATURE [App::DocumentObjectGroupPython] C_element104  label="C_element : 058"  # scripted group (container) (typed FeaturePython)
  n = 1
  ref = C_element
FEATURE [App::DocumentObjectGroupPython] O_element089  label="O_element : 049"  # scripted group (container) (typed FeaturePython)
  n = 3
  ref = O_element
FEATURE [App::DocumentObjectGroupPython] G4_SODIUM_CARBONATE  # scripted group (container) (typed FeaturePython)
  Dunit = g/cm3
  Dvalue = 2.532
  Group = -> [Na_element014,C_element104,O_element089]
  conduct = 2
  density = 1
  expand = 3
  formula = G4_SODIUM_CARBONATE
  name = G4_SODIUM_CARBONATE
  specific = 4
FEATURE [App::DocumentObjectGroupPython] Na_element015  label="Na_element : 1"  # scripted group (container) (typed FeaturePython)
  n = 1
  ref = Na_element
FEATURE [App::DocumentObjectGroupPython] I_element009  label="I_element : 005"  # scripted group (container) (typed FeaturePython)
  n = 1
  ref = I_element
FEATURE [App::DocumentObjectGroupPython] G4_SODIUM_IODIDE  # scripted group (container) (typed FeaturePython)
  Dunit = g/cm3
  Dvalue = 3.667
  Group = -> [Na_element015,I_element009]
  conduct = 2
  density = 1
  expand = 3
  formula = G4_SODIUM_IODIDE
  name = G4_SODIUM_IODIDE
  specific = 4
FEATURE [App::DocumentObjectGroupPython] Na_element016  label="Na_element : 003"  # scripted group (container) (typed FeaturePython)
  n = 2
  ref = Na_element
FEATURE [App::DocumentObjectGroupPython] O_element090  label="O_element : 050"  # scripted group (container) (typed FeaturePython)
  n = 1
  ref = O_element
FEATURE [App::DocumentObjectGroupPython] G4_SODIUM_MONOXIDE  # scripted group (container) (typed FeaturePython)
  Dunit = g/cm3
  Dvalue = 2.27
  Group = -> [Na_element016,O_element090]
  conduct = 2
  density = 1
  expand = 3
  formula = G4_SODIUM_MONOXIDE
  name = G4_SODIUM_MONOXIDE
  specific = 4
FEATURE [App::DocumentObjectGroupPython] Na_element017  label="Na_element : 004"  # scripted group (container) (typed FeaturePython)
  n = 1
  ref = Na_element
FEATURE [App::DocumentObjectGroupPython] N_element040  label="N_element : 018"  # scripted group (container) (typed FeaturePython)
  n = 1
  ref = N_element
FEATURE [App::DocumentObjectGroupPython] O_element091  label="O_element : 051"  # scripted group (container) (typed FeaturePython)
  n = 3
  ref = O_element
FEATURE [App::DocumentObjectGroupPython] G4_SODIUM_NITRATE  # scripted group (container) (typed FeaturePython)
  Dunit = g/cm3
  Dvalue = 2.261
  Group = -> [Na_element017,N_element040,O_element091]
  conduct = 2
  density = 1
  expand = 3
  formula = G4_SODIUM_NITRATE
  name = G4_SODIUM_NITRATE
  specific = 4
FEATURE [App::DocumentObjectGroupPython] C_element105  label="C_element : 059"  # scripted group (container) (typed FeaturePython)
  n = 14
  ref = C_element
FEATURE [App::DocumentObjectGroupPython] H_element096  label="H_element : 053"  # scripted group (container) (typed FeaturePython)
  n = 12
  ref = H_element
FEATURE [App::DocumentObjectGroupPython] G4_STILBENE  # scripted group (container) (typed FeaturePython)
  Dunit = g/cm3
  Dvalue = 0.9707
  Group = -> [C_element105,H_element096]
  conduct = 2
  density = 1
  expand = 3
  formula = G4_STILBENE
  name = G4_STILBENE
  specific = 4
FEATURE [App::DocumentObjectGroupPython] C_element106  label="C_element : 12"  # scripted group (container) (typed FeaturePython)
  n = 12
  ref = C_element
FEATURE [App::DocumentObjectGroupPython] H_element097  label="H_element : 22"  # scripted group (container) (typed FeaturePython)
  n = 22
  ref = H_element
FEATURE [App::DocumentObjectGroupPython] O_element092  label="O_element : 11"  # scripted group (container) (typed FeaturePython)
  n = 11
  ref = O_element
FEATURE [App::DocumentObjectGroupPython] G4_SUCROSE  # scripted group (container) (typed FeaturePython)
  Dunit = g/cm3
  Dvalue = 1.5805
  Group = -> [C_element106,H_element097,O_element092]
  conduct = 2
  density = 1
  expand = 3
  formula = G4_SUCROSE
  name = G4_SUCROSE
  specific = 4
FEATURE [App::DocumentObjectGroupPython] C_element107  label="C_element : 18"  # scripted group (container) (typed FeaturePython)
  n = 18
  ref = C_element
FEATURE [App::DocumentObjectGroupPython] H_element098  label="H_element : 054"  # scripted group (container) (typed FeaturePython)
  n = 14
  ref = H_element
FEATURE [App::DocumentObjectGroupPython] G4_TERPHENYL  # scripted group (container) (typed FeaturePython)
  Dunit = g/cm3
  Dvalue = 1.24
  Group = -> [C_element107,H_element098]
  conduct = 2
  density = 1
  expand = 3
  formula = G4_TERPHENYL
  name = G4_TERPHENYL
  specific = 4
FEATURE [App::DocumentObjectGroupPython] H_element099  label="H_element : 0.146"  # scripted group (container) (typed FeaturePython)
  n = 0.106
FEATURE [App::DocumentObjectGroupPython] C_element108  label="C_element : 0.883"  # scripted group (container) (typed FeaturePython)
  n = 0.099
FEATURE [App::DocumentObjectGroupPython] N_element041  label="N_element : 0.020"  # scripted group (container) (typed FeaturePython)
  n = 0.02
FEATURE [App::DocumentObjectGroupPython] O_element093  label="O_element : 0.766"  # scripted group (container) (typed FeaturePython)
  n = 0.766
FEATURE [App::DocumentObjectGroupPython] Na_element018  label="Na_element : 0.101"  # scripted group (container) (typed FeaturePython)
  n = 0.002
FEATURE [App::DocumentObjectGroupPython] P_element010  label="P_element : 0.108"  # scripted group (container) (typed FeaturePython)
  n = 0.001
FEATURE [App::DocumentObjectGroupPython] S_element021  label="S_element : 0.022"  # scripted group (container) (typed FeaturePython)
  n = 0.002
FEATURE [App::DocumentObjectGroupPython] Cl_element024  label="Cl_element : 0.002"  # scripted group (container) (typed FeaturePython)
  n = 0.002
FEATURE [App::DocumentObjectGroupPython] K_element011  label="K_element : 0.017"  # scripted group (container) (typed FeaturePython)
  n = 0.002
FEATURE [App::DocumentObjectGroupPython] G4_TESTIS_ICRP  # scripted group (container) (typed FeaturePython)
  Dunit = g/cm3
  Dvalue = 1.04
  Group = -> [H_element099,C_element108,N_element041,O_element093,Na_element018,P_element010,S_element021,Cl_element024,K_element011]
  conduct = 2
  density = 1
  expand = 3
  formula = G4_TESTIS_ICRP
  name = G4_TESTIS_ICRP
  specific = 4
FEATURE [App::DocumentObjectGroupPython] C_element109  label="C_element : 060"  # scripted group (container) (typed FeaturePython)
  n = 2
  ref = C_element
FEATURE [App::DocumentObjectGroupPython] Cl_element025  label="Cl_element : 012"  # scripted group (container) (typed FeaturePython)
  n = 4
  ref = Cl_element
FEATURE [App::DocumentObjectGroupPython] G4_TETRACHLOROETHYLENE  # scripted group (container) (typed FeaturePython)
  Dunit = g/cm3
  Dvalue = 1.625
  Group = -> [C_element109,Cl_element025]
  conduct = 2
  density = 1
  expand = 3
  formula = G4_TETRACHLOROETHYLENE
  name = G4_TETRACHLOROETHYLENE
  specific = 4
FEATURE [App::DocumentObjectGroupPython] Tl_element001  label="Tl_element : 1"  # scripted group (container) (typed FeaturePython)
  n = 1
  ref = Tl_element
FEATURE [App::DocumentObjectGroupPython] Cl_element026  label="Cl_element : 013"  # scripted group (container) (typed FeaturePython)
  n = 1
  ref = Cl_element
FEATURE [App::DocumentObjectGroupPython] G4_THALLIUM_CHLORIDE  # scripted group (container) (typed FeaturePython)
  Dunit = g/cm3
  Dvalue = 7.004
  Group = -> [Tl_element001,Cl_element026]
  conduct = 2
  density = 1
  expand = 3
  formula = G4_THALLIUM_CHLORIDE
  name = G4_THALLIUM_CHLORIDE
  specific = 4
FEATURE [App::DocumentObjectGroupPython] H_element100  label="H_element : 0.147"  # scripted group (container) (typed FeaturePython)
  n = 0.105
FEATURE [App::DocumentObjectGroupPython] C_element110  label="C_element : 0.256"  # scripted group (container) (typed FeaturePython)
  n = 0.256
FEATURE [App::DocumentObjectGroupPython] N_element042  label="N_element : 0.760"  # scripted group (container) (typed FeaturePython)
  n = 0.027
FEATURE [App::DocumentObjectGroupPython] O_element094  label="O_element : 0.602"  # scripted group (container) (typed FeaturePython)
  n = 0.602
FEATURE [App::DocumentObjectGroupPython] Na_element019  label="Na_element : 0.102"  # scripted group (container) (typed FeaturePython)
  n = 0.001
FEATURE [App::DocumentObjectGroupPython] P_element011  label="P_element : 0.109"  # scripted group (container) (typed FeaturePython)
  n = 0.002
FEATURE [App::DocumentObjectGroupPython] S_element022  label="S_element : 0.023"  # scripted group (container) (typed FeaturePython)
  n = 0.003
FEATURE [App::DocumentObjectGroupPython] Cl_element027  label="Cl_element : 0.591"  # scripted group (container) (typed FeaturePython)
  n = 0.002
FEATURE [App::DocumentObjectGroupPython] K_element012  label="K_element : 0.018"  # scripted group (container) (typed FeaturePython)
  n = 0.002
FEATURE [App::DocumentObjectGroupPython] G4_TISSUE_SOFT_ICRP  # scripted group (container) (typed FeaturePython)
  Dunit = g/cm3
  Dvalue = 1.03
  Group = -> [H_element100,C_element110,N_element042,O_element094,Na_element019,P_element011,S_element022,Cl_element027,K_element012]
  conduct = 2
  density = 1
  expand = 3
  formula = G4_TISSUE_SOFT_ICRP
  name = G4_TISSUE_SOFT_ICRP
  specific = 4
FEATURE [App::DocumentObjectGroupPython] H_element101  label="H_element : 0.148"  # scripted group (container) (typed FeaturePython)
  n = 0.101
FEATURE [App::DocumentObjectGroupPython] C_element111  label="C_element : 0.111"  # scripted group (container) (typed FeaturePython)
  n = 0.111
FEATURE [App::DocumentObjectGroupPython] N_element043  label="N_element : 0.026"  # scripted group (container) (typed FeaturePython)
  n = 0.026
FEATURE [App::DocumentObjectGroupPython] O_element095  label="O_element : 0.762"  # scripted group (container) (typed FeaturePython)
  n = 0.762
FEATURE [App::DocumentObjectGroupPython] G4_TISSUE_SOFT_ICRU_4  label="G4_TISSUE_SOFT_ICRU-4"  # scripted group (container) (typed FeaturePython)
  Dunit = g/cm3
  Dvalue = 1
  Group = -> [H_element101,C_element111,N_element043,O_element095]
  conduct = 2
  density = 1
  expand = 3
  formula = G4_TISSUE_SOFT_ICRU-4
  name = G4_TISSUE_SOFT_ICRU-4
  specific = 4
FEATURE [App::DocumentObjectGroupPython] H_element102  label="H_element : 0.149"  # scripted group (container) (typed FeaturePython)
  n = 0.101869
FEATURE [App::DocumentObjectGroupPython] C_element112  label="C_element : 0.456"  # scripted group (container) (typed FeaturePython)
  n = 0.456179
FEATURE [App::DocumentObjectGroupPython] N_element044  label="N_element : 0.761"  # scripted group (container) (typed FeaturePython)
  n = 0.035172
FEATURE [App::DocumentObjectGroupPython] O_element096  label="O_element : 0.407"  # scripted group (container) (typed FeaturePython)
  n = 0.40678
FEATURE [App::DocumentObjectGroupPython] G4_TISSUE_METHANE  label="G4_TISSUE-METHANE"  # scripted group (container) (typed FeaturePython)
  Dunit = g/cm3
  Dvalue = 0.00106409
  Group = -> [H_element102,C_element112,N_element044,O_element096]
  conduct = 2
  density = 1
  expand = 3
  formula = G4_TISSUE-METHANE
  name = G4_TISSUE-METHANE
  specific = 4
FEATURE [App::DocumentObjectGroupPython] H_element103  label="H_element : 0.103"  # scripted group (container) (typed FeaturePython)
  n = 0.102672
FEATURE [App::DocumentObjectGroupPython] C_element113  label="C_element : 0.569"  # scripted group (container) (typed FeaturePython)
  n = 0.56894
FEATURE [App::DocumentObjectGroupPython] N_element045  label="N_element : 0.762"  # scripted group (container) (typed FeaturePython)
  n = 0.035022
FEATURE [App::DocumentObjectGroupPython] O_element097  label="O_element : 0.293"  # scripted group (container) (typed FeaturePython)
  n = 0.293366
FEATURE [App::DocumentObjectGroupPython] G4_TISSUE_PROPANE  label="G4_TISSUE-PROPANE"  # scripted group (container) (typed FeaturePython)
  Dunit = g/cm3
  Dvalue = 0.00182628
  Group = -> [H_element103,C_element113,N_element045,O_element097]
  conduct = 2
  density = 1
  expand = 3
  formula = G4_TISSUE-PROPANE
  name = G4_TISSUE-PROPANE
  specific = 4
FEATURE [App::DocumentObjectGroupPython] Ti_element003  label="Ti_element : 1"  # scripted group (container) (typed FeaturePython)
  n = 1
  ref = Ti_element
FEATURE [App::DocumentObjectGroupPython] O_element098  label="O_element : 052"  # scripted group (container) (typed FeaturePython)
  n = 2
  ref = O_element
FEATURE [App::DocumentObjectGroupPython] G4_TITANIUM_DIOXIDE  # scripted group (container) (typed FeaturePython)
  Dunit = g/cm3
  Dvalue = 4.26
  Group = -> [Ti_element003,O_element098]
  conduct = 2
  density = 1
  expand = 3
  formula = G4_TITANIUM_DIOXIDE
  name = G4_TITANIUM_DIOXIDE
  specific = 4
FEATURE [App::DocumentObjectGroupPython] C_element114  label="C_element : 061"  # scripted group (container) (typed FeaturePython)
  n = 7
  ref = C_element
FEATURE [App::DocumentObjectGroupPython] H_element104  label="H_element : 055"  # scripted group (container) (typed FeaturePython)
  n = 8
  ref = H_element
FEATURE [App::DocumentObjectGroupPython] G4_TOLUENE  # scripted group (container) (typed FeaturePython)
  Dunit = g/cm3
  Dvalue = 0.8669
  Group = -> [C_element114,H_element104]
  conduct = 2
  density = 1
  expand = 3
  formula = G4_TOLUENE
  name = G4_TOLUENE
  specific = 4
FEATURE [App::DocumentObjectGroupPython] C_element115  label="C_element : 062"  # scripted group (container) (typed FeaturePython)
  n = 2
  ref = C_element
FEATURE [App::DocumentObjectGroupPython] H_element105  label="H_element : 056"  # scripted group (container) (typed FeaturePython)
  n = 1
  ref = H_element
FEATURE [App::DocumentObjectGroupPython] Cl_element028  label="Cl_element : 014"  # scripted group (container) (typed FeaturePython)
  n = 3
  ref = Cl_element
FEATURE [App::DocumentObjectGroupPython] G4_TRICHLOROETHYLENE  # scripted group (container) (typed FeaturePython)
  Dunit = g/cm3
  Dvalue = 1.46
  Group = -> [C_element115,H_element105,Cl_element028]
  conduct = 2
  density = 1
  expand = 3
  formula = G4_TRICHLOROETHYLENE
  name = G4_TRICHLOROETHYLENE
  specific = 4
FEATURE [App::DocumentObjectGroupPython] C_element116  label="C_element : 063"  # scripted group (container) (typed FeaturePython)
  n = 6
  ref = C_element
FEATURE [App::DocumentObjectGroupPython] H_element106  label="H_element : 15"  # scripted group (container) (typed FeaturePython)
  n = 15
  ref = H_element
FEATURE [App::DocumentObjectGroupPython] O_element099  label="O_element : 053"  # scripted group (container) (typed FeaturePython)
  n = 4
  ref = O_element
FEATURE [App::DocumentObjectGroupPython] P_element012  label="P_element : 1"  # scripted group (container) (typed FeaturePython)
  n = 1
  ref = P_element
FEATURE [App::DocumentObjectGroupPython] G4_TRIETHYL_PHOSPHATE  # scripted group (container) (typed FeaturePython)
  Dunit = g/cm3
  Dvalue = 1.07
  Group = -> [C_element116,H_element106,O_element099,P_element012]
  conduct = 2
  density = 1
  expand = 3
  formula = G4_TRIETHYL_PHOSPHATE
  name = G4_TRIETHYL_PHOSPHATE
  specific = 4
FEATURE [App::DocumentObjectGroupPython] W_element003  label="W_element : 003"  # scripted group (container) (typed FeaturePython)
  n = 1
  ref = W_element
FEATURE [App::DocumentObjectGroupPython] F_element017  label="F_element : 6"  # scripted group (container) (typed FeaturePython)
  n = 6
  ref = F_element
FEATURE [App::DocumentObjectGroupPython] G4_TUNGSTEN_HEXAFLUORIDE  # scripted group (container) (typed FeaturePython)
  Dunit = g/cm3
  Dvalue = 2.4
  Group = -> [W_element003,F_element017]
  conduct = 2
  density = 1
  expand = 3
  formula = G4_TUNGSTEN_HEXAFLUORIDE
  name = G4_TUNGSTEN_HEXAFLUORIDE
  specific = 4
FEATURE [App::DocumentObjectGroupPython] U_element001  label="U_element : 1"  # scripted group (container) (typed FeaturePython)
  n = 1
  ref = U_element
FEATURE [App::DocumentObjectGroupPython] C_element117  label="C_element : 064"  # scripted group (container) (typed FeaturePython)
  n = 2
  ref = C_element
FEATURE [App::DocumentObjectGroupPython] G4_URANIUM_DICARBIDE  # scripted group (container) (typed FeaturePython)
  Dunit = g/cm3
  Dvalue = 11.28
  Group = -> [U_element001,C_element117]
  conduct = 2
  density = 1
  expand = 3
  formula = G4_URANIUM_DICARBIDE
  name = G4_URANIUM_DICARBIDE
  specific = 4
FEATURE [App::DocumentObjectGroupPython] U_element002  label="U_element : 002"  # scripted group (container) (typed FeaturePython)
  n = 1
  ref = U_element
FEATURE [App::DocumentObjectGroupPython] C_element118  label="C_element : 065"  # scripted group (container) (typed FeaturePython)
  n = 1
  ref = C_element
FEATURE [App::DocumentObjectGroupPython] G4_URANIUM_MONOCARBIDE  # scripted group (container) (typed FeaturePython)
  Dunit = g/cm3
  Dvalue = 13.63
  Group = -> [U_element002,C_element118]
  conduct = 2
  density = 1
  expand = 3
  formula = G4_URANIUM_MONOCARBIDE
  name = G4_URANIUM_MONOCARBIDE
  specific = 4
FEATURE [App::DocumentObjectGroupPython] U_element003  label="U_element : 003"  # scripted group (container) (typed FeaturePython)
  n = 1
  ref = U_element
FEATURE [App::DocumentObjectGroupPython] O_element100  label="O_element : 054"  # scripted group (container) (typed FeaturePython)
  n = 2
  ref = O_element
FEATURE [App::DocumentObjectGroupPython] G4_URANIUM_OXIDE  # scripted group (container) (typed FeaturePython)
  Dunit = g/cm3
  Dvalue = 10.96
  Group = -> [U_element003,O_element100]
  conduct = 2
  density = 1
  expand = 3
  formula = G4_URANIUM_OXIDE
  name = G4_URANIUM_OXIDE
  specific = 4
FEATURE [App::DocumentObjectGroupPython] C_element119  label="C_element : 066"  # scripted group (container) (typed FeaturePython)
  n = 1
  ref = C_element
FEATURE [App::DocumentObjectGroupPython] H_element107  label="H_element : 057"  # scripted group (container) (typed FeaturePython)
  n = 4
  ref = H_element
FEATURE [App::DocumentObjectGroupPython] N_element046  label="N_element : 019"  # scripted group (container) (typed FeaturePython)
  n = 2
  ref = N_element
FEATURE [App::DocumentObjectGroupPython] O_element101  label="O_element : 055"  # scripted group (container) (typed FeaturePython)
  n = 1
  ref = O_element
FEATURE [App::DocumentObjectGroupPython] G4_UREA  # scripted group (container) (typed FeaturePython)
  Dunit = g/cm3
  Dvalue = 1.323
  Group = -> [C_element119,H_element107,N_element046,O_element101]
  conduct = 2
  density = 1
  expand = 3
  formula = G4_UREA
  name = G4_UREA
  specific = 4
FEATURE [App::DocumentObjectGroupPython] C_element120  label="C_element : 067"  # scripted group (container) (typed FeaturePython)
  n = 5
  ref = C_element
FEATURE [App::DocumentObjectGroupPython] H_element108  label="H_element : 058"  # scripted group (container) (typed FeaturePython)
  n = 11
  ref = H_element
FEATURE [App::DocumentObjectGroupPython] N_element047  label="N_element : 020"  # scripted group (container) (typed FeaturePython)
  n = 1
  ref = N_element
FEATURE [App::DocumentObjectGroupPython] O_element102  label="O_element : 056"  # scripted group (container) (typed FeaturePython)
  n = 2
  ref = O_element
FEATURE [App::DocumentObjectGroupPython] G4_VALINE  # scripted group (container) (typed FeaturePython)
  Dunit = g/cm3
  Dvalue = 1.23
  Group = -> [C_element120,H_element108,N_element047,O_element102]
  conduct = 2
  density = 1
  expand = 3
  formula = G4_VALINE
  name = G4_VALINE
  specific = 4
FEATURE [App::DocumentObjectGroupPython] H_element109  label="H_element : 0.009"  # scripted group (container) (typed FeaturePython)
  n = 0.009417
FEATURE [App::DocumentObjectGroupPython] C_element121  label="C_element : 0.281"  # scripted group (container) (typed FeaturePython)
  n = 0.280555
FEATURE [App::DocumentObjectGroupPython] F_element018  label="F_element : 0.710"  # scripted group (container) (typed FeaturePython)
  n = 0.710028
FEATURE [App::DocumentObjectGroupPython] G4_VITON  # scripted group (container) (typed FeaturePython)
  Dunit = g/cm3
  Dvalue = 1.8
  Group = -> [H_element109,C_element121,F_element018]
  conduct = 2
  density = 1
  expand = 3
  formula = G4_VITON
  name = G4_VITON
  specific = 4
FEATURE [App::DocumentObjectGroupPython] H_element110  label="H_element : 059"  # scripted group (container) (typed FeaturePython)
  n = 2
  ref = H_element
FEATURE [App::DocumentObjectGroupPython] O_element103  label="O_element : 057"  # scripted group (container) (typed FeaturePython)
  n = 1
  ref = O_element
FEATURE [App::DocumentObjectGroupPython] G4_WATER  # scripted group (container) (typed FeaturePython)
  Dunit = g/cm3
  Dvalue = 1
  Group = -> [H_element110,O_element103]
  conduct = 2
  density = 1
  expand = 3
  formula = G4_WATER
  name = G4_WATER
  specific = 4
FEATURE [App::DocumentObjectGroupPython] H_element111  label="H_element : 060"  # scripted group (container) (typed FeaturePython)
  n = 2
  ref = H_element
FEATURE [App::DocumentObjectGroupPython] O_element104  label="O_element : 058"  # scripted group (container) (typed FeaturePython)
  n = 1
  ref = O_element
FEATURE [App::DocumentObjectGroupPython] G4_WATER_VAPOR  # scripted group (container) (typed FeaturePython)
  Dunit = g/cm3
  Dvalue = 0.000756182
  Group = -> [H_element111,O_element104]
  conduct = 2
  density = 1
  expand = 3
  formula = G4_WATER_VAPOR
  name = G4_WATER_VAPOR
  specific = 4
FEATURE [App::DocumentObjectGroupPython] C_element122  label="C_element : 068"  # scripted group (container) (typed FeaturePython)
  n = 8
  ref = C_element
FEATURE [App::DocumentObjectGroupPython] H_element112  label="H_element : 061"  # scripted group (container) (typed FeaturePython)
  n = 10
  ref = H_element
FEATURE [App::DocumentObjectGroupPython] G4_XYLENE  # scripted group (container) (typed FeaturePython)
  Dunit = g/cm3
  Dvalue = 0.87
  Group = -> [C_element122,H_element112]
  conduct = 2
  density = 1
  expand = 3
  formula = G4_XYLENE
  name = G4_XYLENE
  specific = 4
FEATURE [App::DocumentObjectGroupPython] C_element123  label="C_element : 069"  # scripted group (container) (typed FeaturePython)
  n = 1
  ref = C_element
FEATURE [App::DocumentObjectGroupPython] G4_GRAPHITE  # scripted group (container) (typed FeaturePython)
  Dunit = g/cm3
  Dvalue = 2.21
  Group = -> [C_element123]
  conduct = 2
  density = 1
  expand = 3
  formula = G4_GRAPHITE
  name = G4_GRAPHITE
  specific = 4
FEATURE [App::DocumentObjectGroupPython] NIST  # scripted group (container) (typed FeaturePython)
  Group = -> [G4_A_150_TISSUE,G4_ACETONE,G4_ACETYLENE,G4_ADENINE,G4_ADIPOSE_TISSUE_ICRP,G4_AIR,G4_ALANINE,G4_ALUMINUM_OXIDE,G4_AMBER,G4_AMMONIA,G4_ANILINE,G4_ANTHRACENE,G4_B_100_BONE,G4_BAKELITE,G4_BARIUM_FLUORIDE,G4_BARIUM_SULFATE,G4_BENZENE,G4_BERYLLIUM_OXIDE,G4_BGO,G4_BLOOD_ICRP,G4_BONE_COMPACT_ICRU,G4_BONE_CORTICAL_ICRP,G4_BORON_CARBIDE,G4_BORON_OXIDE,G4_BRAIN_ICRP,G4_BUTANE,G4_N_BUTYL_ALCOHOL,G4_C_552,+152 more]
FEATURE [App::DocumentObjectGroupPython] H_element113  label="H_element : 062"  # scripted group (container) (typed FeaturePython)
  n = 1
  ref = H_element
FEATURE [App::DocumentObjectGroupPython] G4_H  # scripted group (container) (typed FeaturePython)
  Dunit = g/cm3
  Dvalue = 8.3748e-05
  Group = -> [H_element113]
  conduct = 2
  density = 1
  expand = 3
  formula = H
  name = G4_H
  specific = 4
FEATURE [App::DocumentObjectGroupPython] He_element001  label="He_element : 1"  # scripted group (container) (typed FeaturePython)
  n = 1
  ref = He_element
FEATURE [App::DocumentObjectGroupPython] G4_He  # scripted group (container) (typed FeaturePython)
  Dunit = g/cm3
  Dvalue = 0.000166322
  Group = -> [He_element001]
  conduct = 2
  density = 1
  expand = 3
  formula = He
  name = G4_He
  specific = 4
FEATURE [App::DocumentObjectGroupPython] Li_element008  label="Li_element : 008"  # scripted group (container) (typed FeaturePython)
  n = 1
  ref = Li_element
FEATURE [App::DocumentObjectGroupPython] G4_Li  # scripted group (container) (typed FeaturePython)
  Dunit = g/cm3
  Dvalue = 0.534
  Group = -> [Li_element008]
  conduct = 2
  density = 1
  expand = 3
  formula = Li
  name = G4_Li
  specific = 4
FEATURE [App::DocumentObjectGroupPython] Be_element002  label="Be_element : 002"  # scripted group (container) (typed FeaturePython)
  n = 1
  ref = Be_element
FEATURE [App::DocumentObjectGroupPython] G4_Be  # scripted group (container) (typed FeaturePython)
  Dunit = g/cm3
  Dvalue = 1.848
  Group = -> [Be_element002]
  conduct = 2
  density = 1
  expand = 3
  formula = Be
  name = G4_Be
  specific = 4
FEATURE [App::DocumentObjectGroupPython] B_element007  label="B_element : 007"  # scripted group (container) (typed FeaturePython)
  n = 1
  ref = B_element
FEATURE [App::DocumentObjectGroupPython] G4_B  # scripted group (container) (typed FeaturePython)
  Dunit = g/cm3
  Dvalue = 2.37
  Group = -> [B_element007]
  conduct = 2
  density = 1
  expand = 3
  formula = B
  name = G4_B
  specific = 4
FEATURE [App::DocumentObjectGroupPython] C_element124  label="C_element : 070"  # scripted group (container) (typed FeaturePython)
  n = 1
  ref = C_element
FEATURE [App::DocumentObjectGroupPython] G4_C  # scripted group (container) (typed FeaturePython)
  Dunit = g/cm3
  Dvalue = 2
  Group = -> [C_element124]
  conduct = 2
  density = 1
  expand = 3
  formula = C
  name = G4_C
  specific = 4
FEATURE [App::DocumentObjectGroupPython] N_element048  label="N_element : 021"  # scripted group (container) (typed FeaturePython)
  n = 1
  ref = N_element
FEATURE [App::DocumentObjectGroupPython] G4_N  # scripted group (container) (typed FeaturePython)
  Dunit = g/cm3
  Dvalue = 0.0011652
  Group = -> [N_element048]
  conduct = 2
  density = 1
  expand = 3
  formula = N
  name = G4_N
  specific = 4
FEATURE [App::DocumentObjectGroupPython] O_element105  label="O_element : 059"  # scripted group (container) (typed FeaturePython)
  n = 1
  ref = O_element
FEATURE [App::DocumentObjectGroupPython] G4_O  # scripted group (container) (typed FeaturePython)
  Dunit = g/cm3
  Dvalue = 0.00133151
  Group = -> [O_element105]
  conduct = 2
  density = 1
  expand = 3
  formula = O
  name = G4_O
  specific = 4
FEATURE [App::DocumentObjectGroupPython] F_element019  label="F_element : 008"  # scripted group (container) (typed FeaturePython)
  n = 1
  ref = F_element
FEATURE [App::DocumentObjectGroupPython] G4_F  # scripted group (container) (typed FeaturePython)
  Dunit = g/cm3
  Dvalue = 0.00158029
  Group = -> [F_element019]
  conduct = 2
  density = 1
  expand = 3
  formula = F
  name = G4_F
  specific = 4
FEATURE [App::DocumentObjectGroupPython] Ne_element001  label="Ne_element : 1"  # scripted group (container) (typed FeaturePython)
  n = 1
  ref = Ne_element
FEATURE [App::DocumentObjectGroupPython] G4_Ne  # scripted group (container) (typed FeaturePython)
  Dunit = g/cm3
  Dvalue = 0.000838505
  Group = -> [Ne_element001]
  conduct = 2
  density = 1
  expand = 3
  formula = Ne
  name = G4_Ne
  specific = 4
FEATURE [App::DocumentObjectGroupPython] Na_element020  label="Na_element : 005"  # scripted group (container) (typed FeaturePython)
  n = 1
  ref = Na_element
FEATURE [App::DocumentObjectGroupPython] G4_Na  # scripted group (container) (typed FeaturePython)
  Dunit = g/cm3
  Dvalue = 0.971
  Group = -> [Na_element020]
  conduct = 2
  density = 1
  expand = 3
  formula = Na
  name = G4_Na
  specific = 4
FEATURE [App::DocumentObjectGroupPython] Mg_element011  label="Mg_element : 005"  # scripted group (container) (typed FeaturePython)
  n = 1
  ref = Mg_element
FEATURE [App::DocumentObjectGroupPython] G4_Mg  # scripted group (container) (typed FeaturePython)
  Dunit = g/cm3
  Dvalue = 1.74
  Group = -> [Mg_element011]
  conduct = 2
  density = 1
  expand = 3
  formula = Mg
  name = G4_Mg
  specific = 4
FEATURE [App::DocumentObjectGroupPython] Al_element004  label="Al_element : 1"  # scripted group (container) (typed FeaturePython)
  n = 1
  ref = Al_element
FEATURE [App::DocumentObjectGroupPython] G4_Al  # scripted group (container) (typed FeaturePython)
  Dunit = g/cm3
  Dvalue = 2.699
  Group = -> [Al_element004]
  conduct = 2
  density = 1
  expand = 3
  formula = Al
  name = G4_Al
  specific = 4
FEATURE [App::DocumentObjectGroupPython] Si_element007  label="Si_element : 002"  # scripted group (container) (typed FeaturePython)
  n = 1
  ref = Si_element
FEATURE [App::DocumentObjectGroupPython] G4_Si  # scripted group (container) (typed FeaturePython)
  Dunit = g/cm3
  Dvalue = 2.33
  Group = -> [Si_element007]
  conduct = 2
  density = 1
  expand = 3
  formula = Si
  name = G4_Si
  specific = 4
FEATURE [App::DocumentObjectGroupPython] P_element013  label="P_element : 002"  # scripted group (container) (typed FeaturePython)
  n = 1
  ref = P_element
FEATURE [App::DocumentObjectGroupPython] G4_P  # scripted group (container) (typed FeaturePython)
  Dunit = g/cm3
  Dvalue = 2.2
  Group = -> [P_element013]
  conduct = 2
  density = 1
  expand = 3
  formula = P
  name = G4_P
  specific = 4
FEATURE [App::DocumentObjectGroupPython] S_element023  label="S_element : 007"  # scripted group (container) (typed FeaturePython)
  n = 1
  ref = S_element
FEATURE [App::DocumentObjectGroupPython] G4_S  # scripted group (container) (typed FeaturePython)
  Dunit = g/cm3
  Dvalue = 2
  Group = -> [S_element023]
  conduct = 2
  density = 1
  expand = 3
  formula = S
  name = G4_S
  specific = 4
FEATURE [App::DocumentObjectGroupPython] Cl_element029  label="Cl_element : 015"  # scripted group (container) (typed FeaturePython)
  n = 1
  ref = Cl_element
FEATURE [App::DocumentObjectGroupPython] G4_Cl  # scripted group (container) (typed FeaturePython)
  Dunit = g/cm3
  Dvalue = 0.00299473
  Group = -> [Cl_element029]
  conduct = 2
  density = 1
  expand = 3
  formula = Cl
  name = G4_Cl
  specific = 4
FEATURE [App::DocumentObjectGroupPython] Ar_element002  label="Ar_element : 1"  # scripted group (container) (typed FeaturePython)
  n = 1
  ref = Ar_element
FEATURE [App::DocumentObjectGroupPython] G4_Ar  # scripted group (container) (typed FeaturePython)
  Dunit = g/cm3
  Dvalue = 0.00166201
  Group = -> [Ar_element002]
  conduct = 2
  density = 1
  expand = 3
  formula = Ar
  name = G4_Ar
  specific = 4
FEATURE [App::DocumentObjectGroupPython] K_element013  label="K_element : 003"  # scripted group (container) (typed FeaturePython)
  n = 1
  ref = K_element
FEATURE [App::DocumentObjectGroupPython] G4_K  # scripted group (container) (typed FeaturePython)
  Dunit = g/cm3
  Dvalue = 0.862
  Group = -> [K_element013]
  conduct = 2
  density = 1
  expand = 3
  formula = K
  name = G4_K
  specific = 4
FEATURE [App::DocumentObjectGroupPython] Ca_element014  label="Ca_element : 007"  # scripted group (container) (typed FeaturePython)
  n = 1
  ref = Ca_element
FEATURE [App::DocumentObjectGroupPython] G4_Ca  # scripted group (container) (typed FeaturePython)
  Dunit = g/cm3
  Dvalue = 1.55
  Group = -> [Ca_element014]
  conduct = 2
  density = 1
  expand = 3
  formula = Ca
  name = G4_Ca
  specific = 4
FEATURE [App::DocumentObjectGroupPython] Sc_element001  label="Sc_element : 1"  # scripted group (container) (typed FeaturePython)
  n = 1
  ref = Sc_element
FEATURE [App::DocumentObjectGroupPython] G4_Sc  # scripted group (container) (typed FeaturePython)
  Dunit = g/cm3
  Dvalue = 2.989
  Group = -> [Sc_element001]
  conduct = 2
  density = 1
  expand = 3
  formula = Sc
  name = G4_Sc
  specific = 4
FEATURE [App::DocumentObjectGroupPython] Ti_element004  label="Ti_element : 002"  # scripted group (container) (typed FeaturePython)
  n = 1
  ref = Ti_element
FEATURE [App::DocumentObjectGroupPython] G4_Ti  # scripted group (container) (typed FeaturePython)
  Dunit = g/cm3
  Dvalue = 4.54
  Group = -> [Ti_element004]
  conduct = 2
  density = 1
  expand = 3
  formula = Ti
  name = G4_Ti
  specific = 4
FEATURE [App::DocumentObjectGroupPython] V_element001  label="V_element : 1"  # scripted group (container) (typed FeaturePython)
  n = 1
  ref = V_element
FEATURE [App::DocumentObjectGroupPython] G4_V  # scripted group (container) (typed FeaturePython)
  Dunit = g/cm3
  Dvalue = 6.11
  Group = -> [V_element001]
  conduct = 2
  density = 1
  expand = 3
  formula = V
  name = G4_V
  specific = 4
FEATURE [App::DocumentObjectGroupPython] Cr_element001  label="Cr_element : 1"  # scripted group (container) (typed FeaturePython)
  n = 1
  ref = Cr_element
FEATURE [App::DocumentObjectGroupPython] G4_Cr  # scripted group (container) (typed FeaturePython)
  Dunit = g/cm3
  Dvalue = 7.18
  Group = -> [Cr_element001]
  conduct = 2
  density = 1
  expand = 3
  formula = Cr
  name = G4_Cr
  specific = 4
FEATURE [App::DocumentObjectGroupPython] Mn_element001  label="Mn_element : 1"  # scripted group (container) (typed FeaturePython)
  n = 1
  ref = Mn_element
FEATURE [App::DocumentObjectGroupPython] G4_Mn  # scripted group (container) (typed FeaturePython)
  Dunit = g/cm3
  Dvalue = 7.44
  Group = -> [Mn_element001]
  conduct = 2
  density = 1
  expand = 3
  formula = Mn
  name = G4_Mn
  specific = 4
FEATURE [App::DocumentObjectGroupPython] Fe_element007  label="Fe_element : 004"  # scripted group (container) (typed FeaturePython)
  n = 1
  ref = Fe_element
FEATURE [App::DocumentObjectGroupPython] G4_Fe  # scripted group (container) (typed FeaturePython)
  Dunit = g/cm3
  Dvalue = 7.874
  Group = -> [Fe_element007]
  conduct = 2
  density = 1
  expand = 3
  formula = Fe
  name = G4_Fe
  specific = 4
FEATURE [App::DocumentObjectGroupPython] Co_element001  label="Co_element : 1"  # scripted group (container) (typed FeaturePython)
  n = 1
  ref = Co_element
FEATURE [App::DocumentObjectGroupPython] G4_Co  # scripted group (container) (typed FeaturePython)
  Dunit = g/cm3
  Dvalue = 8.9
  Group = -> [Co_element001]
  conduct = 2
  density = 1
  expand = 3
  formula = Co
  name = G4_Co
  specific = 4
FEATURE [App::DocumentObjectGroupPython] Ni_element001  label="Ni_element : 1"  # scripted group (container) (typed FeaturePython)
  n = 1
  ref = Ni_element
FEATURE [App::DocumentObjectGroupPython] G4_Ni  # scripted group (container) (typed FeaturePython)
  Dunit = g/cm3
  Dvalue = 8.902
  Group = -> [Ni_element001]
  conduct = 2
  density = 1
  expand = 3
  formula = Ni
  name = G4_Ni
  specific = 4
FEATURE [App::DocumentObjectGroupPython] Cu_element001  label="Cu_element : 1"  # scripted group (container) (typed FeaturePython)
  n = 1
  ref = Cu_element
FEATURE [App::DocumentObjectGroupPython] G4_Cu  # scripted group (container) (typed FeaturePython)
  Dunit = g/cm3
  Dvalue = 8.96
  Group = -> [Cu_element001]
  conduct = 2
  density = 1
  expand = 3
  formula = Cu
  name = G4_Cu
  specific = 4
FEATURE [App::DocumentObjectGroupPython] Zn_element001  label="Zn_element : 1"  # scripted group (container) (typed FeaturePython)
  n = 1
  ref = Zn_element
FEATURE [App::DocumentObjectGroupPython] G4_Zn  # scripted group (container) (typed FeaturePython)
  Dunit = g/cm3
  Dvalue = 7.133
  Group = -> [Zn_element001]
  conduct = 2
  density = 1
  expand = 3
  formula = Zn
  name = G4_Zn
  specific = 4
FEATURE [App::DocumentObjectGroupPython] Ga_element002  label="Ga_element : 002"  # scripted group (container) (typed FeaturePython)
  n = 1
  ref = Ga_element
FEATURE [App::DocumentObjectGroupPython] G4_Ga  # scripted group (container) (typed FeaturePython)
  Dunit = g/cm3
  Dvalue = 5.904
  Group = -> [Ga_element002]
  conduct = 2
  density = 1
  expand = 3
  formula = Ga
  name = G4_Ga
  specific = 4
FEATURE [App::DocumentObjectGroupPython] Ge_element002  label="Ge_element : 1"  # scripted group (container) (typed FeaturePython)
  n = 1
  ref = Ge_element
FEATURE [App::DocumentObjectGroupPython] G4_Ge  # scripted group (container) (typed FeaturePython)
  Dunit = g/cm3
  Dvalue = 5.323
  Group = -> [Ge_element002]
  conduct = 2
  density = 1
  expand = 3
  formula = Ge
  name = G4_Ge
  specific = 4
FEATURE [App::DocumentObjectGroupPython] As_element003  label="As_element : 002"  # scripted group (container) (typed FeaturePython)
  n = 1
  ref = As_element
FEATURE [App::DocumentObjectGroupPython] G4_As  # scripted group (container) (typed FeaturePython)
  Dunit = g/cm3
  Dvalue = 5.73
  Group = -> [As_element003]
  conduct = 2
  density = 1
  expand = 3
  formula = As
  name = G4_As
  specific = 4
FEATURE [App::DocumentObjectGroupPython] Se_element001  label="Se_element : 1"  # scripted group (container) (typed FeaturePython)
  n = 1
  ref = Se_element
FEATURE [App::DocumentObjectGroupPython] G4_Se  # scripted group (container) (typed FeaturePython)
  Dunit = g/cm3
  Dvalue = 4.5
  Group = -> [Se_element001]
  conduct = 2
  density = 1
  expand = 3
  formula = Se
  name = G4_Se
  specific = 4
FEATURE [App::DocumentObjectGroupPython] Br_element007  label="Br_element : 004"  # scripted group (container) (typed FeaturePython)
  n = 1
  ref = Br_element
FEATURE [App::DocumentObjectGroupPython] G4_Br  # scripted group (container) (typed FeaturePython)
  Dunit = g/cm3
  Dvalue = 0.0070721
  Group = -> [Br_element007]
  conduct = 2
  density = 1
  expand = 3
  formula = Br
  name = G4_Br
  specific = 4
FEATURE [App::DocumentObjectGroupPython] Kr_element001  label="Kr_element : 1"  # scripted group (container) (typed FeaturePython)
  n = 1
  ref = Kr_element
FEATURE [App::DocumentObjectGroupPython] G4_Kr  # scripted group (container) (typed FeaturePython)
  Dunit = g/cm3
  Dvalue = 0.00347832
  Group = -> [Kr_element001]
  conduct = 2
  density = 1
  expand = 3
  formula = Kr
  name = G4_Kr
  specific = 4
FEATURE [App::DocumentObjectGroupPython] Rb_element001  label="Rb_element : 1"  # scripted group (container) (typed FeaturePython)
  n = 1
  ref = Rb_element
FEATURE [App::DocumentObjectGroupPython] G4_Rb  # scripted group (container) (typed FeaturePython)
  Dunit = g/cm3
  Dvalue = 1.532
  Group = -> [Rb_element001]
  conduct = 2
  density = 1
  expand = 3
  formula = Rb
  name = G4_Rb
  specific = 4
FEATURE [App::DocumentObjectGroupPython] Sr_element001  label="Sr_element : 1"  # scripted group (container) (typed FeaturePython)
  n = 1
  ref = Sr_element
FEATURE [App::DocumentObjectGroupPython] G4_Sr  # scripted group (container) (typed FeaturePython)
  Dunit = g/cm3
  Dvalue = 2.54
  Group = -> [Sr_element001]
  conduct = 2
  density = 1
  expand = 3
  formula = Sr
  name = G4_Sr
  specific = 4
FEATURE [App::DocumentObjectGroupPython] Y_element001  label="Y_element : 1"  # scripted group (container) (typed FeaturePython)
  n = 1
  ref = Y_element
FEATURE [App::DocumentObjectGroupPython] G4_Y  # scripted group (container) (typed FeaturePython)
  Dunit = g/cm3
  Dvalue = 4.469
  Group = -> [Y_element001]
  conduct = 2
  density = 1
  expand = 3
  formula = Y
  name = G4_Y
  specific = 4
FEATURE [App::DocumentObjectGroupPython] Zr_element001  label="Zr_element : 1"  # scripted group (container) (typed FeaturePython)
  n = 1
  ref = Zr_element
FEATURE [App::DocumentObjectGroupPython] G4_Zr  # scripted group (container) (typed FeaturePython)
  Dunit = g/cm3
  Dvalue = 6.506
  Group = -> [Zr_element001]
  conduct = 2
  density = 1
  expand = 3
  formula = Zr
  name = G4_Zr
  specific = 4
FEATURE [App::DocumentObjectGroupPython] Nb_element001  label="Nb_element : 1"  # scripted group (container) (typed FeaturePython)
  n = 1
  ref = Nb_element
FEATURE [App::DocumentObjectGroupPython] G4_Nb  # scripted group (container) (typed FeaturePython)
  Dunit = g/cm3
  Dvalue = 8.57
  Group = -> [Nb_element001]
  conduct = 2
  density = 1
  expand = 3
  formula = Nb
  name = G4_Nb
  specific = 4
FEATURE [App::DocumentObjectGroupPython] Mo_element001  label="Mo_element : 1"  # scripted group (container) (typed FeaturePython)
  n = 1
  ref = Mo_element
FEATURE [App::DocumentObjectGroupPython] G4_Mo  # scripted group (container) (typed FeaturePython)
  Dunit = g/cm3
  Dvalue = 10.22
  Group = -> [Mo_element001]
  conduct = 2
  density = 1
  expand = 3
  formula = Mo
  name = G4_Mo
  specific = 4
FEATURE [App::DocumentObjectGroupPython] Tc_element001  label="Tc_element : 1"  # scripted group (container) (typed FeaturePython)
  n = 1
  ref = Tc_element
FEATURE [App::DocumentObjectGroupPython] G4_Tc  # scripted group (container) (typed FeaturePython)
  Dunit = g/cm3
  Dvalue = 11.5
  Group = -> [Tc_element001]
  conduct = 2
  density = 1
  expand = 3
  formula = Tc
  name = G4_Tc
  specific = 4
FEATURE [App::DocumentObjectGroupPython] Ru_element001  label="Ru_element : 1"  # scripted group (container) (typed FeaturePython)
  n = 1
  ref = Ru_element
FEATURE [App::DocumentObjectGroupPython] G4_Ru  # scripted group (container) (typed FeaturePython)
  Dunit = g/cm3
  Dvalue = 12.41
  Group = -> [Ru_element001]
  conduct = 2
  density = 1
  expand = 3
  formula = Ru
  name = G4_Ru
  specific = 4
FEATURE [App::DocumentObjectGroupPython] Rh_element001  label="Rh_element : 1"  # scripted group (container) (typed FeaturePython)
  n = 1
  ref = Rh_element
FEATURE [App::DocumentObjectGroupPython] G4_Rh  # scripted group (container) (typed FeaturePython)
  Dunit = g/cm3
  Dvalue = 12.41
  Group = -> [Rh_element001]
  conduct = 2
  density = 1
  expand = 3
  formula = Rh
  name = G4_Rh
  specific = 4
FEATURE [App::DocumentObjectGroupPython] Pd_element001  label="Pd_element : 1"  # scripted group (container) (typed FeaturePython)
  n = 1
  ref = Pd_element
FEATURE [App::DocumentObjectGroupPython] G4_Pd  # scripted group (container) (typed FeaturePython)
  Dunit = g/cm3
  Dvalue = 12.02
  Group = -> [Pd_element001]
  conduct = 2
  density = 1
  expand = 3
  formula = Pd
  name = G4_Pd
  specific = 4
FEATURE [App::DocumentObjectGroupPython] Ag_element006  label="Ag_element : 004"  # scripted group (container) (typed FeaturePython)
  n = 1
  ref = Ag_element
FEATURE [App::DocumentObjectGroupPython] G4_Ag  # scripted group (container) (typed FeaturePython)
  Dunit = g/cm3
  Dvalue = 10.5
  Group = -> [Ag_element006]
  conduct = 2
  density = 1
  expand = 3
  formula = Ag
  name = G4_Ag
  specific = 4
FEATURE [App::DocumentObjectGroupPython] Cd_element003  label="Cd_element : 003"  # scripted group (container) (typed FeaturePython)
  n = 1
  ref = Cd_element
FEATURE [App::DocumentObjectGroupPython] G4_Cd  # scripted group (container) (typed FeaturePython)
  Dunit = g/cm3
  Dvalue = 8.65
  Group = -> [Cd_element003]
  conduct = 2
  density = 1
  expand = 3
  formula = Cd
  name = G4_Cd
  specific = 4
FEATURE [App::DocumentObjectGroupPython] In_element001  label="In_element : 1"  # scripted group (container) (typed FeaturePython)
  n = 1
  ref = In_element
FEATURE [App::DocumentObjectGroupPython] G4_In  # scripted group (container) (typed FeaturePython)
  Dunit = g/cm3
  Dvalue = 7.31
  Group = -> [In_element001]
  conduct = 2
  density = 1
  expand = 3
  formula = In
  name = G4_In
  specific = 4
FEATURE [App::DocumentObjectGroupPython] Sn_element001  label="Sn_element : 1"  # scripted group (container) (typed FeaturePython)
  n = 1
  ref = Sn_element
FEATURE [App::DocumentObjectGroupPython] G4_Sn  # scripted group (container) (typed FeaturePython)
  Dunit = g/cm3
  Dvalue = 7.31
  Group = -> [Sn_element001]
  conduct = 2
  density = 1
  expand = 3
  formula = Sn
  name = G4_Sn
  specific = 4
FEATURE [App::DocumentObjectGroupPython] Sb_element001  label="Sb_element : 1"  # scripted group (container) (typed FeaturePython)
  n = 1
  ref = Sb_element
FEATURE [App::DocumentObjectGroupPython] G4_Sb  # scripted group (container) (typed FeaturePython)
  Dunit = g/cm3
  Dvalue = 6.691
  Group = -> [Sb_element001]
  conduct = 2
  density = 1
  expand = 3
  formula = Sb
  name = G4_Sb
  specific = 4
FEATURE [App::DocumentObjectGroupPython] Te_element002  label="Te_element : 002"  # scripted group (container) (typed FeaturePython)
  n = 1
  ref = Te_element
FEATURE [App::DocumentObjectGroupPython] G4_Te  # scripted group (container) (typed FeaturePython)
  Dunit = g/cm3
  Dvalue = 6.24
  Group = -> [Te_element002]
  conduct = 2
  density = 1
  expand = 3
  formula = Te
  name = G4_Te
  specific = 4
FEATURE [App::DocumentObjectGroupPython] I_element010  label="I_element : 006"  # scripted group (container) (typed FeaturePython)
  n = 1
  ref = I_element
FEATURE [App::DocumentObjectGroupPython] G4_I  # scripted group (container) (typed FeaturePython)
  Dunit = g/cm3
  Dvalue = 4.93
  Group = -> [I_element010]
  conduct = 2
  density = 1
  expand = 3
  formula = I
  name = G4_I
  specific = 4
FEATURE [App::DocumentObjectGroupPython] Xe_element001  label="Xe_element : 1"  # scripted group (container) (typed FeaturePython)
  n = 1
  ref = Xe_element
FEATURE [App::DocumentObjectGroupPython] G4_Xe  # scripted group (container) (typed FeaturePython)
  Dunit = g/cm3
  Dvalue = 0.00548536
  Group = -> [Xe_element001]
  conduct = 2
  density = 1
  expand = 3
  formula = Xe
  name = G4_Xe
  specific = 4
FEATURE [App::DocumentObjectGroupPython] Cs_element003  label="Cs_element : 003"  # scripted group (container) (typed FeaturePython)
  n = 1
  ref = Cs_element
FEATURE [App::DocumentObjectGroupPython] G4_Cs  # scripted group (container) (typed FeaturePython)
  Dunit = g/cm3
  Dvalue = 1.873
  Group = -> [Cs_element003]
  conduct = 2
  density = 1
  expand = 3
  formula = Cs
  name = G4_Cs
  specific = 4
FEATURE [App::DocumentObjectGroupPython] Ba_element003  label="Ba_element : 003"  # scripted group (container) (typed FeaturePython)
  n = 1
  ref = Ba_element
FEATURE [App::DocumentObjectGroupPython] G4_Ba  # scripted group (container) (typed FeaturePython)
  Dunit = g/cm3
  Dvalue = 3.5
  Group = -> [Ba_element003]
  conduct = 2
  density = 1
  expand = 3
  formula = Ba
  name = G4_Ba
  specific = 4
FEATURE [App::DocumentObjectGroupPython] La_element003  label="La_element : 003"  # scripted group (container) (typed FeaturePython)
  n = 1
  ref = La_element
FEATURE [App::DocumentObjectGroupPython] G4_La  # scripted group (container) (typed FeaturePython)
  Dunit = g/cm3
  Dvalue = 6.154
  Group = -> [La_element003]
  conduct = 2
  density = 1
  expand = 3
  formula = La
  name = G4_La
  specific = 4
FEATURE [App::DocumentObjectGroupPython] Ce_element002  label="Ce_element : 1"  # scripted group (container) (typed FeaturePython)
  n = 1
  ref = Ce_element
FEATURE [App::DocumentObjectGroupPython] G4_Ce  # scripted group (container) (typed FeaturePython)
  Dunit = g/cm3
  Dvalue = 6.657
  Group = -> [Ce_element002]
  conduct = 2
  density = 1
  expand = 3
  formula = Ce
  name = G4_Ce
  specific = 4
FEATURE [App::DocumentObjectGroupPython] Pr_element001  label="Pr_element : 1"  # scripted group (container) (typed FeaturePython)
  n = 1
  ref = Pr_element
FEATURE [App::DocumentObjectGroupPython] G4_Pr  # scripted group (container) (typed FeaturePython)
  Dunit = g/cm3
  Dvalue = 6.71
  Group = -> [Pr_element001]
  conduct = 2
  density = 1
  expand = 3
  formula = Pr
  name = G4_Pr
  specific = 4
FEATURE [App::DocumentObjectGroupPython] Nd_element001  label="Nd_element : 1"  # scripted group (container) (typed FeaturePython)
  n = 1
  ref = Nd_element
FEATURE [App::DocumentObjectGroupPython] G4_Nd  # scripted group (container) (typed FeaturePython)
  Dunit = g/cm3
  Dvalue = 6.9
  Group = -> [Nd_element001]
  conduct = 2
  density = 1
  expand = 3
  formula = Nd
  name = G4_Nd
  specific = 4
FEATURE [App::DocumentObjectGroupPython] Pm_element001  label="Pm_element : 1"  # scripted group (container) (typed FeaturePython)
  n = 1
  ref = Pm_element
FEATURE [App::DocumentObjectGroupPython] G4_Pm  # scripted group (container) (typed FeaturePython)
  Dunit = g/cm3
  Dvalue = 7.22
  Group = -> [Pm_element001]
  conduct = 2
  density = 1
  expand = 3
  formula = Pm
  name = G4_Pm
  specific = 4
FEATURE [App::DocumentObjectGroupPython] Sm_element001  label="Sm_element : 1"  # scripted group (container) (typed FeaturePython)
  n = 1
  ref = Sm_element
FEATURE [App::DocumentObjectGroupPython] G4_Sm  # scripted group (container) (typed FeaturePython)
  Dunit = g/cm3
  Dvalue = 7.46
  Group = -> [Sm_element001]
  conduct = 2
  density = 1
  expand = 3
  formula = Sm
  name = G4_Sm
  specific = 4
FEATURE [App::DocumentObjectGroupPython] Eu_element001  label="Eu_element : 1"  # scripted group (container) (typed FeaturePython)
  n = 1
  ref = Eu_element
FEATURE [App::DocumentObjectGroupPython] G4_Eu  # scripted group (container) (typed FeaturePython)
  Dunit = g/cm3
  Dvalue = 5.243
  Group = -> [Eu_element001]
  conduct = 2
  density = 1
  expand = 3
  formula = Eu
  name = G4_Eu
  specific = 4
FEATURE [App::DocumentObjectGroupPython] Gd_element002  label="Gd_element : 1"  # scripted group (container) (typed FeaturePython)
  n = 1
  ref = Gd_element
FEATURE [App::DocumentObjectGroupPython] G4_Gd  # scripted group (container) (typed FeaturePython)
  Dunit = g/cm3
  Dvalue = 7.9004
  Group = -> [Gd_element002]
  conduct = 2
  density = 1
  expand = 3
  formula = Gd
  name = G4_Gd
  specific = 4
FEATURE [App::DocumentObjectGroupPython] Tb_element001  label="Tb_element : 1"  # scripted group (container) (typed FeaturePython)
  n = 1
  ref = Tb_element
FEATURE [App::DocumentObjectGroupPython] G4_Tb  # scripted group (container) (typed FeaturePython)
  Dunit = g/cm3
  Dvalue = 8.229
  Group = -> [Tb_element001]
  conduct = 2
  density = 1
  expand = 3
  formula = Tb
  name = G4_Tb
  specific = 4
FEATURE [App::DocumentObjectGroupPython] Dy_element001  label="Dy_element : 1"  # scripted group (container) (typed FeaturePython)
  n = 1
  ref = Dy_element
FEATURE [App::DocumentObjectGroupPython] G4_Dy  # scripted group (container) (typed FeaturePython)
  Dunit = g/cm3
  Dvalue = 8.55
  Group = -> [Dy_element001]
  conduct = 2
  density = 1
  expand = 3
  formula = Dy
  name = G4_Dy
  specific = 4
FEATURE [App::DocumentObjectGroupPython] Ho_element001  label="Ho_element : 1"  # scripted group (container) (typed FeaturePython)
  n = 1
  ref = Ho_element
FEATURE [App::DocumentObjectGroupPython] G4_Ho  # scripted group (container) (typed FeaturePython)
  Dunit = g/cm3
  Dvalue = 8.795
  Group = -> [Ho_element001]
  conduct = 2
  density = 1
  expand = 3
  formula = Ho
  name = G4_Ho
  specific = 4
FEATURE [App::DocumentObjectGroupPython] Er_element001  label="Er_element : 1"  # scripted group (container) (typed FeaturePython)
  n = 1
  ref = Er_element
FEATURE [App::DocumentObjectGroupPython] G4_Er  # scripted group (container) (typed FeaturePython)
  Dunit = g/cm3
  Dvalue = 9.066
  Group = -> [Er_element001]
  conduct = 2
  density = 1
  expand = 3
  formula = Er
  name = G4_Er
  specific = 4
FEATURE [App::DocumentObjectGroupPython] Tm_element001  label="Tm_element : 1"  # scripted group (container) (typed FeaturePython)
  n = 1
  ref = Tm_element
FEATURE [App::DocumentObjectGroupPython] G4_Tm  # scripted group (container) (typed FeaturePython)
  Dunit = g/cm3
  Dvalue = 9.321
  Group = -> [Tm_element001]
  conduct = 2
  density = 1
  expand = 3
  formula = Tm
  name = G4_Tm
  specific = 4
FEATURE [App::DocumentObjectGroupPython] Yb_element001  label="Yb_element : 1"  # scripted group (container) (typed FeaturePython)
  n = 1
  ref = Yb_element
FEATURE [App::DocumentObjectGroupPython] G4_Yb  # scripted group (container) (typed FeaturePython)
  Dunit = g/cm3
  Dvalue = 6.73
  Group = -> [Yb_element001]
  conduct = 2
  density = 1
  expand = 3
  formula = Yb
  name = G4_Yb
  specific = 4
FEATURE [App::DocumentObjectGroupPython] Lu_element001  label="Lu_element : 1"  # scripted group (container) (typed FeaturePython)
  n = 1
  ref = Lu_element
FEATURE [App::DocumentObjectGroupPython] G4_Lu  # scripted group (container) (typed FeaturePython)
  Dunit = g/cm3
  Dvalue = 9.84
  Group = -> [Lu_element001]
  conduct = 2
  density = 1
  expand = 3
  formula = Lu
  name = G4_Lu
  specific = 4
FEATURE [App::DocumentObjectGroupPython] Hf_element001  label="Hf_element : 1"  # scripted group (container) (typed FeaturePython)
  n = 1
  ref = Hf_element
FEATURE [App::DocumentObjectGroupPython] G4_Hf  # scripted group (container) (typed FeaturePython)
  Dunit = g/cm3
  Dvalue = 13.31
  Group = -> [Hf_element001]
  conduct = 2
  density = 1
  expand = 3
  formula = Hf
  name = G4_Hf
  specific = 4
FEATURE [App::DocumentObjectGroupPython] Ta_element001  label="Ta_element : 1"  # scripted group (container) (typed FeaturePython)
  n = 1
  ref = Ta_element
FEATURE [App::DocumentObjectGroupPython] G4_Ta  # scripted group (container) (typed FeaturePython)
  Dunit = g/cm3
  Dvalue = 16.654
  Group = -> [Ta_element001]
  conduct = 2
  density = 1
  expand = 3
  formula = Ta
  name = G4_Ta
  specific = 4
FEATURE [App::DocumentObjectGroupPython] W_element004  label="W_element : 004"  # scripted group (container) (typed FeaturePython)
  n = 1
  ref = W_element
FEATURE [App::DocumentObjectGroupPython] G4_W  # scripted group (container) (typed FeaturePython)
  Dunit = g/cm3
  Dvalue = 19.3
  Group = -> [W_element004]
  conduct = 2
  density = 1
  expand = 3
  formula = W
  name = G4_W
  specific = 4
FEATURE [App::DocumentObjectGroupPython] Re_element001  label="Re_element : 1"  # scripted group (container) (typed FeaturePython)
  n = 1
  ref = Re_element
FEATURE [App::DocumentObjectGroupPython] G4_Re  # scripted group (container) (typed FeaturePython)
  Dunit = g/cm3
  Dvalue = 21.02
  Group = -> [Re_element001]
  conduct = 2
  density = 1
  expand = 3
  formula = Re
  name = G4_Re
  specific = 4
FEATURE [App::DocumentObjectGroupPython] Os_element001  label="Os_element : 1"  # scripted group (container) (typed FeaturePython)
  n = 1
  ref = Os_element
FEATURE [App::DocumentObjectGroupPython] G4_Os  # scripted group (container) (typed FeaturePython)
  Dunit = g/cm3
  Dvalue = 22.57
  Group = -> [Os_element001]
  conduct = 2
  density = 1
  expand = 3
  formula = Os
  name = G4_Os
  specific = 4
FEATURE [App::DocumentObjectGroupPython] Ir_element001  label="Ir_element : 1"  # scripted group (container) (typed FeaturePython)
  n = 1
  ref = Ir_element
FEATURE [App::DocumentObjectGroupPython] G4_Ir  # scripted group (container) (typed FeaturePython)
  Dunit = g/cm3
  Dvalue = 22.42
  Group = -> [Ir_element001]
  conduct = 2
  density = 1
  expand = 3
  formula = Ir
  name = G4_Ir
  specific = 4
FEATURE [App::DocumentObjectGroupPython] Pt_element001  label="Pt_element : 1"  # scripted group (container) (typed FeaturePython)
  n = 1
  ref = Pt_element
FEATURE [App::DocumentObjectGroupPython] G4_Pt  # scripted group (container) (typed FeaturePython)
  Dunit = g/cm3
  Dvalue = 21.45
  Group = -> [Pt_element001]
  conduct = 2
  density = 1
  expand = 3
  formula = Pt
  name = G4_Pt
  specific = 4
FEATURE [App::DocumentObjectGroupPython] Au_element001  label="Au_element : 1"  # scripted group (container) (typed FeaturePython)
  n = 1
  ref = Au_element
FEATURE [App::DocumentObjectGroupPython] G4_Au  # scripted group (container) (typed FeaturePython)
  Dunit = g/cm3
  Dvalue = 19.32
  Group = -> [Au_element001]
  conduct = 2
  density = 1
  expand = 3
  formula = Au
  name = G4_Au
  specific = 4
FEATURE [App::DocumentObjectGroupPython] Hg_element002  label="Hg_element : 002"  # scripted group (container) (typed FeaturePython)
  n = 1
  ref = Hg_element
FEATURE [App::DocumentObjectGroupPython] G4_Hg  # scripted group (container) (typed FeaturePython)
  Dunit = g/cm3
  Dvalue = 13.546
  Group = -> [Hg_element002]
  conduct = 2
  density = 1
  expand = 3
  formula = Hg
  name = G4_Hg
  specific = 4
FEATURE [App::DocumentObjectGroupPython] Tl_element002  label="Tl_element : 002"  # scripted group (container) (typed FeaturePython)
  n = 1
  ref = Tl_element
FEATURE [App::DocumentObjectGroupPython] G4_Tl  # scripted group (container) (typed FeaturePython)
  Dunit = g/cm3
  Dvalue = 11.72
  Group = -> [Tl_element002]
  conduct = 2
  density = 1
  expand = 3
  formula = Tl
  name = G4_Tl
  specific = 4
FEATURE [App::DocumentObjectGroupPython] Pb_element003  label="Pb_element : 1"  # scripted group (container) (typed FeaturePython)
  n = 1
  ref = Pb_element
FEATURE [App::DocumentObjectGroupPython] G4_Pb  # scripted group (container) (typed FeaturePython)
  Dunit = g/cm3
  Dvalue = 11.35
  Group = -> [Pb_element003]
  conduct = 2
  density = 1
  expand = 3
  formula = Pb
  name = G4_Pb
  specific = 4
FEATURE [App::DocumentObjectGroupPython] Bi_element002  label="Bi_element : 1"  # scripted group (container) (typed FeaturePython)
  n = 1
  ref = Bi_element
FEATURE [App::DocumentObjectGroupPython] G4_Bi  # scripted group (container) (typed FeaturePython)
  Dunit = g/cm3
  Dvalue = 9.747
  Group = -> [Bi_element002]
  conduct = 2
  density = 1
  expand = 3
  formula = Bi
  name = G4_Bi
  specific = 4
FEATURE [App::DocumentObjectGroupPython] Po_element001  label="Po_element : 1"  # scripted group (container) (typed FeaturePython)
  n = 1
  ref = Po_element
FEATURE [App::DocumentObjectGroupPython] G4_Po  # scripted group (container) (typed FeaturePython)
  Dunit = g/cm3
  Dvalue = 9.32
  Group = -> [Po_element001]
  conduct = 2
  density = 1
  expand = 3
  formula = Po
  name = G4_Po
  specific = 4
FEATURE [App::DocumentObjectGroupPython] At_element001  label="At_element : 1"  # scripted group (container) (typed FeaturePython)
  n = 1
  ref = At_element
FEATURE [App::DocumentObjectGroupPython] G4_At  # scripted group (container) (typed FeaturePython)
  Dunit = g/cm3
  Dvalue = 9.32
  Group = -> [At_element001]
  conduct = 2
  density = 1
  expand = 3
  formula = At
  name = G4_At
  specific = 4
FEATURE [App::DocumentObjectGroupPython] Rn_element001  label="Rn_element : 1"  # scripted group (container) (typed FeaturePython)
  n = 1
  ref = Rn_element
FEATURE [App::DocumentObjectGroupPython] G4_Rn  # scripted group (container) (typed FeaturePython)
  Dunit = g/cm3
  Dvalue = 0.00900662
  Group = -> [Rn_element001]
  conduct = 2
  density = 1
  expand = 3
  formula = Rn
  name = G4_Rn
  specific = 4
FEATURE [App::DocumentObjectGroupPython] Fr_element001  label="Fr_element : 1"  # scripted group (container) (typed FeaturePython)
  n = 1
  ref = Fr_element
FEATURE [App::DocumentObjectGroupPython] G4_Fr  # scripted group (container) (typed FeaturePython)
  Dunit = g/cm3
  Dvalue = 1
  Group = -> [Fr_element001]
  conduct = 2
  density = 1
  expand = 3
  formula = Fr
  name = G4_Fr
  specific = 4
FEATURE [App::DocumentObjectGroupPython] Ra_element001  label="Ra_element : 1"  # scripted group (container) (typed FeaturePython)
  n = 1
  ref = Ra_element
FEATURE [App::DocumentObjectGroupPython] G4_Ra  # scripted group (container) (typed FeaturePython)
  Dunit = g/cm3
  Dvalue = 5
  Group = -> [Ra_element001]
  conduct = 2
  density = 1
  expand = 3
  formula = Ra
  name = G4_Ra
  specific = 4
FEATURE [App::DocumentObjectGroupPython] Ac_element001  label="Ac_element : 1"  # scripted group (container) (typed FeaturePython)
  n = 1
  ref = Ac_element
FEATURE [App::DocumentObjectGroupPython] G4_Ac  # scripted group (container) (typed FeaturePython)
  Dunit = g/cm3
  Dvalue = 10.07
  Group = -> [Ac_element001]
  conduct = 2
  density = 1
  expand = 3
  formula = Ac
  name = G4_Ac
  specific = 4
FEATURE [App::DocumentObjectGroupPython] Th_element001  label="Th_element : 1"  # scripted group (container) (typed FeaturePython)
  n = 1
  ref = Th_element
FEATURE [App::DocumentObjectGroupPython] G4_Th  # scripted group (container) (typed FeaturePython)
  Dunit = g/cm3
  Dvalue = 11.72
  Group = -> [Th_element001]
  conduct = 2
  density = 1
  expand = 3
  formula = Th
  name = G4_Th
  specific = 4
FEATURE [App::DocumentObjectGroupPython] Pa_element001  label="Pa_element : 1"  # scripted group (container) (typed FeaturePython)
  n = 1
  ref = Pa_element
FEATURE [App::DocumentObjectGroupPython] G4_Pa  # scripted group (container) (typed FeaturePython)
  Dunit = g/cm3
  Dvalue = 15.37
  Group = -> [Pa_element001]
  conduct = 2
  density = 1
  expand = 3
  formula = Pa
  name = G4_Pa
  specific = 4
FEATURE [App::DocumentObjectGroupPython] U_element004  label="U_element : 004"  # scripted group (container) (typed FeaturePython)
  n = 1
  ref = U_element
FEATURE [App::DocumentObjectGroupPython] G4_U  # scripted group (container) (typed FeaturePython)
  Dunit = g/cm3
  Dvalue = 18.95
  Group = -> [U_element004]
  conduct = 2
  density = 1
  expand = 3
  formula = U
  name = G4_U
  specific = 4
FEATURE [App::DocumentObjectGroupPython] Np_element001  label="Np_element : 1"  # scripted group (container) (typed FeaturePython)
  n = 1
  ref = Np_element
FEATURE [App::DocumentObjectGroupPython] G4_Np  # scripted group (container) (typed FeaturePython)
  Dunit = g/cm3
  Dvalue = 20.25
  Group = -> [Np_element001]
  conduct = 2
  density = 1
  expand = 3
  formula = Np
  name = G4_Np
  specific = 4
FEATURE [App::DocumentObjectGroupPython] Pu_element002  label="Pu_element : 002"  # scripted group (container) (typed FeaturePython)
  n = 1
  ref = Pu_element
FEATURE [App::DocumentObjectGroupPython] G4_Pu  # scripted group (container) (typed FeaturePython)
  Dunit = g/cm3
  Dvalue = 19.84
  Group = -> [Pu_element002]
  conduct = 2
  density = 1
  expand = 3
  formula = Pu
  name = G4_Pu
  specific = 4
FEATURE [App::DocumentObjectGroupPython] Am_element001  label="Am_element : 1"  # scripted group (container) (typed FeaturePython)
  n = 1
  ref = Am_element
FEATURE [App::DocumentObjectGroupPython] G4_Am  # scripted group (container) (typed FeaturePython)
  Dunit = g/cm3
  Dvalue = 13.67
  Group = -> [Am_element001]
  conduct = 2
  density = 1
  expand = 3
  formula = Am
  name = G4_Am
  specific = 4
FEATURE [App::DocumentObjectGroupPython] Cm_element001  label="Cm_element : 1"  # scripted group (container) (typed FeaturePython)
  n = 1
  ref = Cm_element
FEATURE [App::DocumentObjectGroupPython] G4_Cm  # scripted group (container) (typed FeaturePython)
  Dunit = g/cm3
  Dvalue = 13.51
  Group = -> [Cm_element001]
  conduct = 2
  density = 1
  expand = 3
  formula = Cm
  name = G4_Cm
  specific = 4
FEATURE [App::DocumentObjectGroupPython] Bk_element001  label="Bk_element : 1"  # scripted group (container) (typed FeaturePython)
  n = 1
  ref = Bk_element
FEATURE [App::DocumentObjectGroupPython] G4_Bk  # scripted group (container) (typed FeaturePython)
  Dunit = g/cm3
  Dvalue = 14
  Group = -> [Bk_element001]
  conduct = 2
  density = 1
  expand = 3
  formula = Bk
  name = G4_Bk
  specific = 4
FEATURE [App::DocumentObjectGroupPython] Cf_element001  label="Cf_element : 1"  # scripted group (container) (typed FeaturePython)
  n = 1
  ref = Cf_element
FEATURE [App::DocumentObjectGroupPython] G4_Cf  # scripted group (container) (typed FeaturePython)
  Dunit = g/cm3
  Dvalue = 10
  Group = -> [Cf_element001]
  conduct = 2
  density = 1
  expand = 3
  formula = Cf
  name = G4_Cf
  specific = 4
FEATURE [App::DocumentObjectGroupPython] Element  # scripted group (container) (typed FeaturePython)
  Group = -> [G4_H,G4_He,G4_Li,G4_Be,G4_B,G4_C,G4_N,G4_O,G4_F,G4_Ne,G4_Na,G4_Mg,G4_Al,G4_Si,G4_P,G4_S,G4_Cl,G4_Ar,G4_K,G4_Ca,G4_Sc,G4_Ti,G4_V,G4_Cr,G4_Mn,G4_Fe,G4_Co,G4_Ni,G4_Cu,G4_Zn,G4_Ga,G4_Ge,G4_As,G4_Se,G4_Br,G4_Kr,G4_Rb,G4_Sr,G4_Y,G4_Zr,G4_Nb,G4_Mo,G4_Tc,G4_Ru,G4_Rh,G4_Pd,G4_Ag,G4_Cd,G4_In,G4_Sn,G4_Sb,G4_Te,G4_I,G4_Xe,G4_Cs,G4_Ba,G4_La,G4_Ce,G4_Pr,G4_Nd,G4_Pm,G4_Sm,G4_Eu,G4_Gd,G4_Tb,G4_Dy,G4_Ho,G4_Er,+30 more]
FEATURE [App::DocumentObjectGroupPython] H_element114  label="H_element : 063"  # scripted group (container) (typed FeaturePython)
  n = 2
  ref = H_element
FEATURE [App::DocumentObjectGroupPython] G4_lH2  # scripted group (container) (typed FeaturePython)
  Dunit = g/cm3
  Dvalue = 0.0708
  Group = -> [H_element114]
  conduct = 2
  density = 1
  expand = 3
  formula = G4_lH2
  name = G4_lH2
  specific = 4
FEATURE [App::DocumentObjectGroupPython] N_element049  label="N_element : 022"  # scripted group (container) (typed FeaturePython)
  n = 2
  ref = N_element
FEATURE [App::DocumentObjectGroupPython] G4_lN2  # scripted group (container) (typed FeaturePython)
  Dunit = g/cm3
  Dvalue = 0.807
  Group = -> [N_element049]
  conduct = 2
  density = 1
  expand = 3
  formula = G4_lN2
  name = G4_lN2
  specific = 4
FEATURE [App::DocumentObjectGroupPython] O_element106  label="O_element : 060"  # scripted group (container) (typed FeaturePython)
  n = 2
  ref = O_element
FEATURE [App::DocumentObjectGroupPython] G4_lO2  # scripted group (container) (typed FeaturePython)
  Dunit = g/cm3
  Dvalue = 1.141
  Group = -> [O_element106]
  conduct = 2
  density = 1
  expand = 3
  formula = G4_lO2
  name = G4_lO2
  specific = 4
FEATURE [App::DocumentObjectGroupPython] Ar  label="Ar : 1"  # scripted group (container) (typed FeaturePython)
  n = 1
  ref = Ar
FEATURE [App::DocumentObjectGroupPython] G4_lAr  # scripted group (container) (typed FeaturePython)
  Dunit = g/cm3
  Dvalue = 1.396
  Group = -> [Ar]
  conduct = 2
  density = 1
  expand = 3
  formula = G4_lAr
  name = G4_lAr
  specific = 4
FEATURE [App::DocumentObjectGroupPython] Br  label="Br : 1"  # scripted group (container) (typed FeaturePython)
  n = 1
  ref = Br
FEATURE [App::DocumentObjectGroupPython] G4_lBr  # scripted group (container) (typed FeaturePython)
  Dunit = g/cm3
  Dvalue = 3.1028
  Group = -> [Br]
  conduct = 2
  density = 1
  expand = 3
  formula = G4_lBr
  name = G4_lBr
  specific = 4
FEATURE [App::DocumentObjectGroupPython] Kr  label="Kr : 1"  # scripted group (container) (typed FeaturePython)
  n = 1
  ref = Kr
FEATURE [App::DocumentObjectGroupPython] G4_lKr  # scripted group (container) (typed FeaturePython)
  Dunit = g/cm3
  Dvalue = 2.418
  Group = -> [Kr]
  conduct = 2
  density = 1
  expand = 3
  formula = G4_lKr
  name = G4_lKr
  specific = 4
FEATURE [App::DocumentObjectGroupPython] Xe  label="Xe : 1"  # scripted group (container) (typed FeaturePython)
  n = 1
  ref = Xe
FEATURE [App::DocumentObjectGroupPython] G4_lXe  # scripted group (container) (typed FeaturePython)
  Dunit = g/cm3
  Dvalue = 2.953
  Group = -> [Xe]
  conduct = 2
  density = 1
  expand = 3
  formula = G4_lXe
  name = G4_lXe
  specific = 4
FEATURE [App::DocumentObjectGroupPython] O_element107  label="O_element : 061"  # scripted group (container) (typed FeaturePython)
  n = 4
  ref = O_element
FEATURE [App::DocumentObjectGroupPython] Pb_element004  label="Pb_element : 002"  # scripted group (container) (typed FeaturePython)
  n = 1
  ref = Pb_element
FEATURE [App::DocumentObjectGroupPython] W_element005  label="W_element : 005"  # scripted group (container) (typed FeaturePython)
  n = 1
  ref = W_element
FEATURE [App::DocumentObjectGroupPython] G4_PbWO4  # scripted group (container) (typed FeaturePython)
  Dunit = g/cm3
  Dvalue = 8.28
  Group = -> [O_element107,Pb_element004,W_element005]
  conduct = 2
  density = 1
  expand = 3
  formula = G4_PbWO4
  name = G4_PbWO4
  specific = 4
FEATURE [App::DocumentObjectGroupPython] alactic  label="alactic : 1"  # scripted group (container) (typed FeaturePython)
  n = 1
  ref = alactic
FEATURE [App::DocumentObjectGroupPython] G4_Galactic  # scripted group (container) (typed FeaturePython)
  Dunit = g/cm3
  Dvalue = 0
  Group = -> [alactic]
  conduct = 2
  density = 1
  expand = 3
  formula = G4_Galactic
  name = G4_Galactic
  specific = 4
FEATURE [App::DocumentObjectGroupPython] RAPHITE_POROUS  label="RAPHITE_POROUS : 1"  # scripted group (container) (typed FeaturePython)
  n = 1
  ref = RAPHITE_POROUS
FEATURE [App::DocumentObjectGroupPython] G4_GRAPHITE_POROUS  # scripted group (container) (typed FeaturePython)
  Dunit = g/cm3
  Dvalue = 1.7
  Group = -> [RAPHITE_POROUS]
  conduct = 2
  density = 1
  expand = 3
  formula = G4_GRAPHITE_POROUS
  name = G4_GRAPHITE_POROUS
  specific = 4
FEATURE [App::DocumentObjectGroupPython] H_element115  label="H_element : 0.150"  # scripted group (container) (typed FeaturePython)
  n = 0.080538
FEATURE [App::DocumentObjectGroupPython] C_element125  label="C_element : 0.600"  # scripted group (container) (typed FeaturePython)
  n = 0.599848
FEATURE [App::DocumentObjectGroupPython] O_element108  label="O_element : 0.320"  # scripted group (container) (typed FeaturePython)
  n = 0.319614
FEATURE [App::DocumentObjectGroupPython] G4_LUCITE  # scripted group (container) (typed FeaturePython)
  Dunit = g/cm3
  Dvalue = 1.19
  Group = -> [H_element115,C_element125,O_element108]
  conduct = 2
  density = 1
  expand = 3
  formula = G4_LUCITE
  name = G4_LUCITE
  specific = 4
FEATURE [App::DocumentObjectGroupPython] Cu_element002  label="Cu_element : 62"  # scripted group (container) (typed FeaturePython)
  n = 62
  ref = Cu_element
FEATURE [App::DocumentObjectGroupPython] Zn_element002  label="Zn_element : 35"  # scripted group (container) (typed FeaturePython)
  n = 35
  ref = Zn_element
FEATURE [App::DocumentObjectGroupPython] Pb_element005  label="Pb_element : 3"  # scripted group (container) (typed FeaturePython)
  n = 3
  ref = Pb_element
FEATURE [App::DocumentObjectGroupPython] G4_BRASS  # scripted group (container) (typed FeaturePython)
  Dunit = g/cm3
  Dvalue = 8.52
  Group = -> [Cu_element002,Zn_element002,Pb_element005]
  conduct = 2
  density = 1
  expand = 3
  formula = G4_BRASS
  name = G4_BRASS
  specific = 4
FEATURE [App::DocumentObjectGroupPython] Cu_element003  label="Cu_element : 89"  # scripted group (container) (typed FeaturePython)
  n = 89
  ref = Cu_element
FEATURE [App::DocumentObjectGroupPython] Zn_element003  label="Zn_element : 9"  # scripted group (container) (typed FeaturePython)
  n = 9
  ref = Zn_element
FEATURE [App::DocumentObjectGroupPython] Pb_element006  label="Pb_element : 2"  # scripted group (container) (typed FeaturePython)
  n = 2
  ref = Pb_element
FEATURE [App::DocumentObjectGroupPython] G4_BRONZE  # scripted group (container) (typed FeaturePython)
  Dunit = g/cm3
  Dvalue = 8.82
  Group = -> [Cu_element003,Zn_element003,Pb_element006]
  conduct = 2
  density = 1
  expand = 3
  formula = G4_BRONZE
  name = G4_BRONZE
  specific = 4
FEATURE [App::DocumentObjectGroupPython] Fe_element008  label="Fe_element : 74"  # scripted group (container) (typed FeaturePython)
  n = 74
  ref = Fe_element
FEATURE [App::DocumentObjectGroupPython] Cr_element002  label="Cr_element : 18"  # scripted group (container) (typed FeaturePython)
  n = 18
  ref = Cr_element
FEATURE [App::DocumentObjectGroupPython] Ni_element002  label="Ni_element : 8"  # scripted group (container) (typed FeaturePython)
  n = 8
  ref = Ni_element
FEATURE [App::DocumentObjectGroupPython] G4_STAINLESS_STEEL  label="G4_STAINLESS-STEEL"  # scripted group (container) (typed FeaturePython)
  Dunit = g/cm3
  Dvalue = 8
  Group = -> [Fe_element008,Cr_element002,Ni_element002]
  conduct = 2
  density = 1
  expand = 3
  formula = G4_STAINLESS-STEEL
  name = G4_STAINLESS-STEEL
  specific = 4
FEATURE [App::DocumentObjectGroupPython] H_element116  label="H_element : 064"  # scripted group (container) (typed FeaturePython)
  n = 18
  ref = H_element
FEATURE [App::DocumentObjectGroupPython] C_element126  label="C_element : 071"  # scripted group (container) (typed FeaturePython)
  n = 12
  ref = C_element
FEATURE [App::DocumentObjectGroupPython] O_element109  label="O_element : 062"  # scripted group (container) (typed FeaturePython)
  n = 7
  ref = O_element
FEATURE [App::DocumentObjectGroupPython] G4_CR39  # scripted group (container) (typed FeaturePython)
  Dunit = g/cm3
  Dvalue = 1.32
  Group = -> [H_element116,C_element126,O_element109]
  conduct = 2
  density = 1
  expand = 3
  formula = G4_CR39
  name = G4_CR39
  specific = 4
FEATURE [App::DocumentObjectGroupPython] H_element117  label="H_element : 38"  # scripted group (container) (typed FeaturePython)
  n = 38
  ref = H_element
FEATURE [App::DocumentObjectGroupPython] C_element127  label="C_element : 072"  # scripted group (container) (typed FeaturePython)
  n = 18
  ref = C_element
FEATURE [App::DocumentObjectGroupPython] O_element110  label="O_element : 063"  # scripted group (container) (typed FeaturePython)
  n = 1
  ref = O_element
FEATURE [App::DocumentObjectGroupPython] G4_OCTADECANOL  # scripted group (container) (typed FeaturePython)
  Dunit = g/cm3
  Dvalue = 0.812
  Group = -> [H_element117,C_element127,O_element110]
  conduct = 2
  density = 1
  expand = 3
  formula = G4_OCTADECANOL
  name = G4_OCTADECANOL
  specific = 4
FEATURE [App::DocumentObjectGroupPython] HEP  # scripted group (container) (typed FeaturePython)
  Group = -> [G4_lH2,G4_lN2,G4_lO2,G4_lAr,G4_lBr,G4_lKr,G4_lXe,G4_PbWO4,G4_Galactic,G4_GRAPHITE_POROUS,G4_LUCITE,G4_BRASS,G4_BRONZE,G4_STAINLESS_STEEL,G4_CR39,G4_OCTADECANOL]
FEATURE [App::DocumentObjectGroupPython] C_element128  label="C_element : 073"  # scripted group (container) (typed FeaturePython)
  n = 14
  ref = C_element
FEATURE [App::DocumentObjectGroupPython] H_element118  label="H_element : 065"  # scripted group (container) (typed FeaturePython)
  n = 10
  ref = H_element
FEATURE [App::DocumentObjectGroupPython] O_element111  label="O_element : 064"  # scripted group (container) (typed FeaturePython)
  n = 2
  ref = O_element
FEATURE [App::DocumentObjectGroupPython] N_element050  label="N_element : 023"  # scripted group (container) (typed FeaturePython)
  n = 2
  ref = N_element
FEATURE [App::DocumentObjectGroupPython] G4_KEVLAR  # scripted group (container) (typed FeaturePython)
  Dunit = g/cm3
  Dvalue = 1.44
  Group = -> [C_element128,H_element118,O_element111,N_element050]
  conduct = 2
  density = 1
  expand = 3
  formula = G4_KEVLAR
  name = G4_KEVLAR
  specific = 4
FEATURE [App::DocumentObjectGroupPython] C_element129  label="C_element : 074"  # scripted group (container) (typed FeaturePython)
  n = 10
  ref = C_element
FEATURE [App::DocumentObjectGroupPython] H_element119  label="H_element : 066"  # scripted group (container) (typed FeaturePython)
  n = 8
  ref = H_element
FEATURE [App::DocumentObjectGroupPython] O_element112  label="O_element : 065"  # scripted group (container) (typed FeaturePython)
  n = 4
  ref = O_element
FEATURE [App::DocumentObjectGroupPython] G4_DACRON  # scripted group (container) (typed FeaturePython)
  Dunit = g/cm3
  Dvalue = 1.4
  Group = -> [C_element129,H_element119,O_element112]
  conduct = 2
  density = 1
  expand = 3
  formula = G4_DACRON
  name = G4_DACRON
  specific = 4
FEATURE [App::DocumentObjectGroupPython] C_element130  label="C_element : 075"  # scripted group (container) (typed FeaturePython)
  n = 4
  ref = C_element
FEATURE [App::DocumentObjectGroupPython] H_element120  label="H_element : 067"  # scripted group (container) (typed FeaturePython)
  n = 5
  ref = H_element
FEATURE [App::DocumentObjectGroupPython] Cl_element030  label="Cl_element : 016"  # scripted group (container) (typed FeaturePython)
  n = 1
  ref = Cl_element
FEATURE [App::DocumentObjectGroupPython] G4_NEOPRENE  # scripted group (container) (typed FeaturePython)
  Dunit = g/cm3
  Dvalue = 1.23
  Group = -> [C_element130,H_element120,Cl_element030]
  conduct = 2
  density = 1
  expand = 3
  formula = G4_NEOPRENE
  name = G4_NEOPRENE
  specific = 4
FEATURE [App::DocumentObjectGroupPython] Space  # scripted group (container) (typed FeaturePython)
  Group = -> [G4_KEVLAR,G4_DACRON,G4_NEOPRENE]
FEATURE [App::DocumentObjectGroupPython] H_element121  label="H_element : 068"  # scripted group (container) (typed FeaturePython)
  n = 5
  ref = H_element
FEATURE [App::DocumentObjectGroupPython] C_element131  label="C_element : 076"  # scripted group (container) (typed FeaturePython)
  n = 4
  ref = C_element
FEATURE [App::DocumentObjectGroupPython] N_element051  label="N_element : 3"  # scripted group (container) (typed FeaturePython)
  n = 3
  ref = N_element
FEATURE [App::DocumentObjectGroupPython] O_element113  label="O_element : 066"  # scripted group (container) (typed FeaturePython)
  n = 1
  ref = O_element
FEATURE [App::DocumentObjectGroupPython] G4_CYTOSINE  # scripted group (container) (typed FeaturePython)
  Dunit = g/cm3
  Dvalue = 1.55
  Group = -> [H_element121,C_element131,N_element051,O_element113]
  conduct = 2
  density = 1
  expand = 3
  formula = G4_CYTOSINE
  name = G4_CYTOSINE
  specific = 4
FEATURE [App::DocumentObjectGroupPython] H_element122  label="H_element : 069"  # scripted group (container) (typed FeaturePython)
  n = 6
  ref = H_element
FEATURE [App::DocumentObjectGroupPython] C_element132  label="C_element : 077"  # scripted group (container) (typed FeaturePython)
  n = 5
  ref = C_element
FEATURE [App::DocumentObjectGroupPython] N_element052  label="N_element : 024"  # scripted group (container) (typed FeaturePython)
  n = 2
  ref = N_element
FEATURE [App::DocumentObjectGroupPython] O_element114  label="O_element : 067"  # scripted group (container) (typed FeaturePython)
  n = 2
  ref = O_element
FEATURE [App::DocumentObjectGroupPython] G4_THYMINE  # scripted group (container) (typed FeaturePython)
  Dunit = g/cm3
  Dvalue = 1.23
  Group = -> [H_element122,C_element132,N_element052,O_element114]
  conduct = 2
  density = 1
  expand = 3
  formula = G4_THYMINE
  name = G4_THYMINE
  specific = 4
FEATURE [App::DocumentObjectGroupPython] H_element123  label="H_element : 070"  # scripted group (container) (typed FeaturePython)
  n = 4
  ref = H_element
FEATURE [App::DocumentObjectGroupPython] C_element133  label="C_element : 078"  # scripted group (container) (typed FeaturePython)
  n = 4
  ref = C_element
FEATURE [App::DocumentObjectGroupPython] N_element053  label="N_element : 025"  # scripted group (container) (typed FeaturePython)
  n = 2
  ref = N_element
FEATURE [App::DocumentObjectGroupPython] O_element115  label="O_element : 068"  # scripted group (container) (typed FeaturePython)
  n = 2
  ref = O_element
FEATURE [App::DocumentObjectGroupPython] G4_URACIL  # scripted group (container) (typed FeaturePython)
  Dunit = g/cm3
  Dvalue = 1.32
  Group = -> [H_element123,C_element133,N_element053,O_element115]
  conduct = 2
  density = 1
  expand = 3
  formula = G4_URACIL
  name = G4_URACIL
  specific = 4
FEATURE [App::DocumentObjectGroupPython] H_element124  label="H_element : 071"  # scripted group (container) (typed FeaturePython)
  n = 4
  ref = H_element
FEATURE [App::DocumentObjectGroupPython] C_element134  label="C_element : 079"  # scripted group (container) (typed FeaturePython)
  n = 5
  ref = C_element
FEATURE [App::DocumentObjectGroupPython] N_element054  label="N_element : 026"  # scripted group (container) (typed FeaturePython)
  n = 5
  ref = N_element
FEATURE [App::DocumentObjectGroupPython] G4_DNA_ADENINE  # scripted group (container) (typed FeaturePython)
  Dunit = g/cm3
  Dvalue = 1
  Group = -> [H_element124,C_element134,N_element054]
  conduct = 2
  density = 1
  expand = 3
  formula = G4_DNA_ADENINE
  name = G4_DNA_ADENINE
  specific = 4
FEATURE [App::DocumentObjectGroupPython] H_element125  label="H_element : 072"  # scripted group (container) (typed FeaturePython)
  n = 4
  ref = H_element
FEATURE [App::DocumentObjectGroupPython] C_element135  label="C_element : 080"  # scripted group (container) (typed FeaturePython)
  n = 5
  ref = C_element
FEATURE [App::DocumentObjectGroupPython] N_element055  label="N_element : 027"  # scripted group (container) (typed FeaturePython)
  n = 5
  ref = N_element
FEATURE [App::DocumentObjectGroupPython] O_element116  label="O_element : 069"  # scripted group (container) (typed FeaturePython)
  n = 1
  ref = O_element
FEATURE [App::DocumentObjectGroupPython] G4_DNA_GUANINE  # scripted group (container) (typed FeaturePython)
  Dunit = g/cm3
  Dvalue = 1
  Group = -> [H_element125,C_element135,N_element055,O_element116]
  conduct = 2
  density = 1
  expand = 3
  formula = G4_DNA_GUANINE
  name = G4_DNA_GUANINE
  specific = 4
FEATURE [App::DocumentObjectGroupPython] H_element126  label="H_element : 073"  # scripted group (container) (typed FeaturePython)
  n = 4
  ref = H_element
FEATURE [App::DocumentObjectGroupPython] C_element136  label="C_element : 081"  # scripted group (container) (typed FeaturePython)
  n = 4
  ref = C_element
FEATURE [App::DocumentObjectGroupPython] N_element056  label="N_element : 028"  # scripted group (container) (typed FeaturePython)
  n = 3
  ref = N_element
FEATURE [App::DocumentObjectGroupPython] O_element117  label="O_element : 070"  # scripted group (container) (typed FeaturePython)
  n = 1
  ref = O_element
FEATURE [App::DocumentObjectGroupPython] G4_DNA_CYTOSINE  # scripted group (container) (typed FeaturePython)
  Dunit = g/cm3
  Dvalue = 1
  Group = -> [H_element126,C_element136,N_element056,O_element117]
  conduct = 2
  density = 1
  expand = 3
  formula = G4_DNA_CYTOSINE
  name = G4_DNA_CYTOSINE
  specific = 4
FEATURE [App::DocumentObjectGroupPython] H_element127  label="H_element : 074"  # scripted group (container) (typed FeaturePython)
  n = 5
  ref = H_element
FEATURE [App::DocumentObjectGroupPython] C_element137  label="C_element : 082"  # scripted group (container) (typed FeaturePython)
  n = 5
  ref = C_element
FEATURE [App::DocumentObjectGroupPython] N_element057  label="N_element : 029"  # scripted group (container) (typed FeaturePython)
  n = 2
  ref = N_element
FEATURE [App::DocumentObjectGroupPython] O_element118  label="O_element : 071"  # scripted group (container) (typed FeaturePython)
  n = 2
  ref = O_element
FEATURE [App::DocumentObjectGroupPython] G4_DNA_THYMINE  # scripted group (container) (typed FeaturePython)
  Dunit = g/cm3
  Dvalue = 1
  Group = -> [H_element127,C_element137,N_element057,O_element118]
  conduct = 2
  density = 1
  expand = 3
  formula = G4_DNA_THYMINE
  name = G4_DNA_THYMINE
  specific = 4
FEATURE [App::DocumentObjectGroupPython] H_element128  label="H_element : 075"  # scripted group (container) (typed FeaturePython)
  n = 3
  ref = H_element
FEATURE [App::DocumentObjectGroupPython] C_element138  label="C_element : 083"  # scripted group (container) (typed FeaturePython)
  n = 4
  ref = C_element
FEATURE [App::DocumentObjectGroupPython] N_element058  label="N_element : 030"  # scripted group (container) (typed FeaturePython)
  n = 2
  ref = N_element
FEATURE [App::DocumentObjectGroupPython] O_element119  label="O_element : 072"  # scripted group (container) (typed FeaturePython)
  n = 2
  ref = O_element
FEATURE [App::DocumentObjectGroupPython] G4_DNA_URACIL  # scripted group (container) (typed FeaturePython)
  Dunit = g/cm3
  Dvalue = 1
  Group = -> [H_element128,C_element138,N_element058,O_element119]
  conduct = 2
  density = 1
  expand = 3
  formula = G4_DNA_URACIL
  name = G4_DNA_URACIL
  specific = 4
FEATURE [App::DocumentObjectGroupPython] H_element129  label="H_element : 076"  # scripted group (container) (typed FeaturePython)
  n = 10
  ref = H_element
FEATURE [App::DocumentObjectGroupPython] C_element139  label="C_element : 084"  # scripted group (container) (typed FeaturePython)
  n = 10
  ref = C_element
FEATURE [App::DocumentObjectGroupPython] N_element059  label="N_element : 031"  # scripted group (container) (typed FeaturePython)
  n = 5
  ref = N_element
FEATURE [App::DocumentObjectGroupPython] O_element120  label="O_element : 073"  # scripted group (container) (typed FeaturePython)
  n = 4
  ref = O_element
FEATURE [App::DocumentObjectGroupPython] G4_DNA_ADENOSINE  # scripted group (container) (typed FeaturePython)
  Dunit = g/cm3
  Dvalue = 1
  Group = -> [H_element129,C_element139,N_element059,O_element120]
  conduct = 2
  density = 1
  expand = 3
  formula = G4_DNA_ADENOSINE
  name = G4_DNA_ADENOSINE
  specific = 4
FEATURE [App::DocumentObjectGroupPython] H_element130  label="H_element : 077"  # scripted group (container) (typed FeaturePython)
  n = 10
  ref = H_element
FEATURE [App::DocumentObjectGroupPython] C_element140  label="C_element : 085"  # scripted group (container) (typed FeaturePython)
  n = 10
  ref = C_element
FEATURE [App::DocumentObjectGroupPython] N_element060  label="N_element : 032"  # scripted group (container) (typed FeaturePython)
  n = 5
  ref = N_element
FEATURE [App::DocumentObjectGroupPython] O_element121  label="O_element : 074"  # scripted group (container) (typed FeaturePython)
  n = 5
  ref = O_element
FEATURE [App::DocumentObjectGroupPython] G4_DNA_GUANOSINE  # scripted group (container) (typed FeaturePython)
  Dunit = g/cm3
  Dvalue = 1
  Group = -> [H_element130,C_element140,N_element060,O_element121]
  conduct = 2
  density = 1
  expand = 3
  formula = G4_DNA_GUANOSINE
  name = G4_DNA_GUANOSINE
  specific = 4
FEATURE [App::DocumentObjectGroupPython] H_element131  label="H_element : 078"  # scripted group (container) (typed FeaturePython)
  n = 10
  ref = H_element
FEATURE [App::DocumentObjectGroupPython] C_element141  label="C_element : 086"  # scripted group (container) (typed FeaturePython)
  n = 9
  ref = C_element
FEATURE [App::DocumentObjectGroupPython] N_element061  label="N_element : 033"  # scripted group (container) (typed FeaturePython)
  n = 3
  ref = N_element
FEATURE [App::DocumentObjectGroupPython] O_element122  label="O_element : 075"  # scripted group (container) (typed FeaturePython)
  n = 5
  ref = O_element
FEATURE [App::DocumentObjectGroupPython] G4_DNA_CYTIDINE  # scripted group (container) (typed FeaturePython)
  Dunit = g/cm3
  Dvalue = 1
  Group = -> [H_element131,C_element141,N_element061,O_element122]
  conduct = 2
  density = 1
  expand = 3
  formula = G4_DNA_CYTIDINE
  name = G4_DNA_CYTIDINE
  specific = 4
FEATURE [App::DocumentObjectGroupPython] H_element132  label="H_element : 079"  # scripted group (container) (typed FeaturePython)
  n = 9
  ref = H_element
FEATURE [App::DocumentObjectGroupPython] C_element142  label="C_element : 087"  # scripted group (container) (typed FeaturePython)
  n = 9
  ref = C_element
FEATURE [App::DocumentObjectGroupPython] N_element062  label="N_element : 034"  # scripted group (container) (typed FeaturePython)
  n = 2
  ref = N_element
FEATURE [App::DocumentObjectGroupPython] O_element123  label="O_element : 076"  # scripted group (container) (typed FeaturePython)
  n = 6
  ref = O_element
FEATURE [App::DocumentObjectGroupPython] G4_DNA_URIDINE  # scripted group (container) (typed FeaturePython)
  Dunit = g/cm3
  Dvalue = 1
  Group = -> [H_element132,C_element142,N_element062,O_element123]
  conduct = 2
  density = 1
  expand = 3
  formula = G4_DNA_URIDINE
  name = G4_DNA_URIDINE
  specific = 4
FEATURE [App::DocumentObjectGroupPython] H_element133  label="H_element : 080"  # scripted group (container) (typed FeaturePython)
  n = 11
  ref = H_element
FEATURE [App::DocumentObjectGroupPython] C_element143  label="C_element : 088"  # scripted group (container) (typed FeaturePython)
  n = 10
  ref = C_element
FEATURE [App::DocumentObjectGroupPython] N_element063  label="N_element : 035"  # scripted group (container) (typed FeaturePython)
  n = 2
  ref = N_element
FEATURE [App::DocumentObjectGroupPython] O_element124  label="O_element : 077"  # scripted group (container) (typed FeaturePython)
  n = 6
  ref = O_element
FEATURE [App::DocumentObjectGroupPython] G4_DNA_METHYLURIDINE  # scripted group (container) (typed FeaturePython)
  Dunit = g/cm3
  Dvalue = 1
  Group = -> [H_element133,C_element143,N_element063,O_element124]
  conduct = 2
  density = 1
  expand = 3
  formula = G4_DNA_METHYLURIDINE
  name = G4_DNA_METHYLURIDINE
  specific = 4
FEATURE [App::DocumentObjectGroupPython] P_element014  label="P_element : 003"  # scripted group (container) (typed FeaturePython)
  n = 1
  ref = P_element
FEATURE [App::DocumentObjectGroupPython] O_element125  label="O_element : 078"  # scripted group (container) (typed FeaturePython)
  n = 3
  ref = O_element
FEATURE [App::DocumentObjectGroupPython] G4_DNA_MONOPHOSPHATE  # scripted group (container) (typed FeaturePython)
  Dunit = g/cm3
  Dvalue = 1
  Group = -> [P_element014,O_element125]
  conduct = 2
  density = 1
  expand = 3
  formula = G4_DNA_MONOPHOSPHATE
  name = G4_DNA_MONOPHOSPHATE
  specific = 4
FEATURE [App::DocumentObjectGroupPython] H_element134  label="H_element : 081"  # scripted group (container) (typed FeaturePython)
  n = 10
  ref = H_element
FEATURE [App::DocumentObjectGroupPython] C_element144  label="C_element : 089"  # scripted group (container) (typed FeaturePython)
  n = 10
  ref = C_element
FEATURE [App::DocumentObjectGroupPython] N_element064  label="N_element : 036"  # scripted group (container) (typed FeaturePython)
  n = 5
  ref = N_element
FEATURE [App::DocumentObjectGroupPython] O_element126  label="O_element : 079"  # scripted group (container) (typed FeaturePython)
  n = 7
  ref = O_element
FEATURE [App::DocumentObjectGroupPython] P_element015  label="P_element : 004"  # scripted group (container) (typed FeaturePython)
  n = 1
  ref = P_element
FEATURE [App::DocumentObjectGroupPython] G4_DNA_A  # scripted group (container) (typed FeaturePython)
  Dunit = g/cm3
  Dvalue = 1
  Group = -> [H_element134,C_element144,N_element064,O_element126,P_element015]
  conduct = 2
  density = 1
  expand = 3
  formula = G4_DNA_A
  name = G4_DNA_A
  specific = 4
FEATURE [App::DocumentObjectGroupPython] H_element135  label="H_element : 082"  # scripted group (container) (typed FeaturePython)
  n = 10
  ref = H_element
FEATURE [App::DocumentObjectGroupPython] C_element145  label="C_element : 090"  # scripted group (container) (typed FeaturePython)
  n = 10
  ref = C_element
FEATURE [App::DocumentObjectGroupPython] N_element065  label="N_element : 037"  # scripted group (container) (typed FeaturePython)
  n = 5
  ref = N_element
FEATURE [App::DocumentObjectGroupPython] O_element127  label="O_element : 8"  # scripted group (container) (typed FeaturePython)
  n = 8
  ref = O_element
FEATURE [App::DocumentObjectGroupPython] P_element016  label="P_element : 005"  # scripted group (container) (typed FeaturePython)
  n = 1
  ref = P_element
FEATURE [App::DocumentObjectGroupPython] G4_DNA_G  # scripted group (container) (typed FeaturePython)
  Dunit = g/cm3
  Dvalue = 1
  Group = -> [H_element135,C_element145,N_element065,O_element127,P_element016]
  conduct = 2
  density = 1
  expand = 3
  formula = G4_DNA_G
  name = G4_DNA_G
  specific = 4
FEATURE [App::DocumentObjectGroupPython] H_element136  label="H_element : 083"  # scripted group (container) (typed FeaturePython)
  n = 10
  ref = H_element
FEATURE [App::DocumentObjectGroupPython] C_element146  label="C_element : 091"  # scripted group (container) (typed FeaturePython)
  n = 9
  ref = C_element
FEATURE [App::DocumentObjectGroupPython] N_element066  label="N_element : 038"  # scripted group (container) (typed FeaturePython)
  n = 3
  ref = N_element
FEATURE [App::DocumentObjectGroupPython] O_element128  label="O_element : 080"  # scripted group (container) (typed FeaturePython)
  n = 8
  ref = O_element
FEATURE [App::DocumentObjectGroupPython] P_element017  label="P_element : 006"  # scripted group (container) (typed FeaturePython)
  n = 1
  ref = P_element
FEATURE [App::DocumentObjectGroupPython] G4_DNA_C  # scripted group (container) (typed FeaturePython)
  Dunit = g/cm3
  Dvalue = 1
  Group = -> [H_element136,C_element146,N_element066,O_element128,P_element017]
  conduct = 2
  density = 1
  expand = 3
  formula = G4_DNA_C
  name = G4_DNA_C
  specific = 4
FEATURE [App::DocumentObjectGroupPython] H_element137  label="H_element : 084"  # scripted group (container) (typed FeaturePython)
  n = 9
  ref = H_element
FEATURE [App::DocumentObjectGroupPython] C_element147  label="C_element : 092"  # scripted group (container) (typed FeaturePython)
  n = 9
  ref = C_element
FEATURE [App::DocumentObjectGroupPython] N_element067  label="N_element : 039"  # scripted group (container) (typed FeaturePython)
  n = 2
  ref = N_element
FEATURE [App::DocumentObjectGroupPython] O_element129  label="O_element : 9"  # scripted group (container) (typed FeaturePython)
  n = 9
  ref = O_element
FEATURE [App::DocumentObjectGroupPython] P_element018  label="P_element : 007"  # scripted group (container) (typed FeaturePython)
  n = 1
  ref = P_element
FEATURE [App::DocumentObjectGroupPython] G4_DNA_U  # scripted group (container) (typed FeaturePython)
  Dunit = g/cm3
  Dvalue = 1
  Group = -> [H_element137,C_element147,N_element067,O_element129,P_element018]
  conduct = 2
  density = 1
  expand = 3
  formula = G4_DNA_U
  name = G4_DNA_U
  specific = 4
FEATURE [App::DocumentObjectGroupPython] H_element138  label="H_element : 085"  # scripted group (container) (typed FeaturePython)
  n = 11
  ref = H_element
FEATURE [App::DocumentObjectGroupPython] C_element148  label="C_element : 093"  # scripted group (container) (typed FeaturePython)
  n = 10
  ref = C_element
FEATURE [App::DocumentObjectGroupPython] N_element068  label="N_element : 040"  # scripted group (container) (typed FeaturePython)
  n = 2
  ref = N_element
FEATURE [App::DocumentObjectGroupPython] O_element130  label="O_element : 081"  # scripted group (container) (typed FeaturePython)
  n = 9
  ref = O_element
FEATURE [App::DocumentObjectGroupPython] P_element019  label="P_element : 008"  # scripted group (container) (typed FeaturePython)
  n = 1
  ref = P_element
FEATURE [App::DocumentObjectGroupPython] G4_DNA_MU  # scripted group (container) (typed FeaturePython)
  Dunit = g/cm3
  Dvalue = 1
  Group = -> [H_element138,C_element148,N_element068,O_element130,P_element019]
  conduct = 2
  density = 1
  expand = 3
  formula = G4_DNA_MU
  name = G4_DNA_MU
  specific = 4
FEATURE [App::DocumentObjectGroupPython] BioChemical  # scripted group (container) (typed FeaturePython)
  Group = -> [G4_CYTOSINE,G4_THYMINE,G4_URACIL,G4_DNA_ADENINE,G4_DNA_GUANINE,G4_DNA_CYTOSINE,G4_DNA_THYMINE,G4_DNA_URACIL,G4_DNA_ADENOSINE,G4_DNA_GUANOSINE,G4_DNA_CYTIDINE,G4_DNA_URIDINE,G4_DNA_METHYLURIDINE,G4_DNA_MONOPHOSPHATE,G4_DNA_A,G4_DNA_G,G4_DNA_C,G4_DNA_U,G4_DNA_MU]
FEATURE [App::DocumentObjectGroupPython] G4Materials  # scripted group (container) (typed FeaturePython)
  Group = -> [NIST,Element,HEP,Space,BioChemical]
  version = 1
FEATURE [App::DocumentObjectGroupPython] Geant4  # scripted group (container) (typed FeaturePython)
  Group = -> [G4Isotopes,G4Elements,G4Materials]
FEATURE [App::DocumentObjectGroupPython] Materials  # scripted group (container) (typed FeaturePython)
  Group = -> [Geant4]
FEATURE [Part::FeaturePython] GDMLBox_WorldBox  # WARN: FeaturePython — macro-defined, semantics opaque (R4)
  lunit = 2
  material = 5
  x = 374.4
  y = 354.9
  z = 169
FEATURE [Part::FeaturePython] GDMLTube  # WARN: FeaturePython — macro-defined, semantics opaque (R4)
  Placement = pos=(17,-4,0) rot=(0,0,1;0rad)
  aunit = 1
  deltaphi = 90
  lunit = 2
  material = 0
  rmax = 7
  rmin = 5
  startphi = 0
  z = 7
FEATURE [App::Part] LV_Tube
  Group = -> [GDMLTube]
  Origin = -> Origin003
  SkinSurface = 0
FEATURE [Part::FeaturePython] GDMLSphere  # WARN: FeaturePython — macro-defined, semantics opaque (R4)
  aunit = 1
  deltaphi = 360
  deltatheta = 180
  lunit = 2
  material = 0
  rmax = 2
  rmin = 0
  startphi = 0
  starttheta = 0
FEATURE [App::Part] LV_Sphere
  Group = -> [GDMLSphere]
  Origin = -> Origin004
  Placement = pos=(15,-5,0) rot=(0,0,1;0rad)
  SkinSurface = 0
FEATURE [App::Part] LV_Box  label="Assembly"
  Group = -> [LV_Tube,LV_Sphere]
  Origin = -> Origin002
  Placement = pos=(20,0,0) rot=(0,0,1;0rad)
FEATURE [Part::FeaturePython] Array001  # Draft array (typed FeaturePython)
  AlwaysSyncPlacement = false
  Angle = 360
  ArrayType = 0
  Axis = (0,0,1)
  Base = -> LV_Box
  Center = (0,0,0)
  Count = 4
  ExpandArray = false
  Fuse = true
  IntervalAxis = (0,0,0)
  IntervalX = (30,0,0)
  IntervalY = (0,30,0)
  IntervalZ = (0,0,100)
  NumberCircles = 3
  NumberPolar = 5
  NumberX = 2
  NumberY = 2
  NumberZ = 1
  Placement = pos=(40,0,0) rot=(0,0,1;0rad)
  PlacementList = 4 placements: [(20,0,0),(20,30,0),(50,0,0),(50,30,0)]
  RadialDistance = 50
  ScaleList = (4) [(1,1,1),(1,1,1),(1,1,1),(1,1,1)]
  Symmetry = 1
  TangentialDistance = 25
FEATURE [App::Part] Part001
  Group = -> [LV_Box,Array001]
  Origin = -> Origin005
FEATURE [Part::FeaturePython] Array  # Draft array (typed FeaturePython)
  Angle = 360
  ArrayType = 1
  Axis = (0,0,1)
  Base = -> Part001
  Center = (0,0,0)
  Count = 6
  Fuse = false
  IntervalAxis = (0,0,0)
  IntervalX = (50,0,0)
  IntervalY = (0,50,0)
  IntervalZ = (0,0,50)
  NumberCircles = 3
  NumberPolar = 6
  NumberX = 2
  NumberY = 2
  NumberZ = 1
  RadialDistance = 50
  Symmetry = 1
  TangentialDistance = 25
FEATURE [App::Part] Part  label="experiment"
  Group = -> [Array,Part001]
  Origin = -> Origin001
FEATURE [App::Part] worldVOL
  Group = -> [GDMLBox_WorldBox,Part]
  Origin = -> Origin
